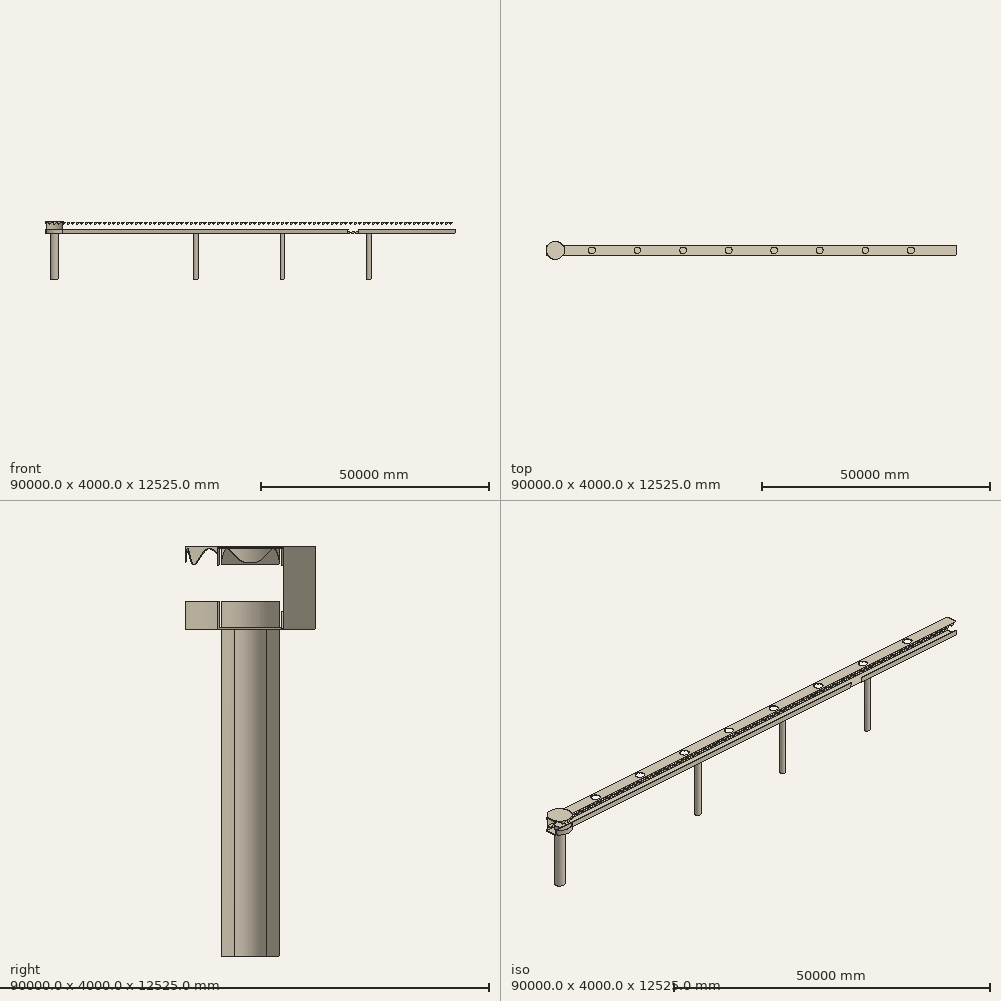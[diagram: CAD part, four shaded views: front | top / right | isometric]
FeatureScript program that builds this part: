
annotation { "Feature Type Name" : "Feature", "Feature Type Description" : "" }
export const myFeature = defineFeature(function(context is Context, id is Id, definition is map)
    precondition{}
    {
        {
            var Q0;
            Q0=qCreatedBy(makeId("Top.planeOp"),FACE);
            var sketch = newSketch(context, id + "F0", { "sketchPlane" : qUnion([Q0])});
            skLineSegment(sketch, "E0.bottom", {"start": v(-90023.74, 2042.27) * mm, "end": v(-23.74, 2042.27) * mm});
            skLineSegment(sketch, "E0.top", {"start": v(-90023.74, 42.27) * mm, "end": v(-23.74, 42.27) * mm});
            skLineSegment(sketch, "E0.left", {"start": v(-90023.74, 2042.27) * mm, "end": v(-90023.74, 42.27) * mm});
            skLineSegment(sketch, "E0.right", {"start": v(-23.74, 2042.27) * mm, "end": v(-23.74, 42.27) * mm});
            skSolve(sketch);
        }
        {
            var Q0;
            Q0=makeQuery(id+"F0.imprint","IMPRINT",FACE,{"disambiguationData":[TD([[makeQuery(id+"F0.imprint","IMPRINT",EDGE,{"derivedFrom":sQuery(id+"F0.wireOp",EDGE,"E0.bottom")}),-1.0]])]});
            extrude(context, id + "F1", {"entities" : qUnion([Q0]), "depth" : 2500 * mm});
        }
        {
            var Q0;
            Q0=makeQuery(id+"F1.opExtrude","SWEPT_FACE",FACE,{"disambiguationData":[OSD([sQuery(id+"F0.wireOp",EDGE,"E0.left")])]});
            var sketch = newSketch(context, id + "F2", { "sketchPlane" : qUnion([Q0])});
            skLineSegment(sketch, "E1", {"start": v(-92.27, 2356.2) * mm, "end": v(-92.27, 53.5) * mm});
            skLineSegment(sketch, "E2", {"start": v(-1649.58, 53.5) * mm, "end": v(-1992.27, 53.5) * mm});
            skLineSegment(sketch, "E3", {"start": v(-1992.27, 183.32) * mm, "end": v(-1992.27, 53.5) * mm});
            skLineSegment(sketch, "E4", {"start": v(-1649.58, 53.5) * mm, "end": v(-92.27, 53.5) * mm});
            skLineSegment(sketch, "E5", {"start": v(-92.27, 2356.2) * mm, "end": v(-92.27, 2450) * mm});
            skLineSegment(sketch, "E6", {"start": v(-1903.07, 2450) * mm, "end": v(-1992.27, 2450) * mm});
            skLineSegment(sketch, "E7", {"start": v(-1992.27, 183.32) * mm, "end": v(-1992.27, 2450) * mm});
            skLineSegment(sketch, "E8", {"start": v(-1903.07, 2450) * mm, "end": v(-92.27, 2450) * mm});
            skSolve(sketch);
        }
        {
            var Q0;
            Q0=makeQuery(id+"F2.imprint","IMPRINT",FACE,{"disambiguationData":[TD([[makeQuery(id+"F2.imprint","IMPRINT",EDGE,{"derivedFrom":sQuery(id+"F2.wireOp",EDGE,"E1")}),-1.0]])]});
            extrude(context, id + "F3", {"entities" : qUnion([Q0]), "operationType" : NewBodyOperationType.REMOVE, "oppositeDirection" : true, "depth" : 90000 * mm});
        }
        {
            var Q0;
            Q0=makeQuery(id+"F1.opExtrude","SWEPT_FACE",FACE,{"disambiguationData":[OSD([sQuery(id+"F0.wireOp",EDGE,"E0.bottom")])]});
            var sketch = newSketch(context, id + "F4", { "sketchPlane" : qUnion([Q0])});
            skPoint(sketch, "E9.1.internal.snap0", {"position": v(523.74, 312) * mm});
            skLineSegment(sketch, "E10", {"start": v(255.14, 833) * mm, "end": v(0, 833) * mm});
            skLineSegment(sketch, "E11", {"start": v(255.14, 833) * mm, "end": v(1023.74, 833) * mm});
            skLineSegment(sketch, "E12", {"start": v(198.44, 33) * mm, "end": v(1023.74, 33) * mm});
            skLineSegment(sketch, "E13", {"start": v(198.44, 33) * mm, "end": v(23.74, 33) * mm});
            skLineSegment(sketch, "E14", {"start": v(23.74, 533) * mm, "end": v(453.74, 533) * mm});
            skLineSegment(sketch, "E15", {"start": v(453.74, 33) * mm, "end": v(453.74, 533) * mm});
            skLineSegment(sketch, "E16", {"start": v(1023.74, 533) * mm, "end": v(1453.74, 533) * mm});
            skLineSegment(sketch, "E17", {"start": v(1453.74, 33) * mm, "end": v(1453.74, 533) * mm});
            skLineSegment(sketch, "E18", {"start": v(1023.74, 33) * mm, "end": v(2023.74, 33) * mm});
            skLineSegment(sketch, "E19", {"start": v(2023.74, 0) * mm, "end": v(2023.74, 833) * mm});
            skLineSegment(sketch, "E20", {"start": v(2023.74, 833) * mm, "end": v(1023.74, 833) * mm});
            skLineSegment(sketch, "E21", {"start": v(1023.74, 33) * mm, "end": v(1023.74, 833) * mm});
            skPoint(sketch, "E22.1.internal.snap0", {"position": v(2523.74, 312) * mm});
            skLineSegment(sketch, "E23", {"start": v(2255.14, 833) * mm, "end": v(2000, 833) * mm});
            skLineSegment(sketch, "E24", {"start": v(2255.14, 833) * mm, "end": v(3023.74, 833) * mm});
            skLineSegment(sketch, "E25", {"start": v(2198.44, 33) * mm, "end": v(3023.74, 33) * mm});
            skLineSegment(sketch, "E26", {"start": v(2198.44, 33) * mm, "end": v(2023.74, 33) * mm});
            skLineSegment(sketch, "E27", {"start": v(2023.74, 533) * mm, "end": v(2453.74, 533) * mm});
            skLineSegment(sketch, "E28", {"start": v(2453.74, 33) * mm, "end": v(2453.74, 533) * mm});
            skLineSegment(sketch, "E29", {"start": v(3023.74, 33) * mm, "end": v(3023.74, 833) * mm});
            skPoint(sketch, "E30.1.internal.snap0", {"position": v(3523.74, 312) * mm});
            skLineSegment(sketch, "E31", {"start": v(3255.14, 833) * mm, "end": v(3000, 833) * mm});
            skLineSegment(sketch, "E32", {"start": v(3255.14, 833) * mm, "end": v(4023.74, 833) * mm});
            skLineSegment(sketch, "E33", {"start": v(3198.44, 33) * mm, "end": v(4023.74, 33) * mm});
            skLineSegment(sketch, "E34", {"start": v(3198.44, 33) * mm, "end": v(3023.74, 33) * mm});
            skLineSegment(sketch, "E35", {"start": v(3023.74, 533) * mm, "end": v(3453.74, 533) * mm});
            skLineSegment(sketch, "E36", {"start": v(3453.74, 33) * mm, "end": v(3453.74, 533) * mm});
            skLineSegment(sketch, "E37", {"start": v(4023.74, 33) * mm, "end": v(4023.74, 833) * mm});
            skPoint(sketch, "E38.1.internal.snap0", {"position": v(4523.74, 312) * mm});
            skLineSegment(sketch, "E39", {"start": v(4255.14, 833) * mm, "end": v(4000, 833) * mm});
            skLineSegment(sketch, "E40", {"start": v(4255.14, 833) * mm, "end": v(5023.74, 833) * mm});
            skLineSegment(sketch, "E41", {"start": v(4198.44, 33) * mm, "end": v(5023.74, 33) * mm});
            skLineSegment(sketch, "E42", {"start": v(4198.44, 33) * mm, "end": v(4023.74, 33) * mm});
            skLineSegment(sketch, "E43", {"start": v(4023.74, 533) * mm, "end": v(4453.74, 533) * mm});
            skLineSegment(sketch, "E44", {"start": v(4453.74, 33) * mm, "end": v(4453.74, 533) * mm});
            skLineSegment(sketch, "E45", {"start": v(5023.74, 33) * mm, "end": v(5023.74, 833) * mm});
            skPoint(sketch, "E46.1.internal.snap0", {"position": v(5523.74, 312) * mm});
            skLineSegment(sketch, "E47", {"start": v(5255.14, 833) * mm, "end": v(5000, 833) * mm});
            skLineSegment(sketch, "E48", {"start": v(5255.14, 833) * mm, "end": v(6023.74, 833) * mm});
            skLineSegment(sketch, "E49", {"start": v(5198.44, 33) * mm, "end": v(6023.74, 33) * mm});
            skLineSegment(sketch, "E50", {"start": v(5198.44, 33) * mm, "end": v(5023.74, 33) * mm});
            skLineSegment(sketch, "E51", {"start": v(5023.74, 533) * mm, "end": v(5453.74, 533) * mm});
            skLineSegment(sketch, "E52", {"start": v(5453.74, 33) * mm, "end": v(5453.74, 533) * mm});
            skLineSegment(sketch, "E53", {"start": v(6023.74, 33) * mm, "end": v(6023.74, 833) * mm});
            skPoint(sketch, "E54.1.internal.snap0", {"position": v(6523.74, 312) * mm});
            skLineSegment(sketch, "E55", {"start": v(6255.14, 833) * mm, "end": v(6000, 833) * mm});
            skLineSegment(sketch, "E56", {"start": v(6255.14, 833) * mm, "end": v(7023.74, 833) * mm});
            skLineSegment(sketch, "E57", {"start": v(6198.44, 33) * mm, "end": v(7023.74, 33) * mm});
            skLineSegment(sketch, "E58", {"start": v(6198.44, 33) * mm, "end": v(6023.74, 33) * mm});
            skLineSegment(sketch, "E59", {"start": v(6023.74, 533) * mm, "end": v(6453.74, 533) * mm});
            skLineSegment(sketch, "E60", {"start": v(6453.74, 33) * mm, "end": v(6453.74, 533) * mm});
            skLineSegment(sketch, "E61", {"start": v(7023.74, 33) * mm, "end": v(7023.74, 833) * mm});
            skPoint(sketch, "E62.1.internal.snap0", {"position": v(7523.74, 312) * mm});
            skLineSegment(sketch, "E63", {"start": v(7255.14, 833) * mm, "end": v(7000, 833) * mm});
            skLineSegment(sketch, "E64", {"start": v(7255.14, 833) * mm, "end": v(8023.74, 833) * mm});
            skLineSegment(sketch, "E65", {"start": v(7198.44, 33) * mm, "end": v(8023.74, 33) * mm});
            skLineSegment(sketch, "E66", {"start": v(7198.44, 33) * mm, "end": v(7023.74, 33) * mm});
            skLineSegment(sketch, "E67", {"start": v(7023.74, 533) * mm, "end": v(7453.74, 533) * mm});
            skLineSegment(sketch, "E68", {"start": v(7453.74, 33) * mm, "end": v(7453.74, 533) * mm});
            skLineSegment(sketch, "E69", {"start": v(8023.74, 33) * mm, "end": v(8023.74, 833) * mm});
            skLineSegment(sketch, "E70", {"start": v(8023.74, 0) * mm, "end": v(8023.74, 833) * mm});
            skPoint(sketch, "E71.1.internal.snap0", {"position": v(8523.74, 312) * mm});
            skLineSegment(sketch, "E72", {"start": v(8255.14, 833) * mm, "end": v(8000, 833) * mm});
            skLineSegment(sketch, "E73", {"start": v(8255.14, 833) * mm, "end": v(9023.74, 833) * mm});
            skLineSegment(sketch, "E74", {"start": v(8198.44, 33) * mm, "end": v(9023.74, 33) * mm});
            skLineSegment(sketch, "E75", {"start": v(8198.44, 33) * mm, "end": v(8023.74, 33) * mm});
            skLineSegment(sketch, "E76", {"start": v(8023.74, 533) * mm, "end": v(8453.74, 533) * mm});
            skLineSegment(sketch, "E77", {"start": v(8453.74, 33) * mm, "end": v(8453.74, 533) * mm});
            skLineSegment(sketch, "E78", {"start": v(9023.74, 33) * mm, "end": v(9023.74, 833) * mm});
            skPoint(sketch, "E79.1.internal.snap0", {"position": v(9523.74, 312) * mm});
            skLineSegment(sketch, "E80", {"start": v(9255.14, 833) * mm, "end": v(9000, 833) * mm});
            skLineSegment(sketch, "E81", {"start": v(9255.14, 833) * mm, "end": v(10023.74, 833) * mm});
            skLineSegment(sketch, "E82", {"start": v(9198.44, 33) * mm, "end": v(10023.74, 33) * mm});
            skLineSegment(sketch, "E83", {"start": v(9198.44, 33) * mm, "end": v(9023.74, 33) * mm});
            skLineSegment(sketch, "E84", {"start": v(9023.74, 533) * mm, "end": v(9453.74, 533) * mm});
            skLineSegment(sketch, "E85", {"start": v(9453.74, 33) * mm, "end": v(9453.74, 533) * mm});
            skLineSegment(sketch, "E86", {"start": v(10023.74, 33) * mm, "end": v(10023.74, 833) * mm});
            skPoint(sketch, "E87.1.internal.snap0", {"position": v(10523.74, 312) * mm});
            skLineSegment(sketch, "E88", {"start": v(10255.14, 833) * mm, "end": v(10000, 833) * mm});
            skLineSegment(sketch, "E89", {"start": v(10255.14, 833) * mm, "end": v(11023.74, 833) * mm});
            skLineSegment(sketch, "E90", {"start": v(10198.44, 33) * mm, "end": v(11023.74, 33) * mm});
            skLineSegment(sketch, "E91", {"start": v(10198.44, 33) * mm, "end": v(10023.74, 33) * mm});
            skLineSegment(sketch, "E92", {"start": v(10023.74, 533) * mm, "end": v(10453.74, 533) * mm});
            skLineSegment(sketch, "E93", {"start": v(10453.74, 33) * mm, "end": v(10453.74, 533) * mm});
            skLineSegment(sketch, "E94", {"start": v(11023.74, 33) * mm, "end": v(11023.74, 833) * mm});
            skPoint(sketch, "E95.1.internal.snap0", {"position": v(11523.74, 312) * mm});
            skLineSegment(sketch, "E96", {"start": v(11255.14, 833) * mm, "end": v(11000, 833) * mm});
            skLineSegment(sketch, "E97", {"start": v(11255.14, 833) * mm, "end": v(12023.74, 833) * mm});
            skLineSegment(sketch, "E98", {"start": v(11198.44, 33) * mm, "end": v(12023.74, 33) * mm});
            skLineSegment(sketch, "E99", {"start": v(11198.44, 33) * mm, "end": v(11023.74, 33) * mm});
            skLineSegment(sketch, "E100", {"start": v(11023.74, 533) * mm, "end": v(11453.74, 533) * mm});
            skLineSegment(sketch, "E101", {"start": v(11453.74, 33) * mm, "end": v(11453.74, 533) * mm});
            skLineSegment(sketch, "E102", {"start": v(12023.74, 33) * mm, "end": v(12023.74, 833) * mm});
            skPoint(sketch, "E103.1.internal.snap0", {"position": v(12523.74, 312) * mm});
            skLineSegment(sketch, "E104", {"start": v(12255.14, 833) * mm, "end": v(12000, 833) * mm});
            skLineSegment(sketch, "E105", {"start": v(12255.14, 833) * mm, "end": v(13023.74, 833) * mm});
            skLineSegment(sketch, "E106", {"start": v(12198.44, 33) * mm, "end": v(13023.74, 33) * mm});
            skLineSegment(sketch, "E107", {"start": v(12198.44, 33) * mm, "end": v(12023.74, 33) * mm});
            skLineSegment(sketch, "E108", {"start": v(12023.74, 533) * mm, "end": v(12453.74, 533) * mm});
            skLineSegment(sketch, "E109", {"start": v(12453.74, 33) * mm, "end": v(12453.74, 533) * mm});
            skLineSegment(sketch, "E110", {"start": v(13023.74, 33) * mm, "end": v(13023.74, 833) * mm});
            skPoint(sketch, "E111.1.internal.snap0", {"position": v(13523.74, 312) * mm});
            skLineSegment(sketch, "E112", {"start": v(13255.14, 833) * mm, "end": v(13000, 833) * mm});
            skLineSegment(sketch, "E113", {"start": v(13255.14, 833) * mm, "end": v(14023.74, 833) * mm});
            skLineSegment(sketch, "E114", {"start": v(13198.44, 33) * mm, "end": v(14023.74, 33) * mm});
            skLineSegment(sketch, "E115", {"start": v(13198.44, 33) * mm, "end": v(13023.74, 33) * mm});
            skLineSegment(sketch, "E116", {"start": v(13023.74, 533) * mm, "end": v(13453.74, 533) * mm});
            skLineSegment(sketch, "E117", {"start": v(13453.74, 33) * mm, "end": v(13453.74, 533) * mm});
            skLineSegment(sketch, "E118", {"start": v(14023.74, 33) * mm, "end": v(14023.74, 833) * mm});
            skPoint(sketch, "E119.1.internal.snap0", {"position": v(14523.74, 312) * mm});
            skLineSegment(sketch, "E120", {"start": v(14255.14, 833) * mm, "end": v(14000, 833) * mm});
            skLineSegment(sketch, "E121", {"start": v(14255.14, 833) * mm, "end": v(15023.74, 833) * mm});
            skLineSegment(sketch, "E122", {"start": v(14198.44, 33) * mm, "end": v(15023.74, 33) * mm});
            skLineSegment(sketch, "E123", {"start": v(14198.44, 33) * mm, "end": v(14023.74, 33) * mm});
            skLineSegment(sketch, "E124", {"start": v(14023.74, 533) * mm, "end": v(14453.74, 533) * mm});
            skLineSegment(sketch, "E125", {"start": v(14453.74, 33) * mm, "end": v(14453.74, 533) * mm});
            skLineSegment(sketch, "E126", {"start": v(15023.74, 33) * mm, "end": v(15023.74, 833) * mm});
            skPoint(sketch, "E127.1.internal.snap0", {"position": v(15523.74, 312) * mm});
            skLineSegment(sketch, "E128", {"start": v(15255.14, 833) * mm, "end": v(15000, 833) * mm});
            skLineSegment(sketch, "E129", {"start": v(15255.14, 833) * mm, "end": v(16023.74, 833) * mm});
            skLineSegment(sketch, "E130", {"start": v(15198.44, 33) * mm, "end": v(16023.74, 33) * mm});
            skLineSegment(sketch, "E131", {"start": v(15198.44, 33) * mm, "end": v(15023.74, 33) * mm});
            skLineSegment(sketch, "E132", {"start": v(15023.74, 533) * mm, "end": v(15453.74, 533) * mm});
            skLineSegment(sketch, "E133", {"start": v(15453.74, 33) * mm, "end": v(15453.74, 533) * mm});
            skLineSegment(sketch, "E134", {"start": v(16023.74, 33) * mm, "end": v(16023.74, 833) * mm});
            skPoint(sketch, "E135.1.internal.snap0", {"position": v(16523.74, 312) * mm});
            skLineSegment(sketch, "E136", {"start": v(16255.14, 833) * mm, "end": v(16000, 833) * mm});
            skLineSegment(sketch, "E137", {"start": v(16255.14, 833) * mm, "end": v(17023.74, 833) * mm});
            skLineSegment(sketch, "E138", {"start": v(16198.44, 33) * mm, "end": v(17023.74, 33) * mm});
            skLineSegment(sketch, "E139", {"start": v(16198.44, 33) * mm, "end": v(16023.74, 33) * mm});
            skLineSegment(sketch, "E140", {"start": v(16023.74, 533) * mm, "end": v(16453.74, 533) * mm});
            skLineSegment(sketch, "E141", {"start": v(16453.74, 33) * mm, "end": v(16453.74, 533) * mm});
            skLineSegment(sketch, "E142", {"start": v(17023.74, 33) * mm, "end": v(17023.74, 833) * mm});
            skPoint(sketch, "E143.1.internal.snap0", {"position": v(17523.74, 312) * mm});
            skLineSegment(sketch, "E144", {"start": v(17255.14, 833) * mm, "end": v(17000, 833) * mm});
            skLineSegment(sketch, "E145", {"start": v(17255.14, 833) * mm, "end": v(18023.74, 833) * mm});
            skLineSegment(sketch, "E146", {"start": v(17198.44, 33) * mm, "end": v(18023.74, 33) * mm});
            skLineSegment(sketch, "E147", {"start": v(17198.44, 33) * mm, "end": v(17023.74, 33) * mm});
            skLineSegment(sketch, "E148", {"start": v(17023.74, 533) * mm, "end": v(17453.74, 533) * mm});
            skLineSegment(sketch, "E149", {"start": v(17453.74, 33) * mm, "end": v(17453.74, 533) * mm});
            skLineSegment(sketch, "E150", {"start": v(18023.74, 33) * mm, "end": v(18023.74, 833) * mm});
            skPoint(sketch, "E151.1.internal.snap0", {"position": v(18523.74, 312) * mm});
            skLineSegment(sketch, "E152", {"start": v(18255.14, 833) * mm, "end": v(18000, 833) * mm});
            skLineSegment(sketch, "E153", {"start": v(18255.14, 833) * mm, "end": v(19023.74, 833) * mm});
            skLineSegment(sketch, "E154", {"start": v(18198.44, 33) * mm, "end": v(19023.74, 33) * mm});
            skLineSegment(sketch, "E155", {"start": v(18198.44, 33) * mm, "end": v(18023.74, 33) * mm});
            skLineSegment(sketch, "E156", {"start": v(18023.74, 533) * mm, "end": v(18453.74, 533) * mm});
            skLineSegment(sketch, "E157", {"start": v(18453.74, 33) * mm, "end": v(18453.74, 533) * mm});
            skLineSegment(sketch, "E158", {"start": v(19023.74, 33) * mm, "end": v(19023.74, 833) * mm});
            skPoint(sketch, "E159.1.internal.snap0", {"position": v(19523.74, 312) * mm});
            skLineSegment(sketch, "E160", {"start": v(19255.14, 833) * mm, "end": v(19000, 833) * mm});
            skLineSegment(sketch, "E161", {"start": v(19255.14, 833) * mm, "end": v(20023.74, 833) * mm});
            skLineSegment(sketch, "E162", {"start": v(19198.44, 33) * mm, "end": v(20023.74, 33) * mm});
            skLineSegment(sketch, "E163", {"start": v(19198.44, 33) * mm, "end": v(19023.74, 33) * mm});
            skLineSegment(sketch, "E164", {"start": v(19023.74, 533) * mm, "end": v(19453.74, 533) * mm});
            skLineSegment(sketch, "E165", {"start": v(19453.74, 33) * mm, "end": v(19453.74, 533) * mm});
            skLineSegment(sketch, "E166", {"start": v(20023.74, 33) * mm, "end": v(20023.74, 833) * mm});
            skPoint(sketch, "E167.1.internal.snap0", {"position": v(20523.74, 312) * mm});
            skLineSegment(sketch, "E168", {"start": v(20255.14, 833) * mm, "end": v(20000, 833) * mm});
            skLineSegment(sketch, "E169", {"start": v(20255.14, 833) * mm, "end": v(21023.74, 833) * mm});
            skLineSegment(sketch, "E170", {"start": v(20198.44, 33) * mm, "end": v(21023.74, 33) * mm});
            skLineSegment(sketch, "E171", {"start": v(20198.44, 33) * mm, "end": v(20023.74, 33) * mm});
            skLineSegment(sketch, "E172", {"start": v(20023.74, 533) * mm, "end": v(20453.74, 533) * mm});
            skLineSegment(sketch, "E173", {"start": v(20453.74, 33) * mm, "end": v(20453.74, 533) * mm});
            skLineSegment(sketch, "E174", {"start": v(21023.74, 33) * mm, "end": v(21023.74, 833) * mm});
            skPoint(sketch, "E175.1.internal.snap0", {"position": v(21523.74, 312) * mm});
            skLineSegment(sketch, "E176", {"start": v(21255.14, 833) * mm, "end": v(21000, 833) * mm});
            skLineSegment(sketch, "E177", {"start": v(21255.14, 833) * mm, "end": v(22023.74, 833) * mm});
            skLineSegment(sketch, "E178", {"start": v(21198.44, 33) * mm, "end": v(22023.74, 33) * mm});
            skLineSegment(sketch, "E179", {"start": v(21198.44, 33) * mm, "end": v(21023.74, 33) * mm});
            skLineSegment(sketch, "E180", {"start": v(21023.74, 533) * mm, "end": v(21453.74, 533) * mm});
            skLineSegment(sketch, "E181", {"start": v(21453.74, 33) * mm, "end": v(21453.74, 533) * mm});
            skLineSegment(sketch, "E182", {"start": v(22023.74, 33) * mm, "end": v(22023.74, 833) * mm});
            skPoint(sketch, "E183.1.internal.snap0", {"position": v(22523.74, 312) * mm});
            skLineSegment(sketch, "E184", {"start": v(22255.14, 833) * mm, "end": v(22000, 833) * mm});
            skLineSegment(sketch, "E185", {"start": v(22255.14, 833) * mm, "end": v(23023.74, 833) * mm});
            skLineSegment(sketch, "E186", {"start": v(22198.44, 33) * mm, "end": v(23023.74, 33) * mm});
            skLineSegment(sketch, "E187", {"start": v(22198.44, 33) * mm, "end": v(22023.74, 33) * mm});
            skLineSegment(sketch, "E188", {"start": v(22023.74, 533) * mm, "end": v(22453.74, 533) * mm});
            skLineSegment(sketch, "E189", {"start": v(22453.74, 33) * mm, "end": v(22453.74, 533) * mm});
            skLineSegment(sketch, "E190", {"start": v(23023.74, 33) * mm, "end": v(23023.74, 833) * mm});
            skPoint(sketch, "E191.1.internal.snap0", {"position": v(23523.74, 312) * mm});
            skLineSegment(sketch, "E192", {"start": v(23255.14, 833) * mm, "end": v(23000, 833) * mm});
            skLineSegment(sketch, "E193", {"start": v(23255.14, 833) * mm, "end": v(24023.74, 833) * mm});
            skLineSegment(sketch, "E194", {"start": v(23198.44, 33) * mm, "end": v(24023.74, 33) * mm});
            skLineSegment(sketch, "E195", {"start": v(23198.44, 33) * mm, "end": v(23023.74, 33) * mm});
            skLineSegment(sketch, "E196", {"start": v(23023.74, 533) * mm, "end": v(23453.74, 533) * mm});
            skLineSegment(sketch, "E197", {"start": v(23453.74, 33) * mm, "end": v(23453.74, 533) * mm});
            skLineSegment(sketch, "E198", {"start": v(24023.74, 33) * mm, "end": v(24023.74, 833) * mm});
            skPoint(sketch, "E199.1.internal.snap0", {"position": v(24523.74, 312) * mm});
            skLineSegment(sketch, "E200", {"start": v(24255.14, 833) * mm, "end": v(24000, 833) * mm});
            skLineSegment(sketch, "E201", {"start": v(24255.14, 833) * mm, "end": v(25023.74, 833) * mm});
            skLineSegment(sketch, "E202", {"start": v(24198.44, 33) * mm, "end": v(25023.74, 33) * mm});
            skLineSegment(sketch, "E203", {"start": v(24198.44, 33) * mm, "end": v(24023.74, 33) * mm});
            skLineSegment(sketch, "E204", {"start": v(24023.74, 533) * mm, "end": v(24453.74, 533) * mm});
            skLineSegment(sketch, "E205", {"start": v(24453.74, 33) * mm, "end": v(24453.74, 533) * mm});
            skLineSegment(sketch, "E206", {"start": v(25023.74, 33) * mm, "end": v(25023.74, 833) * mm});
            skPoint(sketch, "E207.1.internal.snap0", {"position": v(25523.74, 312) * mm});
            skLineSegment(sketch, "E208", {"start": v(25255.14, 833) * mm, "end": v(25000, 833) * mm});
            skLineSegment(sketch, "E209", {"start": v(25255.14, 833) * mm, "end": v(26023.74, 833) * mm});
            skLineSegment(sketch, "E210", {"start": v(25198.44, 33) * mm, "end": v(26023.74, 33) * mm});
            skLineSegment(sketch, "E211", {"start": v(25198.44, 33) * mm, "end": v(25023.74, 33) * mm});
            skLineSegment(sketch, "E212", {"start": v(25023.74, 533) * mm, "end": v(25453.74, 533) * mm});
            skLineSegment(sketch, "E213", {"start": v(25453.74, 33) * mm, "end": v(25453.74, 533) * mm});
            skLineSegment(sketch, "E214", {"start": v(26023.74, 33) * mm, "end": v(26023.74, 833) * mm});
            skPoint(sketch, "E215.1.internal.snap0", {"position": v(26523.74, 312) * mm});
            skLineSegment(sketch, "E216", {"start": v(26255.14, 833) * mm, "end": v(26000, 833) * mm});
            skLineSegment(sketch, "E217", {"start": v(26255.14, 833) * mm, "end": v(27023.74, 833) * mm});
            skLineSegment(sketch, "E218", {"start": v(26198.44, 33) * mm, "end": v(27023.74, 33) * mm});
            skLineSegment(sketch, "E219", {"start": v(26198.44, 33) * mm, "end": v(26023.74, 33) * mm});
            skLineSegment(sketch, "E220", {"start": v(26023.74, 533) * mm, "end": v(26453.74, 533) * mm});
            skLineSegment(sketch, "E221", {"start": v(26453.74, 33) * mm, "end": v(26453.74, 533) * mm});
            skLineSegment(sketch, "E222", {"start": v(27023.74, 33) * mm, "end": v(27023.74, 833) * mm});
            skLineSegment(sketch, "E223", {"start": v(27023.74, 0) * mm, "end": v(27023.74, 833) * mm});
            skPoint(sketch, "E224.1.internal.snap0", {"position": v(27523.74, 312) * mm});
            skLineSegment(sketch, "E225", {"start": v(27255.14, 833) * mm, "end": v(27000, 833) * mm});
            skLineSegment(sketch, "E226", {"start": v(27255.14, 833) * mm, "end": v(28023.74, 833) * mm});
            skLineSegment(sketch, "E227", {"start": v(27198.44, 33) * mm, "end": v(28023.74, 33) * mm});
            skLineSegment(sketch, "E228", {"start": v(27198.44, 33) * mm, "end": v(27023.74, 33) * mm});
            skLineSegment(sketch, "E229", {"start": v(27023.74, 533) * mm, "end": v(27453.74, 533) * mm});
            skLineSegment(sketch, "E230", {"start": v(27453.74, 33) * mm, "end": v(27453.74, 533) * mm});
            skLineSegment(sketch, "E231", {"start": v(28023.74, 33) * mm, "end": v(28023.74, 833) * mm});
            skPoint(sketch, "E232.1.internal.snap0", {"position": v(28523.74, 312) * mm});
            skLineSegment(sketch, "E233", {"start": v(28255.14, 833) * mm, "end": v(28000, 833) * mm});
            skLineSegment(sketch, "E234", {"start": v(28255.14, 833) * mm, "end": v(29023.74, 833) * mm});
            skLineSegment(sketch, "E235", {"start": v(28198.44, 33) * mm, "end": v(29023.74, 33) * mm});
            skLineSegment(sketch, "E236", {"start": v(28198.44, 33) * mm, "end": v(28023.74, 33) * mm});
            skLineSegment(sketch, "E237", {"start": v(28023.74, 533) * mm, "end": v(28453.74, 533) * mm});
            skLineSegment(sketch, "E238", {"start": v(28453.74, 33) * mm, "end": v(28453.74, 533) * mm});
            skLineSegment(sketch, "E239", {"start": v(29023.74, 33) * mm, "end": v(29023.74, 833) * mm});
            skPoint(sketch, "E240.1.internal.snap0", {"position": v(29523.74, 312) * mm});
            skLineSegment(sketch, "E241", {"start": v(29255.14, 833) * mm, "end": v(29000, 833) * mm});
            skLineSegment(sketch, "E242", {"start": v(29255.14, 833) * mm, "end": v(30023.74, 833) * mm});
            skLineSegment(sketch, "E243", {"start": v(29198.44, 33) * mm, "end": v(30023.74, 33) * mm});
            skLineSegment(sketch, "E244", {"start": v(29198.44, 33) * mm, "end": v(29023.74, 33) * mm});
            skLineSegment(sketch, "E245", {"start": v(29023.74, 533) * mm, "end": v(29453.74, 533) * mm});
            skLineSegment(sketch, "E246", {"start": v(29453.74, 33) * mm, "end": v(29453.74, 533) * mm});
            skLineSegment(sketch, "E247", {"start": v(30023.74, 33) * mm, "end": v(30023.74, 833) * mm});
            skPoint(sketch, "E248.1.internal.snap0", {"position": v(30523.74, 312) * mm});
            skLineSegment(sketch, "E249", {"start": v(30255.14, 833) * mm, "end": v(30000, 833) * mm});
            skLineSegment(sketch, "E250", {"start": v(30255.14, 833) * mm, "end": v(31023.74, 833) * mm});
            skLineSegment(sketch, "E251", {"start": v(30198.44, 33) * mm, "end": v(31023.74, 33) * mm});
            skLineSegment(sketch, "E252", {"start": v(30198.44, 33) * mm, "end": v(30023.74, 33) * mm});
            skLineSegment(sketch, "E253", {"start": v(30023.74, 533) * mm, "end": v(30453.74, 533) * mm});
            skLineSegment(sketch, "E254", {"start": v(30453.74, 33) * mm, "end": v(30453.74, 533) * mm});
            skLineSegment(sketch, "E255", {"start": v(31023.74, 33) * mm, "end": v(31023.74, 833) * mm});
            skPoint(sketch, "E256.1.internal.snap0", {"position": v(31523.74, 312) * mm});
            skLineSegment(sketch, "E257", {"start": v(31255.14, 833) * mm, "end": v(31000, 833) * mm});
            skLineSegment(sketch, "E258", {"start": v(31255.14, 833) * mm, "end": v(32023.74, 833) * mm});
            skLineSegment(sketch, "E259", {"start": v(31198.44, 33) * mm, "end": v(32023.74, 33) * mm});
            skLineSegment(sketch, "E260", {"start": v(31198.44, 33) * mm, "end": v(31023.74, 33) * mm});
            skLineSegment(sketch, "E261", {"start": v(31023.74, 533) * mm, "end": v(31453.74, 533) * mm});
            skLineSegment(sketch, "E262", {"start": v(31453.74, 33) * mm, "end": v(31453.74, 533) * mm});
            skLineSegment(sketch, "E263", {"start": v(32023.74, 33) * mm, "end": v(32023.74, 833) * mm});
            skPoint(sketch, "E264.1.internal.snap0", {"position": v(32523.74, 312) * mm});
            skLineSegment(sketch, "E265", {"start": v(32255.14, 833) * mm, "end": v(32000, 833) * mm});
            skLineSegment(sketch, "E266", {"start": v(32255.14, 833) * mm, "end": v(33023.74, 833) * mm});
            skLineSegment(sketch, "E267", {"start": v(32198.44, 33) * mm, "end": v(33023.74, 33) * mm});
            skLineSegment(sketch, "E268", {"start": v(32198.44, 33) * mm, "end": v(32023.74, 33) * mm});
            skLineSegment(sketch, "E269", {"start": v(32023.74, 533) * mm, "end": v(32453.74, 533) * mm});
            skLineSegment(sketch, "E270", {"start": v(32453.74, 33) * mm, "end": v(32453.74, 533) * mm});
            skLineSegment(sketch, "E271", {"start": v(33023.74, 33) * mm, "end": v(33023.74, 833) * mm});
            skPoint(sketch, "E272.1.internal.snap0", {"position": v(33523.74, 312) * mm});
            skLineSegment(sketch, "E273", {"start": v(33255.14, 833) * mm, "end": v(33000, 833) * mm});
            skLineSegment(sketch, "E274", {"start": v(33255.14, 833) * mm, "end": v(34023.74, 833) * mm});
            skLineSegment(sketch, "E275", {"start": v(33198.44, 33) * mm, "end": v(34023.74, 33) * mm});
            skLineSegment(sketch, "E276", {"start": v(33198.44, 33) * mm, "end": v(33023.74, 33) * mm});
            skLineSegment(sketch, "E277", {"start": v(33023.74, 533) * mm, "end": v(33453.74, 533) * mm});
            skLineSegment(sketch, "E278", {"start": v(33453.74, 33) * mm, "end": v(33453.74, 533) * mm});
            skLineSegment(sketch, "E279", {"start": v(34023.74, 33) * mm, "end": v(34023.74, 833) * mm});
            skPoint(sketch, "E280.1.internal.snap0", {"position": v(34523.74, 312) * mm});
            skLineSegment(sketch, "E281", {"start": v(34255.14, 833) * mm, "end": v(34000, 833) * mm});
            skLineSegment(sketch, "E282", {"start": v(34255.14, 833) * mm, "end": v(35023.74, 833) * mm});
            skLineSegment(sketch, "E283", {"start": v(34198.44, 33) * mm, "end": v(35023.74, 33) * mm});
            skLineSegment(sketch, "E284", {"start": v(34198.44, 33) * mm, "end": v(34023.74, 33) * mm});
            skLineSegment(sketch, "E285", {"start": v(34023.74, 533) * mm, "end": v(34453.74, 533) * mm});
            skLineSegment(sketch, "E286", {"start": v(34453.74, 33) * mm, "end": v(34453.74, 533) * mm});
            skLineSegment(sketch, "E287", {"start": v(35023.74, 33) * mm, "end": v(35023.74, 833) * mm});
            skPoint(sketch, "E288.1.internal.snap0", {"position": v(35523.74, 312) * mm});
            skLineSegment(sketch, "E289", {"start": v(35255.14, 833) * mm, "end": v(35000, 833) * mm});
            skLineSegment(sketch, "E290", {"start": v(35255.14, 833) * mm, "end": v(36023.74, 833) * mm});
            skLineSegment(sketch, "E291", {"start": v(35198.44, 33) * mm, "end": v(36023.74, 33) * mm});
            skLineSegment(sketch, "E292", {"start": v(35198.44, 33) * mm, "end": v(35023.74, 33) * mm});
            skLineSegment(sketch, "E293", {"start": v(35023.74, 533) * mm, "end": v(35453.74, 533) * mm});
            skLineSegment(sketch, "E294", {"start": v(35453.74, 33) * mm, "end": v(35453.74, 533) * mm});
            skLineSegment(sketch, "E295", {"start": v(36023.74, 33) * mm, "end": v(36023.74, 833) * mm});
            skPoint(sketch, "E296.1.internal.snap0", {"position": v(36523.74, 312) * mm});
            skLineSegment(sketch, "E297", {"start": v(36255.14, 833) * mm, "end": v(36000, 833) * mm});
            skLineSegment(sketch, "E298", {"start": v(36255.14, 833) * mm, "end": v(37023.74, 833) * mm});
            skLineSegment(sketch, "E299", {"start": v(36198.44, 33) * mm, "end": v(37023.74, 33) * mm});
            skLineSegment(sketch, "E300", {"start": v(36198.44, 33) * mm, "end": v(36023.74, 33) * mm});
            skLineSegment(sketch, "E301", {"start": v(36023.74, 533) * mm, "end": v(36453.74, 533) * mm});
            skLineSegment(sketch, "E302", {"start": v(36453.74, 33) * mm, "end": v(36453.74, 533) * mm});
            skLineSegment(sketch, "E303", {"start": v(37023.74, 33) * mm, "end": v(37023.74, 833) * mm});
            skPoint(sketch, "E304.1.internal.snap0", {"position": v(37523.74, 312) * mm});
            skLineSegment(sketch, "E305", {"start": v(37255.14, 833) * mm, "end": v(37000, 833) * mm});
            skLineSegment(sketch, "E306", {"start": v(37255.14, 833) * mm, "end": v(38023.74, 833) * mm});
            skLineSegment(sketch, "E307", {"start": v(37198.44, 33) * mm, "end": v(38023.74, 33) * mm});
            skLineSegment(sketch, "E308", {"start": v(37198.44, 33) * mm, "end": v(37023.74, 33) * mm});
            skLineSegment(sketch, "E309", {"start": v(37023.74, 533) * mm, "end": v(37453.74, 533) * mm});
            skLineSegment(sketch, "E310", {"start": v(37453.74, 33) * mm, "end": v(37453.74, 533) * mm});
            skLineSegment(sketch, "E311", {"start": v(38023.74, 33) * mm, "end": v(38023.74, 833) * mm});
            skPoint(sketch, "E312.1.internal.snap0", {"position": v(38523.74, 312) * mm});
            skLineSegment(sketch, "E313", {"start": v(38255.14, 833) * mm, "end": v(38000, 833) * mm});
            skLineSegment(sketch, "E314", {"start": v(38255.14, 833) * mm, "end": v(39023.74, 833) * mm});
            skLineSegment(sketch, "E315", {"start": v(38198.44, 33) * mm, "end": v(39023.74, 33) * mm});
            skLineSegment(sketch, "E316", {"start": v(38198.44, 33) * mm, "end": v(38023.74, 33) * mm});
            skLineSegment(sketch, "E317", {"start": v(38023.74, 533) * mm, "end": v(38453.74, 533) * mm});
            skLineSegment(sketch, "E318", {"start": v(38453.74, 33) * mm, "end": v(38453.74, 533) * mm});
            skLineSegment(sketch, "E319", {"start": v(39023.74, 33) * mm, "end": v(39023.74, 833) * mm});
            skPoint(sketch, "E320.1.internal.snap0", {"position": v(39523.74, 312) * mm});
            skLineSegment(sketch, "E321", {"start": v(39255.14, 833) * mm, "end": v(39000, 833) * mm});
            skLineSegment(sketch, "E322", {"start": v(39255.14, 833) * mm, "end": v(40023.74, 833) * mm});
            skLineSegment(sketch, "E323", {"start": v(39198.44, 33) * mm, "end": v(40023.74, 33) * mm});
            skLineSegment(sketch, "E324", {"start": v(39198.44, 33) * mm, "end": v(39023.74, 33) * mm});
            skLineSegment(sketch, "E325", {"start": v(39023.74, 533) * mm, "end": v(39453.74, 533) * mm});
            skLineSegment(sketch, "E326", {"start": v(39453.74, 33) * mm, "end": v(39453.74, 533) * mm});
            skLineSegment(sketch, "E327", {"start": v(40023.74, 33) * mm, "end": v(40023.74, 833) * mm});
            skPoint(sketch, "E328.1.internal.snap0", {"position": v(40523.74, 312) * mm});
            skLineSegment(sketch, "E329", {"start": v(40255.14, 833) * mm, "end": v(40000, 833) * mm});
            skLineSegment(sketch, "E330", {"start": v(40255.14, 833) * mm, "end": v(41023.74, 833) * mm});
            skLineSegment(sketch, "E331", {"start": v(40198.44, 33) * mm, "end": v(41023.74, 33) * mm});
            skLineSegment(sketch, "E332", {"start": v(40198.44, 33) * mm, "end": v(40023.74, 33) * mm});
            skLineSegment(sketch, "E333", {"start": v(40023.74, 533) * mm, "end": v(40453.74, 533) * mm});
            skLineSegment(sketch, "E334", {"start": v(40453.74, 33) * mm, "end": v(40453.74, 533) * mm});
            skLineSegment(sketch, "E335", {"start": v(41023.74, 33) * mm, "end": v(41023.74, 833) * mm});
            skPoint(sketch, "E336.1.internal.snap0", {"position": v(41523.74, 312) * mm});
            skLineSegment(sketch, "E337", {"start": v(41255.14, 833) * mm, "end": v(41000, 833) * mm});
            skLineSegment(sketch, "E338", {"start": v(41255.14, 833) * mm, "end": v(42023.74, 833) * mm});
            skLineSegment(sketch, "E339", {"start": v(41198.44, 33) * mm, "end": v(42023.74, 33) * mm});
            skLineSegment(sketch, "E340", {"start": v(41198.44, 33) * mm, "end": v(41023.74, 33) * mm});
            skLineSegment(sketch, "E341", {"start": v(41023.74, 533) * mm, "end": v(41453.74, 533) * mm});
            skLineSegment(sketch, "E342", {"start": v(41453.74, 33) * mm, "end": v(41453.74, 533) * mm});
            skLineSegment(sketch, "E343", {"start": v(42023.74, 33) * mm, "end": v(42023.74, 833) * mm});
            skPoint(sketch, "E344.1.internal.snap0", {"position": v(42523.74, 312) * mm});
            skLineSegment(sketch, "E345", {"start": v(42255.14, 833) * mm, "end": v(42000, 833) * mm});
            skLineSegment(sketch, "E346", {"start": v(42255.14, 833) * mm, "end": v(43023.74, 833) * mm});
            skLineSegment(sketch, "E347", {"start": v(42198.44, 33) * mm, "end": v(43023.74, 33) * mm});
            skLineSegment(sketch, "E348", {"start": v(42198.44, 33) * mm, "end": v(42023.74, 33) * mm});
            skLineSegment(sketch, "E349", {"start": v(42023.74, 533) * mm, "end": v(42453.74, 533) * mm});
            skLineSegment(sketch, "E350", {"start": v(42453.74, 33) * mm, "end": v(42453.74, 533) * mm});
            skLineSegment(sketch, "E351", {"start": v(43023.74, 33) * mm, "end": v(43023.74, 833) * mm});
            skPoint(sketch, "E352.1.internal.snap0", {"position": v(43523.74, 312) * mm});
            skLineSegment(sketch, "E353", {"start": v(43255.14, 833) * mm, "end": v(43000, 833) * mm});
            skLineSegment(sketch, "E354", {"start": v(43255.14, 833) * mm, "end": v(44023.74, 833) * mm});
            skLineSegment(sketch, "E355", {"start": v(43198.44, 33) * mm, "end": v(44023.74, 33) * mm});
            skLineSegment(sketch, "E356", {"start": v(43198.44, 33) * mm, "end": v(43023.74, 33) * mm});
            skLineSegment(sketch, "E357", {"start": v(43023.74, 533) * mm, "end": v(43453.74, 533) * mm});
            skLineSegment(sketch, "E358", {"start": v(43453.74, 33) * mm, "end": v(43453.74, 533) * mm});
            skLineSegment(sketch, "E359", {"start": v(44023.74, 33) * mm, "end": v(44023.74, 833) * mm});
            skPoint(sketch, "E360.1.internal.snap0", {"position": v(44523.74, 312) * mm});
            skLineSegment(sketch, "E361", {"start": v(44255.14, 833) * mm, "end": v(44000, 833) * mm});
            skLineSegment(sketch, "E362", {"start": v(44255.14, 833) * mm, "end": v(45023.74, 833) * mm});
            skLineSegment(sketch, "E363", {"start": v(44198.44, 33) * mm, "end": v(45023.74, 33) * mm});
            skLineSegment(sketch, "E364", {"start": v(44198.44, 33) * mm, "end": v(44023.74, 33) * mm});
            skLineSegment(sketch, "E365", {"start": v(44023.74, 533) * mm, "end": v(44453.74, 533) * mm});
            skLineSegment(sketch, "E366", {"start": v(44453.74, 33) * mm, "end": v(44453.74, 533) * mm});
            skLineSegment(sketch, "E367", {"start": v(45023.74, 33) * mm, "end": v(45023.74, 833) * mm});
            skPoint(sketch, "E368.1.internal.snap0", {"position": v(45523.74, 312) * mm});
            skLineSegment(sketch, "E369", {"start": v(45255.14, 833) * mm, "end": v(45000, 833) * mm});
            skLineSegment(sketch, "E370", {"start": v(45255.14, 833) * mm, "end": v(46023.74, 833) * mm});
            skLineSegment(sketch, "E371", {"start": v(45198.44, 33) * mm, "end": v(46023.74, 33) * mm});
            skLineSegment(sketch, "E372", {"start": v(45198.44, 33) * mm, "end": v(45023.74, 33) * mm});
            skLineSegment(sketch, "E373", {"start": v(45023.74, 533) * mm, "end": v(45453.74, 533) * mm});
            skLineSegment(sketch, "E374", {"start": v(45453.74, 33) * mm, "end": v(45453.74, 533) * mm});
            skLineSegment(sketch, "E375", {"start": v(46023.74, 533) * mm, "end": v(46453.74, 533) * mm});
            skLineSegment(sketch, "E376", {"start": v(46453.74, 33) * mm, "end": v(46453.74, 533) * mm});
            skLineSegment(sketch, "E377", {"start": v(46023.74, 33) * mm, "end": v(47023.74, 33) * mm});
            skLineSegment(sketch, "E378", {"start": v(47023.74, 0) * mm, "end": v(47023.74, 833) * mm});
            skLineSegment(sketch, "E379", {"start": v(47023.74, 833) * mm, "end": v(46023.74, 833) * mm});
            skLineSegment(sketch, "E380", {"start": v(46023.74, 33) * mm, "end": v(46023.74, 833) * mm});
            skPoint(sketch, "E381.1.internal.snap0", {"position": v(47523.74, 312) * mm});
            skLineSegment(sketch, "E382", {"start": v(47255.14, 833) * mm, "end": v(47000, 833) * mm});
            skLineSegment(sketch, "E383", {"start": v(47255.14, 833) * mm, "end": v(48023.74, 833) * mm});
            skLineSegment(sketch, "E384", {"start": v(47198.44, 33) * mm, "end": v(48023.74, 33) * mm});
            skLineSegment(sketch, "E385", {"start": v(47198.44, 33) * mm, "end": v(47023.74, 33) * mm});
            skLineSegment(sketch, "E386", {"start": v(47023.74, 533) * mm, "end": v(47453.74, 533) * mm});
            skLineSegment(sketch, "E387", {"start": v(47453.74, 33) * mm, "end": v(47453.74, 533) * mm});
            skLineSegment(sketch, "E388", {"start": v(48023.74, 33) * mm, "end": v(48023.74, 833) * mm});
            skPoint(sketch, "E389.1.internal.snap0", {"position": v(48523.74, 312) * mm});
            skLineSegment(sketch, "E390", {"start": v(48255.14, 833) * mm, "end": v(48000, 833) * mm});
            skLineSegment(sketch, "E391", {"start": v(48255.14, 833) * mm, "end": v(49023.74, 833) * mm});
            skLineSegment(sketch, "E392", {"start": v(48198.44, 33) * mm, "end": v(49023.74, 33) * mm});
            skLineSegment(sketch, "E393", {"start": v(48198.44, 33) * mm, "end": v(48023.74, 33) * mm});
            skLineSegment(sketch, "E394", {"start": v(48023.74, 533) * mm, "end": v(48453.74, 533) * mm});
            skLineSegment(sketch, "E395", {"start": v(48453.74, 33) * mm, "end": v(48453.74, 533) * mm});
            skLineSegment(sketch, "E396", {"start": v(49023.74, 33) * mm, "end": v(49023.74, 833) * mm});
            skPoint(sketch, "E397.1.internal.snap0", {"position": v(49523.74, 312) * mm});
            skLineSegment(sketch, "E398", {"start": v(49255.14, 833) * mm, "end": v(49000, 833) * mm});
            skLineSegment(sketch, "E399", {"start": v(49255.14, 833) * mm, "end": v(50023.74, 833) * mm});
            skLineSegment(sketch, "E400", {"start": v(49198.44, 33) * mm, "end": v(50023.74, 33) * mm});
            skLineSegment(sketch, "E401", {"start": v(49198.44, 33) * mm, "end": v(49023.74, 33) * mm});
            skLineSegment(sketch, "E402", {"start": v(49023.74, 533) * mm, "end": v(49453.74, 533) * mm});
            skLineSegment(sketch, "E403", {"start": v(49453.74, 33) * mm, "end": v(49453.74, 533) * mm});
            skLineSegment(sketch, "E404", {"start": v(50023.74, 33) * mm, "end": v(50023.74, 833) * mm});
            skPoint(sketch, "E405.1.internal.snap0", {"position": v(50523.74, 312) * mm});
            skLineSegment(sketch, "E406", {"start": v(50255.14, 833) * mm, "end": v(50000, 833) * mm});
            skLineSegment(sketch, "E407", {"start": v(50255.14, 833) * mm, "end": v(51023.74, 833) * mm});
            skLineSegment(sketch, "E408", {"start": v(50198.44, 33) * mm, "end": v(51023.74, 33) * mm});
            skLineSegment(sketch, "E409", {"start": v(50198.44, 33) * mm, "end": v(50023.74, 33) * mm});
            skLineSegment(sketch, "E410", {"start": v(50023.74, 533) * mm, "end": v(50453.74, 533) * mm});
            skLineSegment(sketch, "E411", {"start": v(50453.74, 33) * mm, "end": v(50453.74, 533) * mm});
            skLineSegment(sketch, "E412", {"start": v(51023.74, 33) * mm, "end": v(51023.74, 833) * mm});
            skPoint(sketch, "E413.1.internal.snap0", {"position": v(51523.74, 312) * mm});
            skLineSegment(sketch, "E414", {"start": v(51255.14, 833) * mm, "end": v(51000, 833) * mm});
            skLineSegment(sketch, "E415", {"start": v(51255.14, 833) * mm, "end": v(52023.74, 833) * mm});
            skLineSegment(sketch, "E416", {"start": v(51198.44, 33) * mm, "end": v(52023.74, 33) * mm});
            skLineSegment(sketch, "E417", {"start": v(51198.44, 33) * mm, "end": v(51023.74, 33) * mm});
            skLineSegment(sketch, "E418", {"start": v(51023.74, 533) * mm, "end": v(51453.74, 533) * mm});
            skLineSegment(sketch, "E419", {"start": v(51453.74, 33) * mm, "end": v(51453.74, 533) * mm});
            skLineSegment(sketch, "E420", {"start": v(52023.74, 33) * mm, "end": v(52023.74, 833) * mm});
            skPoint(sketch, "E421.1.internal.snap0", {"position": v(52523.74, 312) * mm});
            skLineSegment(sketch, "E422", {"start": v(52255.14, 833) * mm, "end": v(52000, 833) * mm});
            skLineSegment(sketch, "E423", {"start": v(52255.14, 833) * mm, "end": v(53023.74, 833) * mm});
            skLineSegment(sketch, "E424", {"start": v(52198.44, 33) * mm, "end": v(53023.74, 33) * mm});
            skLineSegment(sketch, "E425", {"start": v(52198.44, 33) * mm, "end": v(52023.74, 33) * mm});
            skLineSegment(sketch, "E426", {"start": v(52023.74, 533) * mm, "end": v(52453.74, 533) * mm});
            skLineSegment(sketch, "E427", {"start": v(52453.74, 33) * mm, "end": v(52453.74, 533) * mm});
            skLineSegment(sketch, "E428", {"start": v(53023.74, 33) * mm, "end": v(53023.74, 833) * mm});
            skLineSegment(sketch, "E429", {"start": v(53023.74, 0) * mm, "end": v(53023.74, 833) * mm});
            skPoint(sketch, "E430.1.internal.snap0", {"position": v(53523.74, 312) * mm});
            skLineSegment(sketch, "E431", {"start": v(53255.14, 833) * mm, "end": v(53000, 833) * mm});
            skLineSegment(sketch, "E432", {"start": v(53255.14, 833) * mm, "end": v(54023.74, 833) * mm});
            skLineSegment(sketch, "E433", {"start": v(53198.44, 33) * mm, "end": v(54023.74, 33) * mm});
            skLineSegment(sketch, "E434", {"start": v(53198.44, 33) * mm, "end": v(53023.74, 33) * mm});
            skLineSegment(sketch, "E435", {"start": v(53023.74, 533) * mm, "end": v(53453.74, 533) * mm});
            skLineSegment(sketch, "E436", {"start": v(53453.74, 33) * mm, "end": v(53453.74, 533) * mm});
            skLineSegment(sketch, "E437", {"start": v(54023.74, 33) * mm, "end": v(54023.74, 833) * mm});
            skPoint(sketch, "E438.1.internal.snap0", {"position": v(54523.74, 312) * mm});
            skLineSegment(sketch, "E439", {"start": v(54255.14, 833) * mm, "end": v(54000, 833) * mm});
            skLineSegment(sketch, "E440", {"start": v(54255.14, 833) * mm, "end": v(55023.74, 833) * mm});
            skLineSegment(sketch, "E441", {"start": v(54198.44, 33) * mm, "end": v(55023.74, 33) * mm});
            skLineSegment(sketch, "E442", {"start": v(54198.44, 33) * mm, "end": v(54023.74, 33) * mm});
            skLineSegment(sketch, "E443", {"start": v(54023.74, 533) * mm, "end": v(54453.74, 533) * mm});
            skLineSegment(sketch, "E444", {"start": v(54453.74, 33) * mm, "end": v(54453.74, 533) * mm});
            skLineSegment(sketch, "E445", {"start": v(55023.74, 33) * mm, "end": v(55023.74, 833) * mm});
            skPoint(sketch, "E446.1.internal.snap0", {"position": v(55523.74, 312) * mm});
            skLineSegment(sketch, "E447", {"start": v(55255.14, 833) * mm, "end": v(55000, 833) * mm});
            skLineSegment(sketch, "E448", {"start": v(55255.14, 833) * mm, "end": v(56023.74, 833) * mm});
            skLineSegment(sketch, "E449", {"start": v(55198.44, 33) * mm, "end": v(56023.74, 33) * mm});
            skLineSegment(sketch, "E450", {"start": v(55198.44, 33) * mm, "end": v(55023.74, 33) * mm});
            skLineSegment(sketch, "E451", {"start": v(55023.74, 533) * mm, "end": v(55453.74, 533) * mm});
            skLineSegment(sketch, "E452", {"start": v(55453.74, 33) * mm, "end": v(55453.74, 533) * mm});
            skLineSegment(sketch, "E453", {"start": v(56023.74, 33) * mm, "end": v(56023.74, 833) * mm});
            skPoint(sketch, "E454.1.internal.snap0", {"position": v(56523.74, 312) * mm});
            skLineSegment(sketch, "E455", {"start": v(56255.14, 833) * mm, "end": v(56000, 833) * mm});
            skLineSegment(sketch, "E456", {"start": v(56255.14, 833) * mm, "end": v(57023.74, 833) * mm});
            skLineSegment(sketch, "E457", {"start": v(56198.44, 33) * mm, "end": v(57023.74, 33) * mm});
            skLineSegment(sketch, "E458", {"start": v(56198.44, 33) * mm, "end": v(56023.74, 33) * mm});
            skLineSegment(sketch, "E459", {"start": v(56023.74, 533) * mm, "end": v(56453.74, 533) * mm});
            skLineSegment(sketch, "E460", {"start": v(56453.74, 33) * mm, "end": v(56453.74, 533) * mm});
            skLineSegment(sketch, "E461", {"start": v(57023.74, 33) * mm, "end": v(57023.74, 833) * mm});
            skPoint(sketch, "E462.1.internal.snap0", {"position": v(57523.74, 312) * mm});
            skLineSegment(sketch, "E463", {"start": v(57255.14, 833) * mm, "end": v(57000, 833) * mm});
            skLineSegment(sketch, "E464", {"start": v(57255.14, 833) * mm, "end": v(58023.74, 833) * mm});
            skLineSegment(sketch, "E465", {"start": v(57198.44, 33) * mm, "end": v(58023.74, 33) * mm});
            skLineSegment(sketch, "E466", {"start": v(57198.44, 33) * mm, "end": v(57023.74, 33) * mm});
            skLineSegment(sketch, "E467", {"start": v(57023.74, 533) * mm, "end": v(57453.74, 533) * mm});
            skLineSegment(sketch, "E468", {"start": v(57453.74, 33) * mm, "end": v(57453.74, 533) * mm});
            skLineSegment(sketch, "E469", {"start": v(58023.74, 33) * mm, "end": v(58023.74, 833) * mm});
            skPoint(sketch, "E470.1.internal.snap0", {"position": v(58523.74, 312) * mm});
            skLineSegment(sketch, "E471", {"start": v(58255.14, 833) * mm, "end": v(58000, 833) * mm});
            skLineSegment(sketch, "E472", {"start": v(58255.14, 833) * mm, "end": v(59023.74, 833) * mm});
            skLineSegment(sketch, "E473", {"start": v(58198.44, 33) * mm, "end": v(59023.74, 33) * mm});
            skLineSegment(sketch, "E474", {"start": v(58198.44, 33) * mm, "end": v(58023.74, 33) * mm});
            skLineSegment(sketch, "E475", {"start": v(58023.74, 533) * mm, "end": v(58453.74, 533) * mm});
            skLineSegment(sketch, "E476", {"start": v(58453.74, 33) * mm, "end": v(58453.74, 533) * mm});
            skLineSegment(sketch, "E477", {"start": v(59023.74, 33) * mm, "end": v(59023.74, 833) * mm});
            skPoint(sketch, "E478.1.internal.snap0", {"position": v(59523.74, 312) * mm});
            skLineSegment(sketch, "E479", {"start": v(59255.14, 833) * mm, "end": v(59000, 833) * mm});
            skLineSegment(sketch, "E480", {"start": v(59255.14, 833) * mm, "end": v(60023.74, 833) * mm});
            skLineSegment(sketch, "E481", {"start": v(59198.44, 33) * mm, "end": v(60023.74, 33) * mm});
            skLineSegment(sketch, "E482", {"start": v(59198.44, 33) * mm, "end": v(59023.74, 33) * mm});
            skLineSegment(sketch, "E483", {"start": v(59023.74, 533) * mm, "end": v(59453.74, 533) * mm});
            skLineSegment(sketch, "E484", {"start": v(59453.74, 33) * mm, "end": v(59453.74, 533) * mm});
            skLineSegment(sketch, "E485", {"start": v(60023.74, 33) * mm, "end": v(60023.74, 833) * mm});
            skPoint(sketch, "E486.1.internal.snap0", {"position": v(60523.74, 312) * mm});
            skLineSegment(sketch, "E487", {"start": v(60255.14, 833) * mm, "end": v(60000, 833) * mm});
            skLineSegment(sketch, "E488", {"start": v(60255.14, 833) * mm, "end": v(61023.74, 833) * mm});
            skLineSegment(sketch, "E489", {"start": v(60198.44, 33) * mm, "end": v(61023.74, 33) * mm});
            skLineSegment(sketch, "E490", {"start": v(60198.44, 33) * mm, "end": v(60023.74, 33) * mm});
            skLineSegment(sketch, "E491", {"start": v(60023.74, 533) * mm, "end": v(60453.74, 533) * mm});
            skLineSegment(sketch, "E492", {"start": v(60453.74, 33) * mm, "end": v(60453.74, 533) * mm});
            skLineSegment(sketch, "E493", {"start": v(61023.74, 33) * mm, "end": v(61023.74, 833) * mm});
            skPoint(sketch, "E494.1.internal.snap0", {"position": v(61523.74, 312) * mm});
            skLineSegment(sketch, "E495", {"start": v(61255.14, 833) * mm, "end": v(61000, 833) * mm});
            skLineSegment(sketch, "E496", {"start": v(61255.14, 833) * mm, "end": v(62023.74, 833) * mm});
            skLineSegment(sketch, "E497", {"start": v(61198.44, 33) * mm, "end": v(62023.74, 33) * mm});
            skLineSegment(sketch, "E498", {"start": v(61198.44, 33) * mm, "end": v(61023.74, 33) * mm});
            skLineSegment(sketch, "E499", {"start": v(61023.74, 533) * mm, "end": v(61453.74, 533) * mm});
            skLineSegment(sketch, "E500", {"start": v(61453.74, 33) * mm, "end": v(61453.74, 533) * mm});
            skLineSegment(sketch, "E501", {"start": v(62023.74, 33) * mm, "end": v(62023.74, 833) * mm});
            skPoint(sketch, "E502.1.internal.snap0", {"position": v(62523.74, 312) * mm});
            skLineSegment(sketch, "E503", {"start": v(62255.14, 833) * mm, "end": v(62000, 833) * mm});
            skLineSegment(sketch, "E504", {"start": v(62255.14, 833) * mm, "end": v(63023.74, 833) * mm});
            skLineSegment(sketch, "E505", {"start": v(62198.44, 33) * mm, "end": v(63023.74, 33) * mm});
            skLineSegment(sketch, "E506", {"start": v(62198.44, 33) * mm, "end": v(62023.74, 33) * mm});
            skLineSegment(sketch, "E507", {"start": v(62023.74, 533) * mm, "end": v(62453.74, 533) * mm});
            skLineSegment(sketch, "E508", {"start": v(62453.74, 33) * mm, "end": v(62453.74, 533) * mm});
            skLineSegment(sketch, "E509", {"start": v(63023.74, 33) * mm, "end": v(63023.74, 833) * mm});
            skPoint(sketch, "E510.1.internal.snap0", {"position": v(63523.74, 312) * mm});
            skLineSegment(sketch, "E511", {"start": v(63255.14, 833) * mm, "end": v(63000, 833) * mm});
            skLineSegment(sketch, "E512", {"start": v(63255.14, 833) * mm, "end": v(64023.74, 833) * mm});
            skLineSegment(sketch, "E513", {"start": v(63198.44, 33) * mm, "end": v(64023.74, 33) * mm});
            skLineSegment(sketch, "E514", {"start": v(63198.44, 33) * mm, "end": v(63023.74, 33) * mm});
            skLineSegment(sketch, "E515", {"start": v(63023.74, 533) * mm, "end": v(63453.74, 533) * mm});
            skLineSegment(sketch, "E516", {"start": v(63453.74, 33) * mm, "end": v(63453.74, 533) * mm});
            skLineSegment(sketch, "E517", {"start": v(64023.74, 33) * mm, "end": v(64023.74, 833) * mm});
            skPoint(sketch, "E518.1.internal.snap0", {"position": v(64523.74, 312) * mm});
            skLineSegment(sketch, "E519", {"start": v(64255.14, 833) * mm, "end": v(64000, 833) * mm});
            skLineSegment(sketch, "E520", {"start": v(64255.14, 833) * mm, "end": v(65023.74, 833) * mm});
            skLineSegment(sketch, "E521", {"start": v(64198.44, 33) * mm, "end": v(65023.74, 33) * mm});
            skLineSegment(sketch, "E522", {"start": v(64198.44, 33) * mm, "end": v(64023.74, 33) * mm});
            skLineSegment(sketch, "E523", {"start": v(64023.74, 533) * mm, "end": v(64453.74, 533) * mm});
            skLineSegment(sketch, "E524", {"start": v(64453.74, 33) * mm, "end": v(64453.74, 533) * mm});
            skLineSegment(sketch, "E525", {"start": v(65023.74, 33) * mm, "end": v(65023.74, 833) * mm});
            skPoint(sketch, "E526.1.internal.snap0", {"position": v(65523.74, 312) * mm});
            skLineSegment(sketch, "E527", {"start": v(65255.14, 833) * mm, "end": v(65000, 833) * mm});
            skLineSegment(sketch, "E528", {"start": v(65255.14, 833) * mm, "end": v(66023.74, 833) * mm});
            skLineSegment(sketch, "E529", {"start": v(65198.44, 33) * mm, "end": v(66023.74, 33) * mm});
            skLineSegment(sketch, "E530", {"start": v(65198.44, 33) * mm, "end": v(65023.74, 33) * mm});
            skLineSegment(sketch, "E531", {"start": v(65023.74, 533) * mm, "end": v(65453.74, 533) * mm});
            skLineSegment(sketch, "E532", {"start": v(65453.74, 33) * mm, "end": v(65453.74, 533) * mm});
            skLineSegment(sketch, "E533", {"start": v(66023.74, 33) * mm, "end": v(66023.74, 833) * mm});
            skPoint(sketch, "E534.1.internal.snap0", {"position": v(66523.74, 312) * mm});
            skLineSegment(sketch, "E535", {"start": v(66255.14, 833) * mm, "end": v(66000, 833) * mm});
            skLineSegment(sketch, "E536", {"start": v(66255.14, 833) * mm, "end": v(67023.74, 833) * mm});
            skLineSegment(sketch, "E537", {"start": v(66198.44, 33) * mm, "end": v(67023.74, 33) * mm});
            skLineSegment(sketch, "E538", {"start": v(66198.44, 33) * mm, "end": v(66023.74, 33) * mm});
            skLineSegment(sketch, "E539", {"start": v(66023.74, 533) * mm, "end": v(66453.74, 533) * mm});
            skLineSegment(sketch, "E540", {"start": v(66453.74, 33) * mm, "end": v(66453.74, 533) * mm});
            skLineSegment(sketch, "E541", {"start": v(67023.74, 33) * mm, "end": v(67023.74, 833) * mm});
            skPoint(sketch, "E542.1.internal.snap0", {"position": v(67523.74, 312) * mm});
            skLineSegment(sketch, "E543", {"start": v(67255.14, 833) * mm, "end": v(67000, 833) * mm});
            skLineSegment(sketch, "E544", {"start": v(67255.14, 833) * mm, "end": v(68023.74, 833) * mm});
            skLineSegment(sketch, "E545", {"start": v(67198.44, 33) * mm, "end": v(68023.74, 33) * mm});
            skLineSegment(sketch, "E546", {"start": v(67198.44, 33) * mm, "end": v(67023.74, 33) * mm});
            skLineSegment(sketch, "E547", {"start": v(67023.74, 533) * mm, "end": v(67453.74, 533) * mm});
            skLineSegment(sketch, "E548", {"start": v(67453.74, 33) * mm, "end": v(67453.74, 533) * mm});
            skLineSegment(sketch, "E549", {"start": v(68023.74, 33) * mm, "end": v(68023.74, 833) * mm});
            skPoint(sketch, "E550.1.internal.snap0", {"position": v(68523.74, 312) * mm});
            skLineSegment(sketch, "E551", {"start": v(68255.14, 833) * mm, "end": v(68000, 833) * mm});
            skLineSegment(sketch, "E552", {"start": v(68255.14, 833) * mm, "end": v(69023.74, 833) * mm});
            skLineSegment(sketch, "E553", {"start": v(68198.44, 33) * mm, "end": v(69023.74, 33) * mm});
            skLineSegment(sketch, "E554", {"start": v(68198.44, 33) * mm, "end": v(68023.74, 33) * mm});
            skLineSegment(sketch, "E555", {"start": v(68023.74, 533) * mm, "end": v(68453.74, 533) * mm});
            skLineSegment(sketch, "E556", {"start": v(68453.74, 33) * mm, "end": v(68453.74, 533) * mm});
            skLineSegment(sketch, "E557", {"start": v(69023.74, 33) * mm, "end": v(69023.74, 833) * mm});
            skPoint(sketch, "E558.1.internal.snap0", {"position": v(69523.74, 312) * mm});
            skLineSegment(sketch, "E559", {"start": v(69255.14, 833) * mm, "end": v(69000, 833) * mm});
            skLineSegment(sketch, "E560", {"start": v(69255.14, 833) * mm, "end": v(70023.74, 833) * mm});
            skLineSegment(sketch, "E561", {"start": v(69198.44, 33) * mm, "end": v(70023.74, 33) * mm});
            skLineSegment(sketch, "E562", {"start": v(69198.44, 33) * mm, "end": v(69023.74, 33) * mm});
            skLineSegment(sketch, "E563", {"start": v(69023.74, 533) * mm, "end": v(69453.74, 533) * mm});
            skLineSegment(sketch, "E564", {"start": v(69453.74, 33) * mm, "end": v(69453.74, 533) * mm});
            skLineSegment(sketch, "E565", {"start": v(70023.74, 33) * mm, "end": v(70023.74, 833) * mm});
            skPoint(sketch, "E566.1.internal.snap0", {"position": v(70523.74, 312) * mm});
            skLineSegment(sketch, "E567", {"start": v(70255.14, 833) * mm, "end": v(70000, 833) * mm});
            skLineSegment(sketch, "E568", {"start": v(70255.14, 833) * mm, "end": v(71023.74, 833) * mm});
            skLineSegment(sketch, "E569", {"start": v(70198.44, 33) * mm, "end": v(71023.74, 33) * mm});
            skLineSegment(sketch, "E570", {"start": v(70198.44, 33) * mm, "end": v(70023.74, 33) * mm});
            skLineSegment(sketch, "E571", {"start": v(70023.74, 533) * mm, "end": v(70453.74, 533) * mm});
            skLineSegment(sketch, "E572", {"start": v(70453.74, 33) * mm, "end": v(70453.74, 533) * mm});
            skLineSegment(sketch, "E573", {"start": v(71023.74, 33) * mm, "end": v(71023.74, 833) * mm});
            skPoint(sketch, "E574.1.internal.snap0", {"position": v(71523.74, 312) * mm});
            skLineSegment(sketch, "E575", {"start": v(71255.14, 833) * mm, "end": v(71000, 833) * mm});
            skLineSegment(sketch, "E576", {"start": v(71255.14, 833) * mm, "end": v(72023.74, 833) * mm});
            skLineSegment(sketch, "E577", {"start": v(71198.44, 33) * mm, "end": v(72023.74, 33) * mm});
            skLineSegment(sketch, "E578", {"start": v(71198.44, 33) * mm, "end": v(71023.74, 33) * mm});
            skLineSegment(sketch, "E579", {"start": v(71023.74, 533) * mm, "end": v(71453.74, 533) * mm});
            skLineSegment(sketch, "E580", {"start": v(71453.74, 33) * mm, "end": v(71453.74, 533) * mm});
            skLineSegment(sketch, "E581", {"start": v(72023.74, 33) * mm, "end": v(72023.74, 833) * mm});
            skLineSegment(sketch, "E582", {"start": v(72023.74, 0) * mm, "end": v(72023.74, 833) * mm});
            skPoint(sketch, "E583.1.internal.snap0", {"position": v(72523.74, 312) * mm});
            skLineSegment(sketch, "E584", {"start": v(72255.14, 833) * mm, "end": v(72000, 833) * mm});
            skLineSegment(sketch, "E585", {"start": v(72255.14, 833) * mm, "end": v(73023.74, 833) * mm});
            skLineSegment(sketch, "E586", {"start": v(72198.44, 33) * mm, "end": v(73023.74, 33) * mm});
            skLineSegment(sketch, "E587", {"start": v(72198.44, 33) * mm, "end": v(72023.74, 33) * mm});
            skLineSegment(sketch, "E588", {"start": v(72023.74, 533) * mm, "end": v(72453.74, 533) * mm});
            skLineSegment(sketch, "E589", {"start": v(72453.74, 33) * mm, "end": v(72453.74, 533) * mm});
            skLineSegment(sketch, "E590", {"start": v(73023.74, 33) * mm, "end": v(73023.74, 833) * mm});
            skPoint(sketch, "E591.1.internal.snap0", {"position": v(73523.74, 312) * mm});
            skLineSegment(sketch, "E592", {"start": v(73255.14, 833) * mm, "end": v(73000, 833) * mm});
            skLineSegment(sketch, "E593", {"start": v(73255.14, 833) * mm, "end": v(74023.74, 833) * mm});
            skLineSegment(sketch, "E594", {"start": v(73198.44, 33) * mm, "end": v(74023.74, 33) * mm});
            skLineSegment(sketch, "E595", {"start": v(73198.44, 33) * mm, "end": v(73023.74, 33) * mm});
            skLineSegment(sketch, "E596", {"start": v(73023.74, 533) * mm, "end": v(73453.74, 533) * mm});
            skLineSegment(sketch, "E597", {"start": v(73453.74, 33) * mm, "end": v(73453.74, 533) * mm});
            skLineSegment(sketch, "E598", {"start": v(74023.74, 33) * mm, "end": v(74023.74, 833) * mm});
            skPoint(sketch, "E599.1.internal.snap0", {"position": v(74523.74, 312) * mm});
            skLineSegment(sketch, "E600", {"start": v(74255.14, 833) * mm, "end": v(74000, 833) * mm});
            skLineSegment(sketch, "E601", {"start": v(74255.14, 833) * mm, "end": v(75023.74, 833) * mm});
            skLineSegment(sketch, "E602", {"start": v(74198.44, 33) * mm, "end": v(75023.74, 33) * mm});
            skLineSegment(sketch, "E603", {"start": v(74198.44, 33) * mm, "end": v(74023.74, 33) * mm});
            skLineSegment(sketch, "E604", {"start": v(74023.74, 533) * mm, "end": v(74453.74, 533) * mm});
            skLineSegment(sketch, "E605", {"start": v(74453.74, 33) * mm, "end": v(74453.74, 533) * mm});
            skLineSegment(sketch, "E606", {"start": v(75023.74, 33) * mm, "end": v(75023.74, 833) * mm});
            skPoint(sketch, "E607.1.internal.snap0", {"position": v(75523.74, 312) * mm});
            skLineSegment(sketch, "E608", {"start": v(75255.14, 833) * mm, "end": v(75000, 833) * mm});
            skLineSegment(sketch, "E609", {"start": v(75255.14, 833) * mm, "end": v(76023.74, 833) * mm});
            skLineSegment(sketch, "E610", {"start": v(75198.44, 33) * mm, "end": v(76023.74, 33) * mm});
            skLineSegment(sketch, "E611", {"start": v(75198.44, 33) * mm, "end": v(75023.74, 33) * mm});
            skLineSegment(sketch, "E612", {"start": v(75023.74, 533) * mm, "end": v(75453.74, 533) * mm});
            skLineSegment(sketch, "E613", {"start": v(75453.74, 33) * mm, "end": v(75453.74, 533) * mm});
            skLineSegment(sketch, "E614", {"start": v(76023.74, 33) * mm, "end": v(76023.74, 833) * mm});
            skPoint(sketch, "E615.1.internal.snap0", {"position": v(76523.74, 312) * mm});
            skLineSegment(sketch, "E616", {"start": v(76255.14, 833) * mm, "end": v(76000, 833) * mm});
            skLineSegment(sketch, "E617", {"start": v(76255.14, 833) * mm, "end": v(77023.74, 833) * mm});
            skLineSegment(sketch, "E618", {"start": v(76198.44, 33) * mm, "end": v(77023.74, 33) * mm});
            skLineSegment(sketch, "E619", {"start": v(76198.44, 33) * mm, "end": v(76023.74, 33) * mm});
            skLineSegment(sketch, "E620", {"start": v(76023.74, 533) * mm, "end": v(76453.74, 533) * mm});
            skLineSegment(sketch, "E621", {"start": v(76453.74, 33) * mm, "end": v(76453.74, 533) * mm});
            skLineSegment(sketch, "E622", {"start": v(77023.74, 33) * mm, "end": v(77023.74, 833) * mm});
            skPoint(sketch, "E623.1.internal.snap0", {"position": v(77523.74, 312) * mm});
            skLineSegment(sketch, "E624", {"start": v(77255.14, 833) * mm, "end": v(77000, 833) * mm});
            skLineSegment(sketch, "E625", {"start": v(77255.14, 833) * mm, "end": v(78023.74, 833) * mm});
            skLineSegment(sketch, "E626", {"start": v(77198.44, 33) * mm, "end": v(78023.74, 33) * mm});
            skLineSegment(sketch, "E627", {"start": v(77198.44, 33) * mm, "end": v(77023.74, 33) * mm});
            skLineSegment(sketch, "E628", {"start": v(77023.74, 533) * mm, "end": v(77453.74, 533) * mm});
            skLineSegment(sketch, "E629", {"start": v(77453.74, 33) * mm, "end": v(77453.74, 533) * mm});
            skLineSegment(sketch, "E630", {"start": v(78023.74, 33) * mm, "end": v(78023.74, 833) * mm});
            skPoint(sketch, "E631.1.internal.snap0", {"position": v(78523.74, 312) * mm});
            skLineSegment(sketch, "E632", {"start": v(78255.14, 833) * mm, "end": v(78000, 833) * mm});
            skLineSegment(sketch, "E633", {"start": v(78255.14, 833) * mm, "end": v(79023.74, 833) * mm});
            skLineSegment(sketch, "E634", {"start": v(78198.44, 33) * mm, "end": v(79023.74, 33) * mm});
            skLineSegment(sketch, "E635", {"start": v(78198.44, 33) * mm, "end": v(78023.74, 33) * mm});
            skLineSegment(sketch, "E636", {"start": v(78023.74, 533) * mm, "end": v(78453.74, 533) * mm});
            skLineSegment(sketch, "E637", {"start": v(78453.74, 33) * mm, "end": v(78453.74, 533) * mm});
            skLineSegment(sketch, "E638", {"start": v(79023.74, 33) * mm, "end": v(79023.74, 833) * mm});
            skPoint(sketch, "E639.1.internal.snap0", {"position": v(79523.74, 312) * mm});
            skLineSegment(sketch, "E640", {"start": v(79255.14, 833) * mm, "end": v(79000, 833) * mm});
            skLineSegment(sketch, "E641", {"start": v(79255.14, 833) * mm, "end": v(80023.74, 833) * mm});
            skLineSegment(sketch, "E642", {"start": v(79198.44, 33) * mm, "end": v(80023.74, 33) * mm});
            skLineSegment(sketch, "E643", {"start": v(79198.44, 33) * mm, "end": v(79023.74, 33) * mm});
            skLineSegment(sketch, "E644", {"start": v(79023.74, 533) * mm, "end": v(79453.74, 533) * mm});
            skLineSegment(sketch, "E645", {"start": v(79453.74, 33) * mm, "end": v(79453.74, 533) * mm});
            skLineSegment(sketch, "E646", {"start": v(80023.74, 33) * mm, "end": v(80023.74, 833) * mm});
            skPoint(sketch, "E647.1.internal.snap0", {"position": v(80523.74, 312) * mm});
            skLineSegment(sketch, "E648", {"start": v(80255.14, 833) * mm, "end": v(80000, 833) * mm});
            skLineSegment(sketch, "E649", {"start": v(80255.14, 833) * mm, "end": v(81023.74, 833) * mm});
            skLineSegment(sketch, "E650", {"start": v(80198.44, 33) * mm, "end": v(81023.74, 33) * mm});
            skLineSegment(sketch, "E651", {"start": v(80198.44, 33) * mm, "end": v(80023.74, 33) * mm});
            skLineSegment(sketch, "E652", {"start": v(80023.74, 533) * mm, "end": v(80453.74, 533) * mm});
            skLineSegment(sketch, "E653", {"start": v(80453.74, 33) * mm, "end": v(80453.74, 533) * mm});
            skLineSegment(sketch, "E654", {"start": v(81023.74, 33) * mm, "end": v(81023.74, 833) * mm});
            skPoint(sketch, "E655.1.internal.snap0", {"position": v(81523.74, 312) * mm});
            skLineSegment(sketch, "E656", {"start": v(81255.14, 833) * mm, "end": v(81000, 833) * mm});
            skLineSegment(sketch, "E657", {"start": v(81255.14, 833) * mm, "end": v(82023.74, 833) * mm});
            skLineSegment(sketch, "E658", {"start": v(81198.44, 33) * mm, "end": v(82023.74, 33) * mm});
            skLineSegment(sketch, "E659", {"start": v(81198.44, 33) * mm, "end": v(81023.74, 33) * mm});
            skLineSegment(sketch, "E660", {"start": v(81023.74, 533) * mm, "end": v(81453.74, 533) * mm});
            skLineSegment(sketch, "E661", {"start": v(81453.74, 33) * mm, "end": v(81453.74, 533) * mm});
            skLineSegment(sketch, "E662", {"start": v(82023.74, 33) * mm, "end": v(82023.74, 833) * mm});
            skPoint(sketch, "E663.1.internal.snap0", {"position": v(82523.74, 312) * mm});
            skLineSegment(sketch, "E664", {"start": v(82255.14, 833) * mm, "end": v(82000, 833) * mm});
            skLineSegment(sketch, "E665", {"start": v(82255.14, 833) * mm, "end": v(83023.74, 833) * mm});
            skLineSegment(sketch, "E666", {"start": v(82198.44, 33) * mm, "end": v(83023.74, 33) * mm});
            skLineSegment(sketch, "E667", {"start": v(82198.44, 33) * mm, "end": v(82023.74, 33) * mm});
            skLineSegment(sketch, "E668", {"start": v(82023.74, 533) * mm, "end": v(82453.74, 533) * mm});
            skLineSegment(sketch, "E669", {"start": v(82453.74, 33) * mm, "end": v(82453.74, 533) * mm});
            skLineSegment(sketch, "E670", {"start": v(83023.74, 33) * mm, "end": v(83023.74, 833) * mm});
            skPoint(sketch, "E671.1.internal.snap0", {"position": v(83523.74, 312) * mm});
            skLineSegment(sketch, "E672", {"start": v(83255.14, 833) * mm, "end": v(83000, 833) * mm});
            skLineSegment(sketch, "E673", {"start": v(83255.14, 833) * mm, "end": v(84023.74, 833) * mm});
            skLineSegment(sketch, "E674", {"start": v(83198.44, 33) * mm, "end": v(84023.74, 33) * mm});
            skLineSegment(sketch, "E675", {"start": v(83198.44, 33) * mm, "end": v(83023.74, 33) * mm});
            skLineSegment(sketch, "E676", {"start": v(83023.74, 533) * mm, "end": v(83453.74, 533) * mm});
            skLineSegment(sketch, "E677", {"start": v(83453.74, 33) * mm, "end": v(83453.74, 533) * mm});
            skLineSegment(sketch, "E678", {"start": v(84023.74, 33) * mm, "end": v(84023.74, 833) * mm});
            skPoint(sketch, "E679.1.internal.snap0", {"position": v(84523.74, 312) * mm});
            skLineSegment(sketch, "E680", {"start": v(84255.14, 833) * mm, "end": v(84000, 833) * mm});
            skLineSegment(sketch, "E681", {"start": v(84255.14, 833) * mm, "end": v(85023.74, 833) * mm});
            skLineSegment(sketch, "E682", {"start": v(84198.44, 33) * mm, "end": v(85023.74, 33) * mm});
            skLineSegment(sketch, "E683", {"start": v(84198.44, 33) * mm, "end": v(84023.74, 33) * mm});
            skLineSegment(sketch, "E684", {"start": v(84023.74, 533) * mm, "end": v(84453.74, 533) * mm});
            skLineSegment(sketch, "E685", {"start": v(84453.74, 33) * mm, "end": v(84453.74, 533) * mm});
            skLineSegment(sketch, "E686", {"start": v(85023.74, 33) * mm, "end": v(85023.74, 833) * mm});
            skPoint(sketch, "E687.1.internal.snap0", {"position": v(85523.74, 312) * mm});
            skLineSegment(sketch, "E688", {"start": v(85255.14, 833) * mm, "end": v(85000, 833) * mm});
            skLineSegment(sketch, "E689", {"start": v(85255.14, 833) * mm, "end": v(86023.74, 833) * mm});
            skLineSegment(sketch, "E690", {"start": v(85198.44, 33) * mm, "end": v(86023.74, 33) * mm});
            skLineSegment(sketch, "E691", {"start": v(85198.44, 33) * mm, "end": v(85023.74, 33) * mm});
            skLineSegment(sketch, "E692", {"start": v(85023.74, 533) * mm, "end": v(85453.74, 533) * mm});
            skLineSegment(sketch, "E693", {"start": v(85453.74, 33) * mm, "end": v(85453.74, 533) * mm});
            skLineSegment(sketch, "E694", {"start": v(86023.74, 33) * mm, "end": v(86023.74, 833) * mm});
            skPoint(sketch, "E695.1.internal.snap0", {"position": v(86523.74, 312) * mm});
            skLineSegment(sketch, "E696", {"start": v(86255.14, 833) * mm, "end": v(86000, 833) * mm});
            skLineSegment(sketch, "E697", {"start": v(86255.14, 833) * mm, "end": v(87023.74, 833) * mm});
            skLineSegment(sketch, "E698", {"start": v(86198.44, 33) * mm, "end": v(87023.74, 33) * mm});
            skLineSegment(sketch, "E699", {"start": v(86198.44, 33) * mm, "end": v(86023.74, 33) * mm});
            skLineSegment(sketch, "E700", {"start": v(86023.74, 533) * mm, "end": v(86453.74, 533) * mm});
            skLineSegment(sketch, "E701", {"start": v(86453.74, 33) * mm, "end": v(86453.74, 533) * mm});
            skLineSegment(sketch, "E702", {"start": v(87023.74, 33) * mm, "end": v(87023.74, 833) * mm});
            skPoint(sketch, "E703.1.internal.snap0", {"position": v(87523.74, 312) * mm});
            skLineSegment(sketch, "E704", {"start": v(87255.14, 833) * mm, "end": v(87000, 833) * mm});
            skLineSegment(sketch, "E705", {"start": v(87255.14, 833) * mm, "end": v(88023.74, 833) * mm});
            skLineSegment(sketch, "E706", {"start": v(87198.44, 33) * mm, "end": v(88023.74, 33) * mm});
            skLineSegment(sketch, "E707", {"start": v(87198.44, 33) * mm, "end": v(87023.74, 33) * mm});
            skLineSegment(sketch, "E708", {"start": v(87023.74, 533) * mm, "end": v(87453.74, 533) * mm});
            skLineSegment(sketch, "E709", {"start": v(87453.74, 33) * mm, "end": v(87453.74, 533) * mm});
            skLineSegment(sketch, "E710", {"start": v(88023.74, 33) * mm, "end": v(88023.74, 833) * mm});
            skPoint(sketch, "E711.1.internal.snap0", {"position": v(88523.74, 312) * mm});
            skLineSegment(sketch, "E712", {"start": v(88255.14, 833) * mm, "end": v(88000, 833) * mm});
            skLineSegment(sketch, "E713", {"start": v(88255.14, 833) * mm, "end": v(89023.74, 833) * mm});
            skLineSegment(sketch, "E714", {"start": v(88198.44, 33) * mm, "end": v(89023.74, 33) * mm});
            skLineSegment(sketch, "E715", {"start": v(88198.44, 33) * mm, "end": v(88023.74, 33) * mm});
            skLineSegment(sketch, "E716", {"start": v(88023.74, 533) * mm, "end": v(88453.74, 533) * mm});
            skLineSegment(sketch, "E717", {"start": v(88453.74, 33) * mm, "end": v(88453.74, 533) * mm});
            skLineSegment(sketch, "E718", {"start": v(89023.74, 33) * mm, "end": v(89023.74, 833) * mm});
            skPoint(sketch, "E719.1.internal.snap0", {"position": v(89523.74, 312) * mm});
            skLineSegment(sketch, "E720", {"start": v(89255.14, 833) * mm, "end": v(89000, 833) * mm});
            skLineSegment(sketch, "E721", {"start": v(89255.14, 833) * mm, "end": v(90023.74, 833) * mm});
            skLineSegment(sketch, "E722", {"start": v(89198.44, 33) * mm, "end": v(90023.74, 33) * mm});
            skLineSegment(sketch, "E723", {"start": v(89198.44, 33) * mm, "end": v(89023.74, 33) * mm});
            skLineSegment(sketch, "E724", {"start": v(89023.74, 533) * mm, "end": v(89453.74, 533) * mm});
            skLineSegment(sketch, "E725", {"start": v(89453.74, 33) * mm, "end": v(89453.74, 533) * mm});
            skLineSegment(sketch, "E726", {"start": v(90023.74, 33) * mm, "end": v(90023.74, 833) * mm});
            skFitSpline(sketch, "E727", {"points": [v(23.74, 33) * mm, v(453.74, 533) * mm, v(1023.74, 33) * mm, v(1453.74, 533) * mm, v(2023.74, 33) * mm, v(2453.74, 533) * mm, v(3023.74, 33) * mm, v(3453.74, 533) * mm, v(4023.74, 33) * mm, v(4453.74, 533) * mm, v(5023.74, 33) * mm, v(5453.74, 533) * mm, v(6023.74, 33) * mm, v(6453.74, 533) * mm, v(7023.74, 33) * mm, v(7453.74, 533) * mm, v(8023.74, 33) * mm, v(8453.74, 533) * mm, v(9023.74, 33) * mm, v(9453.74, 533) * mm, v(10023.74, 33) * mm, v(10453.74, 533) * mm, v(11023.74, 33) * mm, v(11453.74, 533) * mm, v(12023.74, 33) * mm, v(12453.74, 533) * mm, v(13023.74, 33) * mm, v(13453.74, 533) * mm, v(14023.74, 33) * mm, v(14453.74, 533) * mm, v(15023.74, 33) * mm, v(15453.74, 533) * mm, v(16023.74, 33) * mm, v(16453.74, 533) * mm, v(17023.74, 33) * mm, v(17453.74, 533) * mm, v(18023.74, 33) * mm, v(18453.74, 533) * mm, v(19023.74, 33) * mm, v(19453.74, 533) * mm, v(20023.74, 33) * mm, v(20453.74, 533) * mm, v(21023.74, 33) * mm, v(21453.74, 533) * mm, v(22023.74, 33) * mm, v(22453.74, 533) * mm, v(23023.74, 33) * mm, v(23453.74, 533) * mm, v(24023.74, 33) * mm, v(24453.74, 533) * mm, v(25023.74, 33) * mm, v(25453.74, 533) * mm, v(26023.74, 33) * mm, v(26453.74, 533) * mm, v(27023.74, 33) * mm, v(27453.74, 533) * mm, v(28023.74, 33) * mm, v(28453.74, 533) * mm, v(29023.74, 33) * mm, v(29453.74, 533) * mm, v(30023.74, 33) * mm, v(30453.74, 533) * mm, v(31023.74, 33) * mm, v(31453.74, 533) * mm, v(32023.74, 33) * mm, v(32453.74, 533) * mm, v(33023.74, 33) * mm, v(33453.74, 533) * mm, v(34023.74, 33) * mm, v(34453.74, 533) * mm, v(35023.74, 33) * mm, v(35453.74, 533) * mm, v(36023.74, 33) * mm, v(36453.74, 533) * mm, v(37023.74, 33) * mm, v(37453.74, 533) * mm, v(38023.74, 33) * mm, v(38453.74, 533) * mm, v(39023.74, 33) * mm, v(39453.74, 533) * mm, v(40023.74, 33) * mm, v(40453.74, 533) * mm, v(41023.74, 33) * mm, v(41453.74, 533) * mm, v(42023.74, 33) * mm, v(42453.74, 533) * mm, v(43023.74, 33) * mm, v(43453.74, 533) * mm, v(44023.74, 33) * mm, v(44453.74, 533) * mm, v(45023.74, 33) * mm, v(45453.74, 533) * mm, v(46023.74, 33) * mm, v(46453.74, 533) * mm, v(47023.74, 33) * mm, v(47453.74, 533) * mm, v(48023.74, 33) * mm, v(48453.74, 533) * mm, v(49023.74, 33) * mm, v(49453.74, 533) * mm, v(50023.74, 33) * mm, v(50453.74, 533) * mm, v(51023.74, 33) * mm, v(51453.74, 533) * mm, v(52023.74, 33) * mm, v(52453.74, 533) * mm, v(53023.74, 33) * mm, v(53453.74, 533) * mm, v(54023.74, 33) * mm, v(54453.74, 533) * mm, v(55023.74, 33) * mm, v(55453.74, 533) * mm, v(56023.74, 33) * mm, v(56453.74, 533) * mm, v(57023.74, 33) * mm, v(57453.74, 533) * mm, v(58023.74, 33) * mm, v(58453.74, 533) * mm, v(59023.74, 33) * mm, v(59453.74, 533) * mm, v(60023.74, 33) * mm, v(60453.74, 533) * mm, v(61023.74, 33) * mm, v(61453.74, 533) * mm, v(62023.74, 33) * mm, v(62453.74, 533) * mm, v(63023.74, 33) * mm, v(63453.74, 533) * mm, v(64023.74, 33) * mm, v(64453.74, 533) * mm, v(65023.74, 33) * mm, v(65453.74, 533) * mm, v(66023.74, 33) * mm, v(66453.74, 533) * mm, v(67023.74, 33) * mm, v(67453.74, 533) * mm, v(68023.74, 33) * mm, v(68453.74, 533) * mm, v(69023.74, 33) * mm, v(69453.74, 533) * mm, v(70023.74, 33) * mm, v(70453.74, 533) * mm, v(71023.74, 33) * mm, v(71453.74, 533) * mm, v(72023.74, 33) * mm, v(72453.74, 533) * mm, v(73023.74, 33) * mm, v(73453.74, 533) * mm, v(74023.74, 33) * mm, v(74453.74, 533) * mm, v(75023.74, 33) * mm, v(75453.74, 533) * mm, v(76023.74, 33) * mm, v(76453.74, 533) * mm, v(77023.74, 33) * mm, v(77453.74, 533) * mm, v(78023.74, 33) * mm, v(78453.74, 533) * mm, v(79023.74, 33) * mm, v(79453.74, 533) * mm, v(80023.74, 33) * mm, v(80453.74, 533) * mm, v(81023.74, 33) * mm, v(81453.74, 533) * mm, v(82023.74, 33) * mm, v(82453.74, 533) * mm, v(83023.74, 33) * mm, v(83453.74, 533) * mm, v(84023.74, 33) * mm, v(84453.74, 533) * mm, v(85023.74, 33) * mm, v(85453.74, 533) * mm, v(86023.74, 33) * mm, v(86453.74, 533) * mm, v(87023.74, 33) * mm, v(87453.74, 533) * mm, v(88023.74, 33) * mm, v(88453.74, 533) * mm, v(89023.74, 33) * mm, v(89453.74, 533) * mm, v(90023.74, 33) * mm], "startDerivative": vector(73429.36, 157621.73) * mm, "endDerivative": vector(106240.3, -154479.53) * mm});
            skLineSegment(sketch, "E728", {"start": v(147.4, 2500) * mm, "end": v(147.4, 2467) * mm});
            skLineSegment(sketch, "E729", {"start": v(147.4, 2467) * mm, "end": v(23.74, 2467) * mm});
            skLineSegment(sketch, "E730", {"start": v(147.4, 2467) * mm, "end": v(1042.87, 2467) * mm});
            skFitSpline(sketch, "E731", {"points": [v(27.9, 1960) * mm, v(457.9, 2460) * mm, v(1027.9, 1960) * mm, v(1457.9, 2460) * mm, v(2027.9, 1960) * mm, v(2457.9, 2460) * mm, v(3027.9, 1960) * mm, v(3457.9, 2460) * mm, v(4027.9, 1960) * mm, v(4457.9, 2460) * mm, v(5027.9, 1960) * mm, v(5457.9, 2460) * mm, v(6027.9, 1960) * mm, v(6457.9, 2460) * mm, v(7027.9, 1960) * mm, v(7457.9, 2460) * mm, v(8027.9, 1960) * mm, v(8457.9, 2460) * mm, v(9027.9, 1960) * mm, v(9457.9, 2460) * mm, v(10027.9, 1960) * mm, v(10457.9, 2460) * mm, v(11027.9, 1960) * mm, v(11457.9, 2460) * mm, v(12027.9, 1960) * mm, v(12457.9, 2460) * mm, v(13027.9, 1960) * mm, v(13457.9, 2460) * mm, v(14027.9, 1960) * mm, v(14457.9, 2460) * mm, v(15027.9, 1960) * mm, v(15457.9, 2460) * mm, v(16027.9, 1960) * mm, v(16457.9, 2460) * mm, v(17027.9, 1960) * mm, v(17457.9, 2460) * mm, v(18027.9, 1960) * mm, v(18457.9, 2460) * mm, v(19027.9, 1960) * mm, v(19457.9, 2460) * mm, v(20027.9, 1960) * mm, v(20457.9, 2460) * mm, v(21027.9, 1960) * mm, v(21457.9, 2460) * mm, v(22027.9, 1960) * mm, v(22457.9, 2460) * mm, v(23027.9, 1960) * mm, v(23457.9, 2460) * mm, v(24027.9, 1960) * mm, v(24457.9, 2460) * mm, v(25027.9, 1960) * mm, v(25457.9, 2460) * mm, v(26027.9, 1960) * mm, v(26457.9, 2460) * mm, v(27027.9, 1960) * mm, v(27457.9, 2460) * mm, v(28027.9, 1960) * mm, v(28457.9, 2460) * mm, v(29027.9, 1960) * mm, v(29457.9, 2460) * mm, v(30027.9, 1960) * mm, v(30457.9, 2460) * mm, v(31027.9, 1960) * mm, v(31457.9, 2460) * mm, v(32027.9, 1960) * mm, v(32457.9, 2460) * mm, v(33027.9, 1960) * mm, v(33457.9, 2460) * mm, v(34027.9, 1960) * mm, v(34457.9, 2460) * mm, v(35027.9, 1960) * mm, v(35457.9, 2460) * mm, v(36027.9, 1960) * mm, v(36457.9, 2460) * mm, v(37027.9, 1960) * mm, v(37457.9, 2460) * mm, v(38027.9, 1960) * mm, v(38457.9, 2460) * mm, v(39027.9, 1960) * mm, v(39457.9, 2460) * mm, v(40027.9, 1960) * mm, v(40457.9, 2460) * mm, v(41027.9, 1960) * mm, v(41457.9, 2460) * mm, v(42027.9, 1960) * mm, v(42457.9, 2460) * mm, v(43027.9, 1960) * mm, v(43457.9, 2460) * mm, v(44027.9, 1960) * mm, v(44457.9, 2460) * mm, v(45027.9, 1960) * mm, v(45457.9, 2460) * mm, v(46027.9, 1960) * mm, v(46457.9, 2460) * mm, v(47027.9, 1960) * mm, v(47457.9, 2460) * mm, v(48027.9, 1960) * mm, v(48457.9, 2460) * mm, v(49027.9, 1960) * mm, v(49457.9, 2460) * mm, v(50027.9, 1960) * mm, v(50457.9, 2460) * mm, v(51027.9, 1960) * mm, v(51457.9, 2460) * mm, v(52027.9, 1960) * mm, v(52457.9, 2460) * mm, v(53027.9, 1960) * mm, v(53457.9, 2460) * mm, v(54027.9, 1960) * mm, v(54457.9, 2460) * mm, v(55027.9, 1960) * mm, v(55457.9, 2460) * mm, v(56027.9, 1960) * mm, v(56457.9, 2460) * mm, v(57027.9, 1960) * mm, v(57457.9, 2460) * mm, v(58027.9, 1960) * mm, v(58457.9, 2460) * mm, v(59027.9, 1960) * mm, v(59457.9, 2460) * mm, v(60027.9, 1960) * mm, v(60457.9, 2460) * mm, v(61027.9, 1960) * mm, v(61457.9, 2460) * mm, v(62027.9, 1960) * mm, v(62457.9, 2460) * mm, v(63027.9, 1960) * mm, v(63457.9, 2460) * mm, v(64027.9, 1960) * mm, v(64457.9, 2460) * mm, v(65027.9, 1960) * mm, v(65457.9, 2460) * mm, v(66027.9, 1960) * mm, v(66457.9, 2460) * mm, v(67027.9, 1960) * mm, v(67457.9, 2460) * mm, v(68027.9, 1960) * mm, v(68457.9, 2460) * mm, v(69027.9, 1960) * mm, v(69457.9, 2460) * mm, v(70027.9, 1960) * mm, v(70457.9, 2460) * mm, v(71027.9, 1960) * mm, v(71457.9, 2460) * mm, v(72027.9, 1960) * mm, v(72457.9, 2460) * mm, v(73027.9, 1960) * mm, v(73457.9, 2460) * mm, v(74027.9, 1960) * mm, v(74457.9, 2460) * mm, v(75027.9, 1960) * mm, v(75457.9, 2460) * mm, v(76027.9, 1960) * mm, v(76457.9, 2460) * mm, v(77027.9, 1960) * mm, v(77457.9, 2460) * mm, v(78027.9, 1960) * mm, v(78457.9, 2460) * mm, v(79027.9, 1960) * mm, v(79457.9, 2460) * mm, v(80027.9, 1960) * mm, v(80457.9, 2460) * mm, v(81027.9, 1960) * mm, v(81457.9, 2460) * mm, v(82027.9, 1960) * mm, v(82457.9, 2460) * mm, v(83027.9, 1960) * mm, v(83457.9, 2460) * mm, v(84027.9, 1960) * mm, v(84457.9, 2460) * mm, v(85027.9, 1960) * mm, v(85457.9, 2460) * mm, v(86027.9, 1960) * mm, v(86457.9, 2460) * mm, v(87027.9, 1960) * mm, v(87457.9, 2460) * mm, v(88027.9, 1960) * mm, v(88457.9, 2460) * mm, v(89027.9, 1960) * mm, v(89457.9, 2460) * mm, v(90027.9, 1960) * mm], "startDerivative": vector(73429.36, 157621.73) * mm, "endDerivative": vector(106240.3, -154479.53) * mm});
            skSolve(sketch);
        }
        {
            var Q0;
            {var subQ104=sQuery(id+"F4.wireOp",EDGE,"E11");Q0=makeQuery(id+"F4.imprint","IMPRINT",FACE,{"disambiguationData":[TD([[makeQuery(id+"F4.imprint","IMPRINT",EDGE,{"derivedFrom":subQ104}),1.0]])]});}
            extrude(context, id + "F5", {"entities" : qUnion([Q0]), "operationType" : NewBodyOperationType.REMOVE, "oppositeDirection" : true, "depth" : 50 * mm});
        }
        {
            var Q0;
            Q0=makeQuery(id+"F1.opExtrude","CAP_FACE",FACE,{"disambiguationData":[OSD([sQuery(id+"F0.wireOp",EDGE,"E0.bottom"),sQuery(id+"F0.wireOp",EDGE,"E0.top"),sQuery(id+"F0.wireOp",EDGE,"E0.left"),sQuery(id+"F0.wireOp",EDGE,"E0.right")])],"isStart":false});
            var sketch = newSketch(context, id + "F6", { "sketchPlane" : qUnion([Q0])});
            skPoint(sketch, "E732.endSnap0", {"position": v(-23.74, 1042.27) * mm});
            skCircle(sketch, "E733", {"center": v(-10023.74, 1042.27) * mm, "radius": 750 * mm});
            skCircle(sketch, "E734", {"center": v(-20023.74, 1042.27) * mm, "radius": 750 * mm});
            skCircle(sketch, "E735", {"center": v(-30023.74, 1042.27) * mm, "radius": 750 * mm});
            skCircle(sketch, "E736", {"center": v(-40023.74, 1042.27) * mm, "radius": 750 * mm});
            skCircle(sketch, "E737", {"center": v(-50023.74, 1042.27) * mm, "radius": 750 * mm});
            skCircle(sketch, "E738", {"center": v(-60023.74, 1042.27) * mm, "radius": 750 * mm});
            skCircle(sketch, "E739", {"center": v(-70023.74, 1042.27) * mm, "radius": 750 * mm});
            skCircle(sketch, "E740", {"center": v(-80023.74, 1042.27) * mm, "radius": 750 * mm});
            skLineSegment(sketch, "E741", {"start": v(-90023.74, 1042.27) * mm, "end": v(-88023.74, 1042.27) * mm});
            skCircle(sketch, "E742", {"center": v(-88023.74, 1042.27) * mm, "radius": 2000 * mm});
            skSolve(sketch);
        }
        {
            var Q0;
            Q0=makeQuery(id+"F6.imprint","IMPRINT",FACE,{"disambiguationData":[TD([[makeQuery(id+"F6.imprint","IMPRINT",EDGE,{"derivedFrom":sQuery(id+"F6.wireOp",EDGE,"E733")}),1.0]])]});
            extrude(context, id + "F7", {"entities" : qUnion([Q0]), "operationType" : NewBodyOperationType.REMOVE, "oppositeDirection" : true, "depth" : 50 * mm});
        }
        {
            var Q0;
            Q0=makeQuery(id+"F6.imprint","IMPRINT",FACE,{"disambiguationData":[TD([[makeQuery(id+"F6.imprint","IMPRINT",EDGE,{"derivedFrom":sQuery(id+"F6.wireOp",EDGE,"E734")}),1.0]])]});
            extrude(context, id + "F8", {"entities" : qUnion([Q0]), "operationType" : NewBodyOperationType.REMOVE, "oppositeDirection" : true, "depth" : 50 * mm});
        }
        {
            var Q0;
            Q0=makeQuery(id+"F6.imprint","IMPRINT",FACE,{"disambiguationData":[TD([[makeQuery(id+"F6.imprint","IMPRINT",EDGE,{"derivedFrom":sQuery(id+"F6.wireOp",EDGE,"E735")}),1.0]])]});
            extrude(context, id + "F9", {"entities" : qUnion([Q0]), "operationType" : NewBodyOperationType.REMOVE, "oppositeDirection" : true, "depth" : 50 * mm});
        }
        {
            var Q0;
            Q0=makeQuery(id+"F6.imprint","IMPRINT",FACE,{"disambiguationData":[TD([[makeQuery(id+"F6.imprint","IMPRINT",EDGE,{"derivedFrom":sQuery(id+"F6.wireOp",EDGE,"E736")}),1.0]])]});
            extrude(context, id + "F10", {"entities" : qUnion([Q0]), "operationType" : NewBodyOperationType.REMOVE, "oppositeDirection" : true, "depth" : 50 * mm});
        }
        {
            var Q0;
            Q0=makeQuery(id+"F6.imprint","IMPRINT",FACE,{"disambiguationData":[TD([[makeQuery(id+"F6.imprint","IMPRINT",EDGE,{"derivedFrom":sQuery(id+"F6.wireOp",EDGE,"E737")}),1.0]])]});
            extrude(context, id + "F11", {"entities" : qUnion([Q0]), "operationType" : NewBodyOperationType.REMOVE, "oppositeDirection" : true, "depth" : 50 * mm});
        }
        {
            var Q0;
            Q0=makeQuery(id+"F6.imprint","IMPRINT",FACE,{"disambiguationData":[TD([[makeQuery(id+"F6.imprint","IMPRINT",EDGE,{"derivedFrom":sQuery(id+"F6.wireOp",EDGE,"E738")}),1.0]])]});
            extrude(context, id + "F12", {"entities" : qUnion([Q0]), "operationType" : NewBodyOperationType.REMOVE, "oppositeDirection" : true, "depth" : 50 * mm});
        }
        {
            var Q0;
            Q0=makeQuery(id+"F6.imprint","IMPRINT",FACE,{"disambiguationData":[TD([[makeQuery(id+"F6.imprint","IMPRINT",EDGE,{"derivedFrom":sQuery(id+"F6.wireOp",EDGE,"E739")}),1.0]])]});
            extrude(context, id + "F13", {"entities" : qUnion([Q0]), "operationType" : NewBodyOperationType.REMOVE, "oppositeDirection" : true, "depth" : 50 * mm});
        }
        {
            var Q0;
            Q0=makeQuery(id+"F6.imprint","IMPRINT",FACE,{"disambiguationData":[TD([[makeQuery(id+"F6.imprint","IMPRINT",EDGE,{"derivedFrom":sQuery(id+"F6.wireOp",EDGE,"E740")}),1.0]])]});
            extrude(context, id + "F14", {"entities" : qUnion([Q0]), "operationType" : NewBodyOperationType.REMOVE, "oppositeDirection" : true, "depth" : 50 * mm});
        }
        {
            var Q0;
            Q0=makeQuery(id+"F1.opExtrude","CAP_FACE",FACE,{"disambiguationData":[OSD([sQuery(id+"F0.wireOp",EDGE,"E0.bottom"),sQuery(id+"F0.wireOp",EDGE,"E0.top"),sQuery(id+"F0.wireOp",EDGE,"E0.left"),sQuery(id+"F0.wireOp",EDGE,"E0.right")])],"isStart":true});
            var sketch = newSketch(context, id + "F15", { "sketchPlane" : qUnion([Q0])});
            skPoint(sketch, "E743.endSnap0", {"position": v(-90023.74, -1042.27) * mm});
            skPoint(sketch, "E744.startSnap0", {"position": v(-23.74, -1042.27) * mm});
            skLineSegment(sketch, "E745", {"start": v(-88023.74, -1470.5) * mm, "end": v(-88023.74, -566.35) * mm});
            skCircle(sketch, "E746", {"center": v(-88023.74, -1042.27) * mm, "radius": 2000 * mm});
            skLineSegment(sketch, "E747", {"start": v(-76023.74, -1042.27) * mm, "end": v(-76023.74, -2042.27) * mm});
            skLineSegment(sketch, "E748", {"start": v(-76023.74, -1042.27) * mm, "end": v(-76023.74, -42.27) * mm});
            skLineSegment(sketch, "E749", {"start": v(-90023.74, -1042.27) * mm, "end": v(-76023.74, -1042.27) * mm});
            skCircle(sketch, "E750", {"center": v(-38023.74, -1042.27) * mm, "radius": 500 * mm});
            skCircle(sketch, "E751", {"center": v(-57023.74, -1042.27) * mm, "radius": 500 * mm});
            skCircle(sketch, "E752", {"center": v(-19023.74, -1042.27) * mm, "radius": 500 * mm});
            skCircle(sketch, "E753", {"center": v(-88023.74, -1042.27) * mm, "radius": 900 * mm});
            skSolve(sketch);
        }
        {
            var Q0;
            Q0=makeQuery(id+"F15.imprint","IMPRINT",FACE,{"disambiguationData":[TD([[makeQuery(id+"F15.imprint","IMPRINT",EDGE,{"derivedFrom":sQuery(id+"F15.wireOp",EDGE,"E751")}),1.0]])]});
            extrude(context, id + "F16", {"entities" : qUnion([Q0]), "operationType" : NewBodyOperationType.ADD, "depth" : 10000 * mm});
        }
        {
            var Q0;
            Q0=makeQuery(id+"F15.imprint","IMPRINT",FACE,{"disambiguationData":[TD([[makeQuery(id+"F15.imprint","IMPRINT",EDGE,{"derivedFrom":sQuery(id+"F15.wireOp",EDGE,"E750")}),1.0]])]});
            extrude(context, id + "F17", {"entities" : qUnion([Q0]), "operationType" : NewBodyOperationType.ADD, "depth" : 10000 * mm});
        }
        {
            var Q0;
            Q0=makeQuery(id+"F15.imprint","IMPRINT",FACE,{"disambiguationData":[TD([[makeQuery(id+"F15.imprint","IMPRINT",EDGE,{"derivedFrom":sQuery(id+"F15.wireOp",EDGE,"E752")}),1.0]])]});
            extrude(context, id + "F18", {"entities" : qUnion([Q0]), "operationType" : NewBodyOperationType.ADD, "depth" : 10000 * mm});
        }
        {
            var Q0;
            {var subQ0=sQuery(id+"F15.wireOp",EDGE,"E746");var subQ1=makeQuery(id+"F1.opExtrude","CAP_EDGE",EDGE,{"disambiguationData":[OSD([sQuery(id+"F0.wireOp",EDGE,"E0.bottom")])],"isStart":true});var subQ2=makeQuery(id+"F15.imprint","INTERSECT",VERTEX,{"disambiguationData":[OD(0.0)],"derivedFrom":[subQ1,subQ0]});Q0=makeQuery(id+"F15.imprint","IMPRINT",FACE,{"disambiguationData":[TD([[makeQuery(id+"F15.imprint","IMPRINT",EDGE,{"disambiguationData":[TD([[subQ2,-1.0]])],"derivedFrom":subQ0}),1.0]])]});}
            var Q1;
            {var subQ0=sQuery(id+"F15.wireOp",EDGE,"E746");var subQ1=makeQuery(id+"F1.opExtrude","CAP_EDGE",EDGE,{"disambiguationData":[OSD([sQuery(id+"F0.wireOp",EDGE,"E0.top")])],"isStart":true});var subQ2=makeQuery(id+"F15.imprint","INTERSECT",VERTEX,{"disambiguationData":[OD(0.0)],"derivedFrom":[subQ1,subQ0]});Q1=makeQuery(id+"F15.imprint","IMPRINT",FACE,{"disambiguationData":[TD([[makeQuery(id+"F15.imprint","IMPRINT",EDGE,{"disambiguationData":[TD([[subQ2,-1.0]])],"derivedFrom":subQ0}),1.0]])]});}
            var Q2;
            {var subQ0=sQuery(id+"F15.wireOp",EDGE,"E749");var subQ1=makeQuery(id+"F15.imprint","IMPRINT",VERTEX,{"derivedFrom":subQ0});Q2=makeQuery(id+"F15.imprint","IMPRINT",FACE,{"disambiguationData":[TD([[makeQuery(id+"F15.imprint","IMPRINT",EDGE,{"disambiguationData":[TD([[subQ1,-1.0]])],"derivedFrom":subQ0}),1.0]])]});}
            var Q3;
            {var subQ0=sQuery(id+"F15.wireOp",EDGE,"E749");var subQ1=makeQuery(id+"F15.imprint","IMPRINT",VERTEX,{"derivedFrom":subQ0});Q3=makeQuery(id+"F15.imprint","IMPRINT",FACE,{"disambiguationData":[TD([[makeQuery(id+"F15.imprint","IMPRINT",EDGE,{"disambiguationData":[TD([[subQ1,-1.0]])],"derivedFrom":subQ0}),-1.0]])]});}
            extrude(context, id + "F19", {"entities" : qUnion([Q0, Q1, Q2, Q3]), "operationType" : NewBodyOperationType.ADD, "oppositeDirection" : true, "depth" : 2500 * mm});
        }
        {
            var Q0;
            {var subQ0=sQuery(id+"F15.wireOp",EDGE,"E749");var subQ1=makeQuery(id+"F15.imprint","IMPRINT",VERTEX,{"derivedFrom":subQ0});Q0=makeQuery(id+"F15.imprint","IMPRINT",FACE,{"disambiguationData":[TD([[makeQuery(id+"F15.imprint","IMPRINT",EDGE,{"disambiguationData":[TD([[subQ1,1.0]])],"derivedFrom":subQ0}),1.0]])]});}
            var Q1;
            {var subQ0=sQuery(id+"F15.wireOp",EDGE,"E749");var subQ1=makeQuery(id+"F15.imprint","IMPRINT",VERTEX,{"derivedFrom":subQ0});Q1=makeQuery(id+"F15.imprint","IMPRINT",FACE,{"disambiguationData":[TD([[makeQuery(id+"F15.imprint","IMPRINT",EDGE,{"disambiguationData":[TD([[subQ1,1.0]])],"derivedFrom":subQ0}),-1.0]])]});}
            extrude(context, id + "F20", {"entities" : qUnion([Q0, Q1]), "operationType" : NewBodyOperationType.ADD, "depth" : 10000 * mm});
        }
        {
            var Q0;
            {var subQ9=sQuery(id+"F4.wireOp",EDGE,"E11");Q0=makeQuery(id+"F4.imprint","IMPRINT",FACE,{"disambiguationData":[TD([[makeQuery(id+"F4.imprint","IMPRINT",EDGE,{"derivedFrom":subQ9}),-1.0]])]});}
            var Q1;
            {var subQ0=sQuery(id+"F4.wireOp",EDGE,"E14");var subQ3=sQuery(id+"F4.wireOp",EDGE,"E727");var subQ4=makeQuery(id+"F4.imprint","INTERSECT",VERTEX,{"derivedFrom":[subQ0,subQ3]});Q1=makeQuery(id+"F4.imprint","IMPRINT",FACE,{"disambiguationData":[TD([[makeQuery(id+"F4.imprint","IMPRINT",EDGE,{"disambiguationData":[TD([[subQ4,1.0]])],"derivedFrom":subQ0}),-1.0]])]});}
            var Q2;
            {var subQ0=sQuery(id+"F4.wireOp",EDGE,"E16");Q2=makeQuery(id+"F4.imprint","IMPRINT",FACE,{"disambiguationData":[TD([[makeQuery(id+"F4.imprint","IMPRINT",EDGE,{"derivedFrom":subQ0}),-1.0]])]});}
            var Q3;
            {var subQ8=sQuery(id+"F4.wireOp",EDGE,"E16");Q3=makeQuery(id+"F4.imprint","IMPRINT",FACE,{"disambiguationData":[TD([[makeQuery(id+"F4.imprint","IMPRINT",EDGE,{"derivedFrom":subQ8}),1.0]])]});}
            var Q4;
            {var subQ0=sQuery(id+"F4.wireOp",EDGE,"E24");Q4=makeQuery(id+"F4.imprint","IMPRINT",FACE,{"disambiguationData":[TD([[makeQuery(id+"F4.imprint","IMPRINT",EDGE,{"derivedFrom":subQ0}),-1.0]])]});}
            var Q5;
            {var subQ0=sQuery(id+"F4.wireOp",EDGE,"E32");Q5=makeQuery(id+"F4.imprint","IMPRINT",FACE,{"disambiguationData":[TD([[makeQuery(id+"F4.imprint","IMPRINT",EDGE,{"derivedFrom":subQ0}),-1.0]])]});}
            var Q6;
            {var subQ3=sQuery(id+"F4.wireOp",EDGE,"E35");Q6=makeQuery(id+"F4.imprint","IMPRINT",FACE,{"disambiguationData":[TD([[makeQuery(id+"F4.imprint","IMPRINT",EDGE,{"derivedFrom":subQ3}),-1.0]])]});}
            var Q7;
            {var subQ3=sQuery(id+"F4.wireOp",EDGE,"E43");Q7=makeQuery(id+"F4.imprint","IMPRINT",FACE,{"disambiguationData":[TD([[makeQuery(id+"F4.imprint","IMPRINT",EDGE,{"derivedFrom":subQ3}),-1.0]])]});}
            var Q8;
            {var subQ0=sQuery(id+"F4.wireOp",EDGE,"E40");Q8=makeQuery(id+"F4.imprint","IMPRINT",FACE,{"disambiguationData":[TD([[makeQuery(id+"F4.imprint","IMPRINT",EDGE,{"derivedFrom":subQ0}),-1.0]])]});}
            var Q9;
            {var subQ3=sQuery(id+"F4.wireOp",EDGE,"E51");Q9=makeQuery(id+"F4.imprint","IMPRINT",FACE,{"disambiguationData":[TD([[makeQuery(id+"F4.imprint","IMPRINT",EDGE,{"derivedFrom":subQ3}),-1.0]])]});}
            var Q10;
            {var subQ0=sQuery(id+"F4.wireOp",EDGE,"E48");Q10=makeQuery(id+"F4.imprint","IMPRINT",FACE,{"disambiguationData":[TD([[makeQuery(id+"F4.imprint","IMPRINT",EDGE,{"derivedFrom":subQ0}),-1.0]])]});}
            var Q11;
            {var subQ3=sQuery(id+"F4.wireOp",EDGE,"E59");Q11=makeQuery(id+"F4.imprint","IMPRINT",FACE,{"disambiguationData":[TD([[makeQuery(id+"F4.imprint","IMPRINT",EDGE,{"derivedFrom":subQ3}),-1.0]])]});}
            var Q12;
            {var subQ0=sQuery(id+"F4.wireOp",EDGE,"E56");Q12=makeQuery(id+"F4.imprint","IMPRINT",FACE,{"disambiguationData":[TD([[makeQuery(id+"F4.imprint","IMPRINT",EDGE,{"derivedFrom":subQ0}),-1.0]])]});}
            var Q13;
            {var subQ3=sQuery(id+"F4.wireOp",EDGE,"E67");Q13=makeQuery(id+"F4.imprint","IMPRINT",FACE,{"disambiguationData":[TD([[makeQuery(id+"F4.imprint","IMPRINT",EDGE,{"derivedFrom":subQ3}),-1.0]])]});}
            var Q14;
            {var subQ0=sQuery(id+"F4.wireOp",EDGE,"E64");Q14=makeQuery(id+"F4.imprint","IMPRINT",FACE,{"disambiguationData":[TD([[makeQuery(id+"F4.imprint","IMPRINT",EDGE,{"derivedFrom":subQ0}),-1.0]])]});}
            var Q15;
            {var subQ3=sQuery(id+"F4.wireOp",EDGE,"E76");Q15=makeQuery(id+"F4.imprint","IMPRINT",FACE,{"disambiguationData":[TD([[makeQuery(id+"F4.imprint","IMPRINT",EDGE,{"derivedFrom":subQ3}),-1.0]])]});}
            var Q16;
            {var subQ0=sQuery(id+"F4.wireOp",EDGE,"E73");Q16=makeQuery(id+"F4.imprint","IMPRINT",FACE,{"disambiguationData":[TD([[makeQuery(id+"F4.imprint","IMPRINT",EDGE,{"derivedFrom":subQ0}),-1.0]])]});}
            var Q17;
            {var subQ3=sQuery(id+"F4.wireOp",EDGE,"E84");Q17=makeQuery(id+"F4.imprint","IMPRINT",FACE,{"disambiguationData":[TD([[makeQuery(id+"F4.imprint","IMPRINT",EDGE,{"derivedFrom":subQ3}),-1.0]])]});}
            var Q18;
            {var subQ0=sQuery(id+"F4.wireOp",EDGE,"E81");Q18=makeQuery(id+"F4.imprint","IMPRINT",FACE,{"disambiguationData":[TD([[makeQuery(id+"F4.imprint","IMPRINT",EDGE,{"derivedFrom":subQ0}),-1.0]])]});}
            var Q19;
            {var subQ3=sQuery(id+"F4.wireOp",EDGE,"E92");Q19=makeQuery(id+"F4.imprint","IMPRINT",FACE,{"disambiguationData":[TD([[makeQuery(id+"F4.imprint","IMPRINT",EDGE,{"derivedFrom":subQ3}),-1.0]])]});}
            var Q20;
            {var subQ0=sQuery(id+"F4.wireOp",EDGE,"E89");Q20=makeQuery(id+"F4.imprint","IMPRINT",FACE,{"disambiguationData":[TD([[makeQuery(id+"F4.imprint","IMPRINT",EDGE,{"derivedFrom":subQ0}),-1.0]])]});}
            var Q21;
            {var subQ3=sQuery(id+"F4.wireOp",EDGE,"E100");Q21=makeQuery(id+"F4.imprint","IMPRINT",FACE,{"disambiguationData":[TD([[makeQuery(id+"F4.imprint","IMPRINT",EDGE,{"derivedFrom":subQ3}),-1.0]])]});}
            var Q22;
            {var subQ0=sQuery(id+"F4.wireOp",EDGE,"E97");Q22=makeQuery(id+"F4.imprint","IMPRINT",FACE,{"disambiguationData":[TD([[makeQuery(id+"F4.imprint","IMPRINT",EDGE,{"derivedFrom":subQ0}),-1.0]])]});}
            var Q23;
            {var subQ3=sQuery(id+"F4.wireOp",EDGE,"E108");Q23=makeQuery(id+"F4.imprint","IMPRINT",FACE,{"disambiguationData":[TD([[makeQuery(id+"F4.imprint","IMPRINT",EDGE,{"derivedFrom":subQ3}),-1.0]])]});}
            var Q24;
            {var subQ0=sQuery(id+"F4.wireOp",EDGE,"E105");Q24=makeQuery(id+"F4.imprint","IMPRINT",FACE,{"disambiguationData":[TD([[makeQuery(id+"F4.imprint","IMPRINT",EDGE,{"derivedFrom":subQ0}),-1.0]])]});}
            var Q25;
            {var subQ3=sQuery(id+"F4.wireOp",EDGE,"E116");Q25=makeQuery(id+"F4.imprint","IMPRINT",FACE,{"disambiguationData":[TD([[makeQuery(id+"F4.imprint","IMPRINT",EDGE,{"derivedFrom":subQ3}),-1.0]])]});}
            var Q26;
            {var subQ0=sQuery(id+"F4.wireOp",EDGE,"E113");Q26=makeQuery(id+"F4.imprint","IMPRINT",FACE,{"disambiguationData":[TD([[makeQuery(id+"F4.imprint","IMPRINT",EDGE,{"derivedFrom":subQ0}),-1.0]])]});}
            var Q27;
            {var subQ3=sQuery(id+"F4.wireOp",EDGE,"E124");Q27=makeQuery(id+"F4.imprint","IMPRINT",FACE,{"disambiguationData":[TD([[makeQuery(id+"F4.imprint","IMPRINT",EDGE,{"derivedFrom":subQ3}),-1.0]])]});}
            var Q28;
            {var subQ0=sQuery(id+"F4.wireOp",EDGE,"E121");Q28=makeQuery(id+"F4.imprint","IMPRINT",FACE,{"disambiguationData":[TD([[makeQuery(id+"F4.imprint","IMPRINT",EDGE,{"derivedFrom":subQ0}),-1.0]])]});}
            var Q29;
            {var subQ3=sQuery(id+"F4.wireOp",EDGE,"E132");Q29=makeQuery(id+"F4.imprint","IMPRINT",FACE,{"disambiguationData":[TD([[makeQuery(id+"F4.imprint","IMPRINT",EDGE,{"derivedFrom":subQ3}),-1.0]])]});}
            var Q30;
            {var subQ0=sQuery(id+"F4.wireOp",EDGE,"E129");Q30=makeQuery(id+"F4.imprint","IMPRINT",FACE,{"disambiguationData":[TD([[makeQuery(id+"F4.imprint","IMPRINT",EDGE,{"derivedFrom":subQ0}),-1.0]])]});}
            var Q31;
            {var subQ3=sQuery(id+"F4.wireOp",EDGE,"E140");Q31=makeQuery(id+"F4.imprint","IMPRINT",FACE,{"disambiguationData":[TD([[makeQuery(id+"F4.imprint","IMPRINT",EDGE,{"derivedFrom":subQ3}),-1.0]])]});}
            var Q32;
            {var subQ0=sQuery(id+"F4.wireOp",EDGE,"E137");Q32=makeQuery(id+"F4.imprint","IMPRINT",FACE,{"disambiguationData":[TD([[makeQuery(id+"F4.imprint","IMPRINT",EDGE,{"derivedFrom":subQ0}),-1.0]])]});}
            var Q33;
            {var subQ3=sQuery(id+"F4.wireOp",EDGE,"E148");Q33=makeQuery(id+"F4.imprint","IMPRINT",FACE,{"disambiguationData":[TD([[makeQuery(id+"F4.imprint","IMPRINT",EDGE,{"derivedFrom":subQ3}),-1.0]])]});}
            var Q34;
            {var subQ0=sQuery(id+"F4.wireOp",EDGE,"E145");Q34=makeQuery(id+"F4.imprint","IMPRINT",FACE,{"disambiguationData":[TD([[makeQuery(id+"F4.imprint","IMPRINT",EDGE,{"derivedFrom":subQ0}),-1.0]])]});}
            var Q35;
            {var subQ3=sQuery(id+"F4.wireOp",EDGE,"E156");Q35=makeQuery(id+"F4.imprint","IMPRINT",FACE,{"disambiguationData":[TD([[makeQuery(id+"F4.imprint","IMPRINT",EDGE,{"derivedFrom":subQ3}),-1.0]])]});}
            var Q36;
            {var subQ0=sQuery(id+"F4.wireOp",EDGE,"E153");Q36=makeQuery(id+"F4.imprint","IMPRINT",FACE,{"disambiguationData":[TD([[makeQuery(id+"F4.imprint","IMPRINT",EDGE,{"derivedFrom":subQ0}),-1.0]])]});}
            var Q37;
            {var subQ3=sQuery(id+"F4.wireOp",EDGE,"E164");Q37=makeQuery(id+"F4.imprint","IMPRINT",FACE,{"disambiguationData":[TD([[makeQuery(id+"F4.imprint","IMPRINT",EDGE,{"derivedFrom":subQ3}),-1.0]])]});}
            var Q38;
            {var subQ0=sQuery(id+"F4.wireOp",EDGE,"E161");Q38=makeQuery(id+"F4.imprint","IMPRINT",FACE,{"disambiguationData":[TD([[makeQuery(id+"F4.imprint","IMPRINT",EDGE,{"derivedFrom":subQ0}),-1.0]])]});}
            var Q39;
            {var subQ3=sQuery(id+"F4.wireOp",EDGE,"E172");Q39=makeQuery(id+"F4.imprint","IMPRINT",FACE,{"disambiguationData":[TD([[makeQuery(id+"F4.imprint","IMPRINT",EDGE,{"derivedFrom":subQ3}),-1.0]])]});}
            var Q40;
            {var subQ0=sQuery(id+"F4.wireOp",EDGE,"E169");Q40=makeQuery(id+"F4.imprint","IMPRINT",FACE,{"disambiguationData":[TD([[makeQuery(id+"F4.imprint","IMPRINT",EDGE,{"derivedFrom":subQ0}),-1.0]])]});}
            var Q41;
            {var subQ3=sQuery(id+"F4.wireOp",EDGE,"E180");Q41=makeQuery(id+"F4.imprint","IMPRINT",FACE,{"disambiguationData":[TD([[makeQuery(id+"F4.imprint","IMPRINT",EDGE,{"derivedFrom":subQ3}),-1.0]])]});}
            var Q42;
            {var subQ0=sQuery(id+"F4.wireOp",EDGE,"E177");Q42=makeQuery(id+"F4.imprint","IMPRINT",FACE,{"disambiguationData":[TD([[makeQuery(id+"F4.imprint","IMPRINT",EDGE,{"derivedFrom":subQ0}),-1.0]])]});}
            var Q43;
            {var subQ3=sQuery(id+"F4.wireOp",EDGE,"E188");Q43=makeQuery(id+"F4.imprint","IMPRINT",FACE,{"disambiguationData":[TD([[makeQuery(id+"F4.imprint","IMPRINT",EDGE,{"derivedFrom":subQ3}),-1.0]])]});}
            var Q44;
            {var subQ0=sQuery(id+"F4.wireOp",EDGE,"E185");Q44=makeQuery(id+"F4.imprint","IMPRINT",FACE,{"disambiguationData":[TD([[makeQuery(id+"F4.imprint","IMPRINT",EDGE,{"derivedFrom":subQ0}),-1.0]])]});}
            var Q45;
            {var subQ3=sQuery(id+"F4.wireOp",EDGE,"E196");Q45=makeQuery(id+"F4.imprint","IMPRINT",FACE,{"disambiguationData":[TD([[makeQuery(id+"F4.imprint","IMPRINT",EDGE,{"derivedFrom":subQ3}),-1.0]])]});}
            var Q46;
            {var subQ0=sQuery(id+"F4.wireOp",EDGE,"E193");Q46=makeQuery(id+"F4.imprint","IMPRINT",FACE,{"disambiguationData":[TD([[makeQuery(id+"F4.imprint","IMPRINT",EDGE,{"derivedFrom":subQ0}),-1.0]])]});}
            var Q47;
            {var subQ3=sQuery(id+"F4.wireOp",EDGE,"E204");Q47=makeQuery(id+"F4.imprint","IMPRINT",FACE,{"disambiguationData":[TD([[makeQuery(id+"F4.imprint","IMPRINT",EDGE,{"derivedFrom":subQ3}),-1.0]])]});}
            var Q48;
            {var subQ0=sQuery(id+"F4.wireOp",EDGE,"E201");Q48=makeQuery(id+"F4.imprint","IMPRINT",FACE,{"disambiguationData":[TD([[makeQuery(id+"F4.imprint","IMPRINT",EDGE,{"derivedFrom":subQ0}),-1.0]])]});}
            var Q49;
            {var subQ3=sQuery(id+"F4.wireOp",EDGE,"E212");Q49=makeQuery(id+"F4.imprint","IMPRINT",FACE,{"disambiguationData":[TD([[makeQuery(id+"F4.imprint","IMPRINT",EDGE,{"derivedFrom":subQ3}),-1.0]])]});}
            var Q50;
            {var subQ0=sQuery(id+"F4.wireOp",EDGE,"E209");Q50=makeQuery(id+"F4.imprint","IMPRINT",FACE,{"disambiguationData":[TD([[makeQuery(id+"F4.imprint","IMPRINT",EDGE,{"derivedFrom":subQ0}),-1.0]])]});}
            var Q51;
            {var subQ3=sQuery(id+"F4.wireOp",EDGE,"E220");Q51=makeQuery(id+"F4.imprint","IMPRINT",FACE,{"disambiguationData":[TD([[makeQuery(id+"F4.imprint","IMPRINT",EDGE,{"derivedFrom":subQ3}),-1.0]])]});}
            var Q52;
            {var subQ0=sQuery(id+"F4.wireOp",EDGE,"E217");Q52=makeQuery(id+"F4.imprint","IMPRINT",FACE,{"disambiguationData":[TD([[makeQuery(id+"F4.imprint","IMPRINT",EDGE,{"derivedFrom":subQ0}),-1.0]])]});}
            var Q53;
            {var subQ3=sQuery(id+"F4.wireOp",EDGE,"E229");Q53=makeQuery(id+"F4.imprint","IMPRINT",FACE,{"disambiguationData":[TD([[makeQuery(id+"F4.imprint","IMPRINT",EDGE,{"derivedFrom":subQ3}),-1.0]])]});}
            var Q54;
            {var subQ0=sQuery(id+"F4.wireOp",EDGE,"E226");Q54=makeQuery(id+"F4.imprint","IMPRINT",FACE,{"disambiguationData":[TD([[makeQuery(id+"F4.imprint","IMPRINT",EDGE,{"derivedFrom":subQ0}),-1.0]])]});}
            var Q55;
            {var subQ3=sQuery(id+"F4.wireOp",EDGE,"E237");Q55=makeQuery(id+"F4.imprint","IMPRINT",FACE,{"disambiguationData":[TD([[makeQuery(id+"F4.imprint","IMPRINT",EDGE,{"derivedFrom":subQ3}),-1.0]])]});}
            var Q56;
            {var subQ0=sQuery(id+"F4.wireOp",EDGE,"E234");Q56=makeQuery(id+"F4.imprint","IMPRINT",FACE,{"disambiguationData":[TD([[makeQuery(id+"F4.imprint","IMPRINT",EDGE,{"derivedFrom":subQ0}),-1.0]])]});}
            var Q57;
            {var subQ3=sQuery(id+"F4.wireOp",EDGE,"E245");Q57=makeQuery(id+"F4.imprint","IMPRINT",FACE,{"disambiguationData":[TD([[makeQuery(id+"F4.imprint","IMPRINT",EDGE,{"derivedFrom":subQ3}),-1.0]])]});}
            var Q58;
            {var subQ0=sQuery(id+"F4.wireOp",EDGE,"E242");Q58=makeQuery(id+"F4.imprint","IMPRINT",FACE,{"disambiguationData":[TD([[makeQuery(id+"F4.imprint","IMPRINT",EDGE,{"derivedFrom":subQ0}),-1.0]])]});}
            var Q59;
            {var subQ3=sQuery(id+"F4.wireOp",EDGE,"E253");Q59=makeQuery(id+"F4.imprint","IMPRINT",FACE,{"disambiguationData":[TD([[makeQuery(id+"F4.imprint","IMPRINT",EDGE,{"derivedFrom":subQ3}),-1.0]])]});}
            var Q60;
            {var subQ0=sQuery(id+"F4.wireOp",EDGE,"E250");Q60=makeQuery(id+"F4.imprint","IMPRINT",FACE,{"disambiguationData":[TD([[makeQuery(id+"F4.imprint","IMPRINT",EDGE,{"derivedFrom":subQ0}),-1.0]])]});}
            var Q61;
            {var subQ3=sQuery(id+"F4.wireOp",EDGE,"E261");Q61=makeQuery(id+"F4.imprint","IMPRINT",FACE,{"disambiguationData":[TD([[makeQuery(id+"F4.imprint","IMPRINT",EDGE,{"derivedFrom":subQ3}),-1.0]])]});}
            var Q62;
            {var subQ0=sQuery(id+"F4.wireOp",EDGE,"E258");Q62=makeQuery(id+"F4.imprint","IMPRINT",FACE,{"disambiguationData":[TD([[makeQuery(id+"F4.imprint","IMPRINT",EDGE,{"derivedFrom":subQ0}),-1.0]])]});}
            var Q63;
            {var subQ3=sQuery(id+"F4.wireOp",EDGE,"E269");Q63=makeQuery(id+"F4.imprint","IMPRINT",FACE,{"disambiguationData":[TD([[makeQuery(id+"F4.imprint","IMPRINT",EDGE,{"derivedFrom":subQ3}),-1.0]])]});}
            var Q64;
            {var subQ0=sQuery(id+"F4.wireOp",EDGE,"E266");Q64=makeQuery(id+"F4.imprint","IMPRINT",FACE,{"disambiguationData":[TD([[makeQuery(id+"F4.imprint","IMPRINT",EDGE,{"derivedFrom":subQ0}),-1.0]])]});}
            var Q65;
            {var subQ3=sQuery(id+"F4.wireOp",EDGE,"E277");Q65=makeQuery(id+"F4.imprint","IMPRINT",FACE,{"disambiguationData":[TD([[makeQuery(id+"F4.imprint","IMPRINT",EDGE,{"derivedFrom":subQ3}),-1.0]])]});}
            var Q66;
            {var subQ0=sQuery(id+"F4.wireOp",EDGE,"E274");Q66=makeQuery(id+"F4.imprint","IMPRINT",FACE,{"disambiguationData":[TD([[makeQuery(id+"F4.imprint","IMPRINT",EDGE,{"derivedFrom":subQ0}),-1.0]])]});}
            var Q67;
            {var subQ3=sQuery(id+"F4.wireOp",EDGE,"E285");Q67=makeQuery(id+"F4.imprint","IMPRINT",FACE,{"disambiguationData":[TD([[makeQuery(id+"F4.imprint","IMPRINT",EDGE,{"derivedFrom":subQ3}),-1.0]])]});}
            var Q68;
            {var subQ0=sQuery(id+"F4.wireOp",EDGE,"E282");Q68=makeQuery(id+"F4.imprint","IMPRINT",FACE,{"disambiguationData":[TD([[makeQuery(id+"F4.imprint","IMPRINT",EDGE,{"derivedFrom":subQ0}),-1.0]])]});}
            var Q69;
            {var subQ3=sQuery(id+"F4.wireOp",EDGE,"E293");Q69=makeQuery(id+"F4.imprint","IMPRINT",FACE,{"disambiguationData":[TD([[makeQuery(id+"F4.imprint","IMPRINT",EDGE,{"derivedFrom":subQ3}),-1.0]])]});}
            var Q70;
            {var subQ0=sQuery(id+"F4.wireOp",EDGE,"E290");Q70=makeQuery(id+"F4.imprint","IMPRINT",FACE,{"disambiguationData":[TD([[makeQuery(id+"F4.imprint","IMPRINT",EDGE,{"derivedFrom":subQ0}),-1.0]])]});}
            var Q71;
            {var subQ3=sQuery(id+"F4.wireOp",EDGE,"E301");Q71=makeQuery(id+"F4.imprint","IMPRINT",FACE,{"disambiguationData":[TD([[makeQuery(id+"F4.imprint","IMPRINT",EDGE,{"derivedFrom":subQ3}),-1.0]])]});}
            var Q72;
            {var subQ0=sQuery(id+"F4.wireOp",EDGE,"E298");Q72=makeQuery(id+"F4.imprint","IMPRINT",FACE,{"disambiguationData":[TD([[makeQuery(id+"F4.imprint","IMPRINT",EDGE,{"derivedFrom":subQ0}),-1.0]])]});}
            var Q73;
            {var subQ3=sQuery(id+"F4.wireOp",EDGE,"E309");Q73=makeQuery(id+"F4.imprint","IMPRINT",FACE,{"disambiguationData":[TD([[makeQuery(id+"F4.imprint","IMPRINT",EDGE,{"derivedFrom":subQ3}),-1.0]])]});}
            var Q74;
            {var subQ0=sQuery(id+"F4.wireOp",EDGE,"E306");Q74=makeQuery(id+"F4.imprint","IMPRINT",FACE,{"disambiguationData":[TD([[makeQuery(id+"F4.imprint","IMPRINT",EDGE,{"derivedFrom":subQ0}),-1.0]])]});}
            var Q75;
            {var subQ3=sQuery(id+"F4.wireOp",EDGE,"E317");Q75=makeQuery(id+"F4.imprint","IMPRINT",FACE,{"disambiguationData":[TD([[makeQuery(id+"F4.imprint","IMPRINT",EDGE,{"derivedFrom":subQ3}),-1.0]])]});}
            var Q76;
            {var subQ0=sQuery(id+"F4.wireOp",EDGE,"E314");Q76=makeQuery(id+"F4.imprint","IMPRINT",FACE,{"disambiguationData":[TD([[makeQuery(id+"F4.imprint","IMPRINT",EDGE,{"derivedFrom":subQ0}),-1.0]])]});}
            var Q77;
            {var subQ3=sQuery(id+"F4.wireOp",EDGE,"E325");Q77=makeQuery(id+"F4.imprint","IMPRINT",FACE,{"disambiguationData":[TD([[makeQuery(id+"F4.imprint","IMPRINT",EDGE,{"derivedFrom":subQ3}),-1.0]])]});}
            var Q78;
            {var subQ0=sQuery(id+"F4.wireOp",EDGE,"E322");Q78=makeQuery(id+"F4.imprint","IMPRINT",FACE,{"disambiguationData":[TD([[makeQuery(id+"F4.imprint","IMPRINT",EDGE,{"derivedFrom":subQ0}),-1.0]])]});}
            var Q79;
            {var subQ3=sQuery(id+"F4.wireOp",EDGE,"E333");Q79=makeQuery(id+"F4.imprint","IMPRINT",FACE,{"disambiguationData":[TD([[makeQuery(id+"F4.imprint","IMPRINT",EDGE,{"derivedFrom":subQ3}),-1.0]])]});}
            var Q80;
            {var subQ0=sQuery(id+"F4.wireOp",EDGE,"E330");Q80=makeQuery(id+"F4.imprint","IMPRINT",FACE,{"disambiguationData":[TD([[makeQuery(id+"F4.imprint","IMPRINT",EDGE,{"derivedFrom":subQ0}),-1.0]])]});}
            var Q81;
            {var subQ3=sQuery(id+"F4.wireOp",EDGE,"E341");Q81=makeQuery(id+"F4.imprint","IMPRINT",FACE,{"disambiguationData":[TD([[makeQuery(id+"F4.imprint","IMPRINT",EDGE,{"derivedFrom":subQ3}),-1.0]])]});}
            var Q82;
            {var subQ0=sQuery(id+"F4.wireOp",EDGE,"E338");Q82=makeQuery(id+"F4.imprint","IMPRINT",FACE,{"disambiguationData":[TD([[makeQuery(id+"F4.imprint","IMPRINT",EDGE,{"derivedFrom":subQ0}),-1.0]])]});}
            var Q83;
            {var subQ3=sQuery(id+"F4.wireOp",EDGE,"E349");Q83=makeQuery(id+"F4.imprint","IMPRINT",FACE,{"disambiguationData":[TD([[makeQuery(id+"F4.imprint","IMPRINT",EDGE,{"derivedFrom":subQ3}),-1.0]])]});}
            var Q84;
            {var subQ0=sQuery(id+"F4.wireOp",EDGE,"E346");Q84=makeQuery(id+"F4.imprint","IMPRINT",FACE,{"disambiguationData":[TD([[makeQuery(id+"F4.imprint","IMPRINT",EDGE,{"derivedFrom":subQ0}),-1.0]])]});}
            var Q85;
            {var subQ3=sQuery(id+"F4.wireOp",EDGE,"E357");Q85=makeQuery(id+"F4.imprint","IMPRINT",FACE,{"disambiguationData":[TD([[makeQuery(id+"F4.imprint","IMPRINT",EDGE,{"derivedFrom":subQ3}),-1.0]])]});}
            var Q86;
            {var subQ0=sQuery(id+"F4.wireOp",EDGE,"E354");Q86=makeQuery(id+"F4.imprint","IMPRINT",FACE,{"disambiguationData":[TD([[makeQuery(id+"F4.imprint","IMPRINT",EDGE,{"derivedFrom":subQ0}),-1.0]])]});}
            var Q87;
            {var subQ3=sQuery(id+"F4.wireOp",EDGE,"E365");Q87=makeQuery(id+"F4.imprint","IMPRINT",FACE,{"disambiguationData":[TD([[makeQuery(id+"F4.imprint","IMPRINT",EDGE,{"derivedFrom":subQ3}),-1.0]])]});}
            var Q88;
            {var subQ0=sQuery(id+"F4.wireOp",EDGE,"E362");Q88=makeQuery(id+"F4.imprint","IMPRINT",FACE,{"disambiguationData":[TD([[makeQuery(id+"F4.imprint","IMPRINT",EDGE,{"derivedFrom":subQ0}),-1.0]])]});}
            var Q89;
            {var subQ3=sQuery(id+"F4.wireOp",EDGE,"E373");Q89=makeQuery(id+"F4.imprint","IMPRINT",FACE,{"disambiguationData":[TD([[makeQuery(id+"F4.imprint","IMPRINT",EDGE,{"derivedFrom":subQ3}),-1.0]])]});}
            var Q90;
            {var subQ0=sQuery(id+"F4.wireOp",EDGE,"E370");Q90=makeQuery(id+"F4.imprint","IMPRINT",FACE,{"disambiguationData":[TD([[makeQuery(id+"F4.imprint","IMPRINT",EDGE,{"derivedFrom":subQ0}),-1.0]])]});}
            var Q91;
            {var subQ0=sQuery(id+"F4.wireOp",EDGE,"E375");Q91=makeQuery(id+"F4.imprint","IMPRINT",FACE,{"disambiguationData":[TD([[makeQuery(id+"F4.imprint","IMPRINT",EDGE,{"derivedFrom":subQ0}),-1.0]])]});}
            var Q92;
            {var subQ8=sQuery(id+"F4.wireOp",EDGE,"E375");Q92=makeQuery(id+"F4.imprint","IMPRINT",FACE,{"disambiguationData":[TD([[makeQuery(id+"F4.imprint","IMPRINT",EDGE,{"derivedFrom":subQ8}),1.0]])]});}
            var Q93;
            {var subQ3=sQuery(id+"F4.wireOp",EDGE,"E386");Q93=makeQuery(id+"F4.imprint","IMPRINT",FACE,{"disambiguationData":[TD([[makeQuery(id+"F4.imprint","IMPRINT",EDGE,{"derivedFrom":subQ3}),-1.0]])]});}
            var Q94;
            {var subQ0=sQuery(id+"F4.wireOp",EDGE,"E383");Q94=makeQuery(id+"F4.imprint","IMPRINT",FACE,{"disambiguationData":[TD([[makeQuery(id+"F4.imprint","IMPRINT",EDGE,{"derivedFrom":subQ0}),-1.0]])]});}
            var Q95;
            {var subQ3=sQuery(id+"F4.wireOp",EDGE,"E394");Q95=makeQuery(id+"F4.imprint","IMPRINT",FACE,{"disambiguationData":[TD([[makeQuery(id+"F4.imprint","IMPRINT",EDGE,{"derivedFrom":subQ3}),-1.0]])]});}
            var Q96;
            {var subQ0=sQuery(id+"F4.wireOp",EDGE,"E391");Q96=makeQuery(id+"F4.imprint","IMPRINT",FACE,{"disambiguationData":[TD([[makeQuery(id+"F4.imprint","IMPRINT",EDGE,{"derivedFrom":subQ0}),-1.0]])]});}
            var Q97;
            {var subQ3=sQuery(id+"F4.wireOp",EDGE,"E402");Q97=makeQuery(id+"F4.imprint","IMPRINT",FACE,{"disambiguationData":[TD([[makeQuery(id+"F4.imprint","IMPRINT",EDGE,{"derivedFrom":subQ3}),-1.0]])]});}
            var Q98;
            {var subQ0=sQuery(id+"F4.wireOp",EDGE,"E399");Q98=makeQuery(id+"F4.imprint","IMPRINT",FACE,{"disambiguationData":[TD([[makeQuery(id+"F4.imprint","IMPRINT",EDGE,{"derivedFrom":subQ0}),-1.0]])]});}
            var Q99;
            {var subQ3=sQuery(id+"F4.wireOp",EDGE,"E410");Q99=makeQuery(id+"F4.imprint","IMPRINT",FACE,{"disambiguationData":[TD([[makeQuery(id+"F4.imprint","IMPRINT",EDGE,{"derivedFrom":subQ3}),-1.0]])]});}
            var Q100;
            {var subQ0=sQuery(id+"F4.wireOp",EDGE,"E407");Q100=makeQuery(id+"F4.imprint","IMPRINT",FACE,{"disambiguationData":[TD([[makeQuery(id+"F4.imprint","IMPRINT",EDGE,{"derivedFrom":subQ0}),-1.0]])]});}
            var Q101;
            {var subQ3=sQuery(id+"F4.wireOp",EDGE,"E418");Q101=makeQuery(id+"F4.imprint","IMPRINT",FACE,{"disambiguationData":[TD([[makeQuery(id+"F4.imprint","IMPRINT",EDGE,{"derivedFrom":subQ3}),-1.0]])]});}
            var Q102;
            {var subQ0=sQuery(id+"F4.wireOp",EDGE,"E415");Q102=makeQuery(id+"F4.imprint","IMPRINT",FACE,{"disambiguationData":[TD([[makeQuery(id+"F4.imprint","IMPRINT",EDGE,{"derivedFrom":subQ0}),-1.0]])]});}
            var Q103;
            {var subQ3=sQuery(id+"F4.wireOp",EDGE,"E426");Q103=makeQuery(id+"F4.imprint","IMPRINT",FACE,{"disambiguationData":[TD([[makeQuery(id+"F4.imprint","IMPRINT",EDGE,{"derivedFrom":subQ3}),-1.0]])]});}
            var Q104;
            {var subQ0=sQuery(id+"F4.wireOp",EDGE,"E423");Q104=makeQuery(id+"F4.imprint","IMPRINT",FACE,{"disambiguationData":[TD([[makeQuery(id+"F4.imprint","IMPRINT",EDGE,{"derivedFrom":subQ0}),-1.0]])]});}
            var Q105;
            {var subQ3=sQuery(id+"F4.wireOp",EDGE,"E435");Q105=makeQuery(id+"F4.imprint","IMPRINT",FACE,{"disambiguationData":[TD([[makeQuery(id+"F4.imprint","IMPRINT",EDGE,{"derivedFrom":subQ3}),-1.0]])]});}
            var Q106;
            {var subQ0=sQuery(id+"F4.wireOp",EDGE,"E432");Q106=makeQuery(id+"F4.imprint","IMPRINT",FACE,{"disambiguationData":[TD([[makeQuery(id+"F4.imprint","IMPRINT",EDGE,{"derivedFrom":subQ0}),-1.0]])]});}
            var Q107;
            {var subQ3=sQuery(id+"F4.wireOp",EDGE,"E443");Q107=makeQuery(id+"F4.imprint","IMPRINT",FACE,{"disambiguationData":[TD([[makeQuery(id+"F4.imprint","IMPRINT",EDGE,{"derivedFrom":subQ3}),-1.0]])]});}
            var Q108;
            {var subQ0=sQuery(id+"F4.wireOp",EDGE,"E440");Q108=makeQuery(id+"F4.imprint","IMPRINT",FACE,{"disambiguationData":[TD([[makeQuery(id+"F4.imprint","IMPRINT",EDGE,{"derivedFrom":subQ0}),-1.0]])]});}
            var Q109;
            {var subQ3=sQuery(id+"F4.wireOp",EDGE,"E451");Q109=makeQuery(id+"F4.imprint","IMPRINT",FACE,{"disambiguationData":[TD([[makeQuery(id+"F4.imprint","IMPRINT",EDGE,{"derivedFrom":subQ3}),-1.0]])]});}
            var Q110;
            {var subQ0=sQuery(id+"F4.wireOp",EDGE,"E448");Q110=makeQuery(id+"F4.imprint","IMPRINT",FACE,{"disambiguationData":[TD([[makeQuery(id+"F4.imprint","IMPRINT",EDGE,{"derivedFrom":subQ0}),-1.0]])]});}
            var Q111;
            {var subQ3=sQuery(id+"F4.wireOp",EDGE,"E459");Q111=makeQuery(id+"F4.imprint","IMPRINT",FACE,{"disambiguationData":[TD([[makeQuery(id+"F4.imprint","IMPRINT",EDGE,{"derivedFrom":subQ3}),-1.0]])]});}
            var Q112;
            {var subQ0=sQuery(id+"F4.wireOp",EDGE,"E456");Q112=makeQuery(id+"F4.imprint","IMPRINT",FACE,{"disambiguationData":[TD([[makeQuery(id+"F4.imprint","IMPRINT",EDGE,{"derivedFrom":subQ0}),-1.0]])]});}
            var Q113;
            {var subQ3=sQuery(id+"F4.wireOp",EDGE,"E467");Q113=makeQuery(id+"F4.imprint","IMPRINT",FACE,{"disambiguationData":[TD([[makeQuery(id+"F4.imprint","IMPRINT",EDGE,{"derivedFrom":subQ3}),-1.0]])]});}
            var Q114;
            {var subQ0=sQuery(id+"F4.wireOp",EDGE,"E464");Q114=makeQuery(id+"F4.imprint","IMPRINT",FACE,{"disambiguationData":[TD([[makeQuery(id+"F4.imprint","IMPRINT",EDGE,{"derivedFrom":subQ0}),-1.0]])]});}
            var Q115;
            {var subQ3=sQuery(id+"F4.wireOp",EDGE,"E475");Q115=makeQuery(id+"F4.imprint","IMPRINT",FACE,{"disambiguationData":[TD([[makeQuery(id+"F4.imprint","IMPRINT",EDGE,{"derivedFrom":subQ3}),-1.0]])]});}
            var Q116;
            {var subQ0=sQuery(id+"F4.wireOp",EDGE,"E472");Q116=makeQuery(id+"F4.imprint","IMPRINT",FACE,{"disambiguationData":[TD([[makeQuery(id+"F4.imprint","IMPRINT",EDGE,{"derivedFrom":subQ0}),-1.0]])]});}
            var Q117;
            {var subQ3=sQuery(id+"F4.wireOp",EDGE,"E483");Q117=makeQuery(id+"F4.imprint","IMPRINT",FACE,{"disambiguationData":[TD([[makeQuery(id+"F4.imprint","IMPRINT",EDGE,{"derivedFrom":subQ3}),-1.0]])]});}
            var Q118;
            {var subQ0=sQuery(id+"F4.wireOp",EDGE,"E480");Q118=makeQuery(id+"F4.imprint","IMPRINT",FACE,{"disambiguationData":[TD([[makeQuery(id+"F4.imprint","IMPRINT",EDGE,{"derivedFrom":subQ0}),-1.0]])]});}
            var Q119;
            {var subQ3=sQuery(id+"F4.wireOp",EDGE,"E491");Q119=makeQuery(id+"F4.imprint","IMPRINT",FACE,{"disambiguationData":[TD([[makeQuery(id+"F4.imprint","IMPRINT",EDGE,{"derivedFrom":subQ3}),-1.0]])]});}
            var Q120;
            {var subQ0=sQuery(id+"F4.wireOp",EDGE,"E488");Q120=makeQuery(id+"F4.imprint","IMPRINT",FACE,{"disambiguationData":[TD([[makeQuery(id+"F4.imprint","IMPRINT",EDGE,{"derivedFrom":subQ0}),-1.0]])]});}
            var Q121;
            {var subQ3=sQuery(id+"F4.wireOp",EDGE,"E499");Q121=makeQuery(id+"F4.imprint","IMPRINT",FACE,{"disambiguationData":[TD([[makeQuery(id+"F4.imprint","IMPRINT",EDGE,{"derivedFrom":subQ3}),-1.0]])]});}
            var Q122;
            {var subQ0=sQuery(id+"F4.wireOp",EDGE,"E496");Q122=makeQuery(id+"F4.imprint","IMPRINT",FACE,{"disambiguationData":[TD([[makeQuery(id+"F4.imprint","IMPRINT",EDGE,{"derivedFrom":subQ0}),-1.0]])]});}
            var Q123;
            {var subQ3=sQuery(id+"F4.wireOp",EDGE,"E507");Q123=makeQuery(id+"F4.imprint","IMPRINT",FACE,{"disambiguationData":[TD([[makeQuery(id+"F4.imprint","IMPRINT",EDGE,{"derivedFrom":subQ3}),-1.0]])]});}
            var Q124;
            {var subQ0=sQuery(id+"F4.wireOp",EDGE,"E504");Q124=makeQuery(id+"F4.imprint","IMPRINT",FACE,{"disambiguationData":[TD([[makeQuery(id+"F4.imprint","IMPRINT",EDGE,{"derivedFrom":subQ0}),-1.0]])]});}
            var Q125;
            {var subQ3=sQuery(id+"F4.wireOp",EDGE,"E515");Q125=makeQuery(id+"F4.imprint","IMPRINT",FACE,{"disambiguationData":[TD([[makeQuery(id+"F4.imprint","IMPRINT",EDGE,{"derivedFrom":subQ3}),-1.0]])]});}
            var Q126;
            {var subQ0=sQuery(id+"F4.wireOp",EDGE,"E512");Q126=makeQuery(id+"F4.imprint","IMPRINT",FACE,{"disambiguationData":[TD([[makeQuery(id+"F4.imprint","IMPRINT",EDGE,{"derivedFrom":subQ0}),-1.0]])]});}
            var Q127;
            {var subQ3=sQuery(id+"F4.wireOp",EDGE,"E523");Q127=makeQuery(id+"F4.imprint","IMPRINT",FACE,{"disambiguationData":[TD([[makeQuery(id+"F4.imprint","IMPRINT",EDGE,{"derivedFrom":subQ3}),-1.0]])]});}
            var Q128;
            {var subQ0=sQuery(id+"F4.wireOp",EDGE,"E520");Q128=makeQuery(id+"F4.imprint","IMPRINT",FACE,{"disambiguationData":[TD([[makeQuery(id+"F4.imprint","IMPRINT",EDGE,{"derivedFrom":subQ0}),-1.0]])]});}
            var Q129;
            {var subQ3=sQuery(id+"F4.wireOp",EDGE,"E531");Q129=makeQuery(id+"F4.imprint","IMPRINT",FACE,{"disambiguationData":[TD([[makeQuery(id+"F4.imprint","IMPRINT",EDGE,{"derivedFrom":subQ3}),-1.0]])]});}
            var Q130;
            {var subQ0=sQuery(id+"F4.wireOp",EDGE,"E528");Q130=makeQuery(id+"F4.imprint","IMPRINT",FACE,{"disambiguationData":[TD([[makeQuery(id+"F4.imprint","IMPRINT",EDGE,{"derivedFrom":subQ0}),-1.0]])]});}
            var Q131;
            {var subQ3=sQuery(id+"F4.wireOp",EDGE,"E539");Q131=makeQuery(id+"F4.imprint","IMPRINT",FACE,{"disambiguationData":[TD([[makeQuery(id+"F4.imprint","IMPRINT",EDGE,{"derivedFrom":subQ3}),-1.0]])]});}
            var Q132;
            {var subQ0=sQuery(id+"F4.wireOp",EDGE,"E536");Q132=makeQuery(id+"F4.imprint","IMPRINT",FACE,{"disambiguationData":[TD([[makeQuery(id+"F4.imprint","IMPRINT",EDGE,{"derivedFrom":subQ0}),-1.0]])]});}
            var Q133;
            {var subQ3=sQuery(id+"F4.wireOp",EDGE,"E547");Q133=makeQuery(id+"F4.imprint","IMPRINT",FACE,{"disambiguationData":[TD([[makeQuery(id+"F4.imprint","IMPRINT",EDGE,{"derivedFrom":subQ3}),-1.0]])]});}
            var Q134;
            {var subQ0=sQuery(id+"F4.wireOp",EDGE,"E544");Q134=makeQuery(id+"F4.imprint","IMPRINT",FACE,{"disambiguationData":[TD([[makeQuery(id+"F4.imprint","IMPRINT",EDGE,{"derivedFrom":subQ0}),-1.0]])]});}
            var Q135;
            {var subQ3=sQuery(id+"F4.wireOp",EDGE,"E555");Q135=makeQuery(id+"F4.imprint","IMPRINT",FACE,{"disambiguationData":[TD([[makeQuery(id+"F4.imprint","IMPRINT",EDGE,{"derivedFrom":subQ3}),-1.0]])]});}
            var Q136;
            {var subQ0=sQuery(id+"F4.wireOp",EDGE,"E552");Q136=makeQuery(id+"F4.imprint","IMPRINT",FACE,{"disambiguationData":[TD([[makeQuery(id+"F4.imprint","IMPRINT",EDGE,{"derivedFrom":subQ0}),-1.0]])]});}
            var Q137;
            {var subQ3=sQuery(id+"F4.wireOp",EDGE,"E563");Q137=makeQuery(id+"F4.imprint","IMPRINT",FACE,{"disambiguationData":[TD([[makeQuery(id+"F4.imprint","IMPRINT",EDGE,{"derivedFrom":subQ3}),-1.0]])]});}
            var Q138;
            {var subQ0=sQuery(id+"F4.wireOp",EDGE,"E560");Q138=makeQuery(id+"F4.imprint","IMPRINT",FACE,{"disambiguationData":[TD([[makeQuery(id+"F4.imprint","IMPRINT",EDGE,{"derivedFrom":subQ0}),-1.0]])]});}
            var Q139;
            {var subQ3=sQuery(id+"F4.wireOp",EDGE,"E571");Q139=makeQuery(id+"F4.imprint","IMPRINT",FACE,{"disambiguationData":[TD([[makeQuery(id+"F4.imprint","IMPRINT",EDGE,{"derivedFrom":subQ3}),-1.0]])]});}
            var Q140;
            {var subQ0=sQuery(id+"F4.wireOp",EDGE,"E568");Q140=makeQuery(id+"F4.imprint","IMPRINT",FACE,{"disambiguationData":[TD([[makeQuery(id+"F4.imprint","IMPRINT",EDGE,{"derivedFrom":subQ0}),-1.0]])]});}
            var Q141;
            {var subQ3=sQuery(id+"F4.wireOp",EDGE,"E579");Q141=makeQuery(id+"F4.imprint","IMPRINT",FACE,{"disambiguationData":[TD([[makeQuery(id+"F4.imprint","IMPRINT",EDGE,{"derivedFrom":subQ3}),-1.0]])]});}
            var Q142;
            {var subQ0=sQuery(id+"F4.wireOp",EDGE,"E576");Q142=makeQuery(id+"F4.imprint","IMPRINT",FACE,{"disambiguationData":[TD([[makeQuery(id+"F4.imprint","IMPRINT",EDGE,{"derivedFrom":subQ0}),-1.0]])]});}
            var Q143;
            {var subQ3=sQuery(id+"F4.wireOp",EDGE,"E588");Q143=makeQuery(id+"F4.imprint","IMPRINT",FACE,{"disambiguationData":[TD([[makeQuery(id+"F4.imprint","IMPRINT",EDGE,{"derivedFrom":subQ3}),-1.0]])]});}
            var Q144;
            {var subQ0=sQuery(id+"F4.wireOp",EDGE,"E585");Q144=makeQuery(id+"F4.imprint","IMPRINT",FACE,{"disambiguationData":[TD([[makeQuery(id+"F4.imprint","IMPRINT",EDGE,{"derivedFrom":subQ0}),-1.0]])]});}
            var Q145;
            {var subQ3=sQuery(id+"F4.wireOp",EDGE,"E596");Q145=makeQuery(id+"F4.imprint","IMPRINT",FACE,{"disambiguationData":[TD([[makeQuery(id+"F4.imprint","IMPRINT",EDGE,{"derivedFrom":subQ3}),-1.0]])]});}
            var Q146;
            {var subQ0=sQuery(id+"F4.wireOp",EDGE,"E593");Q146=makeQuery(id+"F4.imprint","IMPRINT",FACE,{"disambiguationData":[TD([[makeQuery(id+"F4.imprint","IMPRINT",EDGE,{"derivedFrom":subQ0}),-1.0]])]});}
            var Q147;
            {var subQ3=sQuery(id+"F4.wireOp",EDGE,"E604");Q147=makeQuery(id+"F4.imprint","IMPRINT",FACE,{"disambiguationData":[TD([[makeQuery(id+"F4.imprint","IMPRINT",EDGE,{"derivedFrom":subQ3}),-1.0]])]});}
            var Q148;
            {var subQ0=sQuery(id+"F4.wireOp",EDGE,"E601");Q148=makeQuery(id+"F4.imprint","IMPRINT",FACE,{"disambiguationData":[TD([[makeQuery(id+"F4.imprint","IMPRINT",EDGE,{"derivedFrom":subQ0}),-1.0]])]});}
            var Q149;
            {var subQ3=sQuery(id+"F4.wireOp",EDGE,"E612");Q149=makeQuery(id+"F4.imprint","IMPRINT",FACE,{"disambiguationData":[TD([[makeQuery(id+"F4.imprint","IMPRINT",EDGE,{"derivedFrom":subQ3}),-1.0]])]});}
            var Q150;
            {var subQ0=sQuery(id+"F4.wireOp",EDGE,"E609");Q150=makeQuery(id+"F4.imprint","IMPRINT",FACE,{"disambiguationData":[TD([[makeQuery(id+"F4.imprint","IMPRINT",EDGE,{"derivedFrom":subQ0}),-1.0]])]});}
            var Q151;
            {var subQ3=sQuery(id+"F4.wireOp",EDGE,"E620");Q151=makeQuery(id+"F4.imprint","IMPRINT",FACE,{"disambiguationData":[TD([[makeQuery(id+"F4.imprint","IMPRINT",EDGE,{"derivedFrom":subQ3}),-1.0]])]});}
            var Q152;
            {var subQ0=sQuery(id+"F4.wireOp",EDGE,"E617");Q152=makeQuery(id+"F4.imprint","IMPRINT",FACE,{"disambiguationData":[TD([[makeQuery(id+"F4.imprint","IMPRINT",EDGE,{"derivedFrom":subQ0}),-1.0]])]});}
            var Q153;
            {var subQ3=sQuery(id+"F4.wireOp",EDGE,"E628");Q153=makeQuery(id+"F4.imprint","IMPRINT",FACE,{"disambiguationData":[TD([[makeQuery(id+"F4.imprint","IMPRINT",EDGE,{"derivedFrom":subQ3}),-1.0]])]});}
            var Q154;
            {var subQ0=sQuery(id+"F4.wireOp",EDGE,"E625");Q154=makeQuery(id+"F4.imprint","IMPRINT",FACE,{"disambiguationData":[TD([[makeQuery(id+"F4.imprint","IMPRINT",EDGE,{"derivedFrom":subQ0}),-1.0]])]});}
            var Q155;
            {var subQ3=sQuery(id+"F4.wireOp",EDGE,"E636");Q155=makeQuery(id+"F4.imprint","IMPRINT",FACE,{"disambiguationData":[TD([[makeQuery(id+"F4.imprint","IMPRINT",EDGE,{"derivedFrom":subQ3}),-1.0]])]});}
            var Q156;
            {var subQ0=sQuery(id+"F4.wireOp",EDGE,"E633");Q156=makeQuery(id+"F4.imprint","IMPRINT",FACE,{"disambiguationData":[TD([[makeQuery(id+"F4.imprint","IMPRINT",EDGE,{"derivedFrom":subQ0}),-1.0]])]});}
            var Q157;
            {var subQ3=sQuery(id+"F4.wireOp",EDGE,"E644");Q157=makeQuery(id+"F4.imprint","IMPRINT",FACE,{"disambiguationData":[TD([[makeQuery(id+"F4.imprint","IMPRINT",EDGE,{"derivedFrom":subQ3}),-1.0]])]});}
            var Q158;
            {var subQ0=sQuery(id+"F4.wireOp",EDGE,"E641");Q158=makeQuery(id+"F4.imprint","IMPRINT",FACE,{"disambiguationData":[TD([[makeQuery(id+"F4.imprint","IMPRINT",EDGE,{"derivedFrom":subQ0}),-1.0]])]});}
            var Q159;
            {var subQ3=sQuery(id+"F4.wireOp",EDGE,"E652");Q159=makeQuery(id+"F4.imprint","IMPRINT",FACE,{"disambiguationData":[TD([[makeQuery(id+"F4.imprint","IMPRINT",EDGE,{"derivedFrom":subQ3}),-1.0]])]});}
            var Q160;
            {var subQ0=sQuery(id+"F4.wireOp",EDGE,"E649");Q160=makeQuery(id+"F4.imprint","IMPRINT",FACE,{"disambiguationData":[TD([[makeQuery(id+"F4.imprint","IMPRINT",EDGE,{"derivedFrom":subQ0}),-1.0]])]});}
            var Q161;
            {var subQ3=sQuery(id+"F4.wireOp",EDGE,"E660");Q161=makeQuery(id+"F4.imprint","IMPRINT",FACE,{"disambiguationData":[TD([[makeQuery(id+"F4.imprint","IMPRINT",EDGE,{"derivedFrom":subQ3}),-1.0]])]});}
            var Q162;
            {var subQ0=sQuery(id+"F4.wireOp",EDGE,"E657");Q162=makeQuery(id+"F4.imprint","IMPRINT",FACE,{"disambiguationData":[TD([[makeQuery(id+"F4.imprint","IMPRINT",EDGE,{"derivedFrom":subQ0}),-1.0]])]});}
            var Q163;
            {var subQ3=sQuery(id+"F4.wireOp",EDGE,"E668");Q163=makeQuery(id+"F4.imprint","IMPRINT",FACE,{"disambiguationData":[TD([[makeQuery(id+"F4.imprint","IMPRINT",EDGE,{"derivedFrom":subQ3}),-1.0]])]});}
            var Q164;
            {var subQ0=sQuery(id+"F4.wireOp",EDGE,"E665");Q164=makeQuery(id+"F4.imprint","IMPRINT",FACE,{"disambiguationData":[TD([[makeQuery(id+"F4.imprint","IMPRINT",EDGE,{"derivedFrom":subQ0}),-1.0]])]});}
            var Q165;
            {var subQ3=sQuery(id+"F4.wireOp",EDGE,"E676");Q165=makeQuery(id+"F4.imprint","IMPRINT",FACE,{"disambiguationData":[TD([[makeQuery(id+"F4.imprint","IMPRINT",EDGE,{"derivedFrom":subQ3}),-1.0]])]});}
            var Q166;
            {var subQ0=sQuery(id+"F4.wireOp",EDGE,"E673");Q166=makeQuery(id+"F4.imprint","IMPRINT",FACE,{"disambiguationData":[TD([[makeQuery(id+"F4.imprint","IMPRINT",EDGE,{"derivedFrom":subQ0}),-1.0]])]});}
            var Q167;
            {var subQ3=sQuery(id+"F4.wireOp",EDGE,"E684");Q167=makeQuery(id+"F4.imprint","IMPRINT",FACE,{"disambiguationData":[TD([[makeQuery(id+"F4.imprint","IMPRINT",EDGE,{"derivedFrom":subQ3}),-1.0]])]});}
            var Q168;
            {var subQ0=sQuery(id+"F4.wireOp",EDGE,"E681");Q168=makeQuery(id+"F4.imprint","IMPRINT",FACE,{"disambiguationData":[TD([[makeQuery(id+"F4.imprint","IMPRINT",EDGE,{"derivedFrom":subQ0}),-1.0]])]});}
            var Q169;
            {var subQ3=sQuery(id+"F4.wireOp",EDGE,"E692");Q169=makeQuery(id+"F4.imprint","IMPRINT",FACE,{"disambiguationData":[TD([[makeQuery(id+"F4.imprint","IMPRINT",EDGE,{"derivedFrom":subQ3}),-1.0]])]});}
            var Q170;
            {var subQ0=sQuery(id+"F4.wireOp",EDGE,"E689");Q170=makeQuery(id+"F4.imprint","IMPRINT",FACE,{"disambiguationData":[TD([[makeQuery(id+"F4.imprint","IMPRINT",EDGE,{"derivedFrom":subQ0}),-1.0]])]});}
            var Q171;
            {var subQ3=sQuery(id+"F4.wireOp",EDGE,"E700");Q171=makeQuery(id+"F4.imprint","IMPRINT",FACE,{"disambiguationData":[TD([[makeQuery(id+"F4.imprint","IMPRINT",EDGE,{"derivedFrom":subQ3}),-1.0]])]});}
            var Q172;
            {var subQ0=sQuery(id+"F4.wireOp",EDGE,"E697");Q172=makeQuery(id+"F4.imprint","IMPRINT",FACE,{"disambiguationData":[TD([[makeQuery(id+"F4.imprint","IMPRINT",EDGE,{"derivedFrom":subQ0}),-1.0]])]});}
            var Q173;
            {var subQ3=sQuery(id+"F4.wireOp",EDGE,"E708");Q173=makeQuery(id+"F4.imprint","IMPRINT",FACE,{"disambiguationData":[TD([[makeQuery(id+"F4.imprint","IMPRINT",EDGE,{"derivedFrom":subQ3}),-1.0]])]});}
            var Q174;
            {var subQ0=sQuery(id+"F4.wireOp",EDGE,"E705");Q174=makeQuery(id+"F4.imprint","IMPRINT",FACE,{"disambiguationData":[TD([[makeQuery(id+"F4.imprint","IMPRINT",EDGE,{"derivedFrom":subQ0}),-1.0]])]});}
            var Q175;
            {var subQ3=sQuery(id+"F4.wireOp",EDGE,"E716");Q175=makeQuery(id+"F4.imprint","IMPRINT",FACE,{"disambiguationData":[TD([[makeQuery(id+"F4.imprint","IMPRINT",EDGE,{"derivedFrom":subQ3}),-1.0]])]});}
            var Q176;
            {var subQ1=sQuery(id+"F4.wireOp",EDGE,"E713");Q176=makeQuery(id+"F4.imprint","IMPRINT",FACE,{"disambiguationData":[TD([[makeQuery(id+"F4.imprint","IMPRINT",EDGE,{"derivedFrom":subQ1}),-1.0]])]});}
            var Q177;
            {var subQ4=sQuery(id+"F4.wireOp",EDGE,"E724");Q177=makeQuery(id+"F4.imprint","IMPRINT",FACE,{"disambiguationData":[TD([[makeQuery(id+"F4.imprint","IMPRINT",EDGE,{"derivedFrom":subQ4}),-1.0]])]});}
            var Q178;
            {var subQ1=sQuery(id+"F4.wireOp",EDGE,"E721");Q178=makeQuery(id+"F4.imprint","IMPRINT",FACE,{"disambiguationData":[TD([[makeQuery(id+"F4.imprint","IMPRINT",EDGE,{"derivedFrom":subQ1}),-1.0]])]});}
            extrude(context, id + "F21", {"entities" : qUnion([Q0, Q1, Q2, Q3, Q4, Q5, Q6, Q7, Q8, Q9, Q10, Q11, Q12, Q13, Q14, Q15, Q16, Q17, Q18, Q19, Q20, Q21, Q22, Q23, Q24, Q25, Q26, Q27, Q28, Q29, Q30, Q31, Q32, Q33, Q34, Q35, Q36, Q37, Q38, Q39, Q40, Q41, Q42, Q43, Q44, Q45, Q46, Q47, Q48, Q49, Q50, Q51, Q52, Q53, Q54, Q55, Q56, Q57, Q58, Q59, Q60, Q61, Q62, Q63, Q64, Q65, Q66, Q67, Q68, Q69, Q70, Q71, Q72, Q73, Q74, Q75, Q76, Q77, Q78, Q79, Q80, Q81, Q82, Q83, Q84, Q85, Q86, Q87, Q88, Q89, Q90, Q91, Q92, Q93, Q94, Q95, Q96, Q97, Q98, Q99, Q100, Q101, Q102, Q103, Q104, Q105, Q106, Q107, Q108, Q109, Q110, Q111, Q112, Q113, Q114, Q115, Q116, Q117, Q118, Q119, Q120, Q121, Q122, Q123, Q124, Q125, Q126, Q127, Q128, Q129, Q130, Q131, Q132, Q133, Q134, Q135, Q136, Q137, Q138, Q139, Q140, Q141, Q142, Q143, Q144, Q145, Q146, Q147, Q148, Q149, Q150, Q151, Q152, Q153, Q154, Q155, Q156, Q157, Q158, Q159, Q160, Q161, Q162, Q163, Q164, Q165, Q166, Q167, Q168, Q169, Q170, Q171, Q172, Q173, Q174, Q175, Q176, Q177, Q178]), "operationType" : NewBodyOperationType.REMOVE, "oppositeDirection" : true, "depth" : 50 * mm});
        }
        {
            var Q0;
            {var subQ3=sQuery(id+"F4.wireOp",EDGE,"E27");Q0=makeQuery(id+"F4.imprint","IMPRINT",FACE,{"disambiguationData":[TD([[makeQuery(id+"F4.imprint","IMPRINT",EDGE,{"derivedFrom":subQ3}),-1.0]])]});}
            extrude(context, id + "F22", {"entities" : qUnion([Q0]), "operationType" : NewBodyOperationType.REMOVE, "oppositeDirection" : true, "depth" : 50 * mm});
        }
        {
            var Q0;
            {var subQ0=sQuery(id+"F15.wireOp",EDGE,"E746");var subQ1=sQuery(id+"F0.wireOp",EDGE,"E0.bottom");var subQ2=sQuery(id+"F0.wireOp",EDGE,"E0.top");Q0=makeQuery(id+"F19.boolean.opBoolean","MERGE",FACE,{"derivedFrom":[makeQuery(id+"F1.opExtrude","CAP_FACE",FACE,{"disambiguationData":[OSD([subQ1,subQ2,sQuery(id+"F0.wireOp",EDGE,"E0.left"),sQuery(id+"F0.wireOp",EDGE,"E0.right")])],"isStart":false}),makeQuery(id+"F19.opExtrude","CAP_FACE",FACE,{"disambiguationData":[OSD([subQ2,subQ0])],"isStart":false}),makeQuery(id+"F19.opExtrude","CAP_FACE",FACE,{"disambiguationData":[OSD([subQ1,subQ0])],"isStart":false})]});}
            var sketch = newSketch(context, id + "F23", { "sketchPlane" : qUnion([Q0])});
            skLineSegment(sketch, "E754", {"start": v(-86291.7, 42.27) * mm, "end": v(-89755.8, 42.27) * mm});
            skLineSegment(sketch, "E755", {"start": v(-86291.7, 2042.27) * mm, "end": v(-89755.8, 2042.27) * mm});
            skLineSegment(sketch, "E756", {"start": v(-90023.74, 1042.27) * mm, "end": v(-88023.74, 1042.27) * mm});
            skCircle(sketch, "E757", {"center": v(-88023.74, 1042.27) * mm, "radius": 1975 * mm});
            skSolve(sketch);
        }
        {
            var Q0;
            {var subQ0=sQuery(id+"F23.wireOp",EDGE,"E757");var subQ1=sQuery(id+"F23.wireOp",EDGE,"E754");var subQ2=makeQuery(id+"F23.imprint","INTERSECT",VERTEX,{"disambiguationData":[OD(0.0)],"derivedFrom":[subQ1,subQ0]});Q0=makeQuery(id+"F23.imprint","IMPRINT",FACE,{"disambiguationData":[TD([[makeQuery(id+"F23.imprint","IMPRINT",EDGE,{"disambiguationData":[TD([[subQ2,-1.0]])],"derivedFrom":subQ1}),1.0]])]});}
            var Q1;
            {var subQ0=sQuery(id+"F23.wireOp",EDGE,"E757");var subQ1=sQuery(id+"F23.wireOp",EDGE,"E755");var subQ2=makeQuery(id+"F23.imprint","INTERSECT",VERTEX,{"disambiguationData":[OD(0.0)],"derivedFrom":[subQ1,subQ0]});Q1=makeQuery(id+"F23.imprint","IMPRINT",FACE,{"disambiguationData":[TD([[makeQuery(id+"F23.imprint","IMPRINT",EDGE,{"disambiguationData":[TD([[subQ2,-1.0]])],"derivedFrom":subQ1}),-1.0]])]});}
            extrude(context, id + "F24", {"entities" : qUnion([Q0, Q1]), "operationType" : NewBodyOperationType.REMOVE, "oppositeDirection" : true, "depth" : 2450 * mm});
        }
        {
            var Q0;
            {var subQ104=sQuery(id+"F4.wireOp",EDGE,"E11");Q0=makeQuery(id+"F4.imprint","IMPRINT",FACE,{"disambiguationData":[TD([[makeQuery(id+"F4.imprint","IMPRINT",EDGE,{"derivedFrom":subQ104}),1.0]])]});}
            extrude(context, id + "F25", {"entities" : qUnion([Q0]), "operationType" : NewBodyOperationType.REMOVE, "oppositeDirection" : true, "depth" : 5000 * mm});
        }
        {
            var Q0;
            {var subQ0=sQuery(id+"F15.wireOp",EDGE,"E746");var subQ1=sQuery(id+"F0.wireOp",EDGE,"E0.top");var subQ4=sQuery(id+"F0.wireOp",EDGE,"E0.right");var subQ5=makeQuery(id+"F1.opExtrude","SWEPT_FACE",FACE,{"disambiguationData":[OSD([subQ4])]});var subQ6=makeQuery(id+"F19.opExtrude","CAP_FACE",FACE,{"disambiguationData":[OSD([subQ1,subQ0])],"isStart":true});Q0=makeQuery(id+"F25.boolean.opBoolean","SPLIT",FACE,{"disambiguationData":[TD([subQ6])],"derivedFrom":makeQuery(id+"F19.boolean.opBoolean","SPLIT",FACE,{"disambiguationData":[TD([subQ5])],"derivedFrom":makeQuery(id+"F1.opExtrude","SWEPT_FACE",FACE,{"disambiguationData":[OSD([subQ1])]})})});}
            var sketch = newSketch(context, id + "F26", { "sketchPlane" : qUnion([Q0])});
            skFitSpline(sketch, "E758.0", {"points": [v(-23.74, 33) * mm, v(-154.98, 314.71) * mm, v(-426.94, 898.5) * mm, v(-1061.15, -433.35) * mm, v(-1413.74, 1024.1) * mm, v(-2064.5, -465.34) * mm, v(-2412.79, 1033.12) * mm, v(-3064.75, -467.63) * mm, v(-3412.72, 1033.76) * mm, v(-4064.77, -467.8) * mm, v(-4412.72, 1033.8) * mm, v(-5064.77, -467.81) * mm, v(-5412.72, 1033.81) * mm, v(-6064.77, -467.81) * mm, v(-6412.72, 1033.81) * mm, v(-7064.77, -467.81) * mm, v(-7412.72, 1033.81) * mm, v(-8064.77, -467.81) * mm, v(-8412.72, 1033.81) * mm, v(-9064.77, -467.81) * mm, v(-9412.72, 1033.81) * mm, v(-10064.77, -467.81) * mm, v(-10412.72, 1033.81) * mm, v(-11064.77, -467.81) * mm, v(-11412.72, 1033.81) * mm, v(-12064.77, -467.81) * mm, v(-12412.72, 1033.81) * mm, v(-13064.77, -467.81) * mm, v(-13412.72, 1033.81) * mm, v(-14064.77, -467.81) * mm, v(-14412.72, 1033.81) * mm, v(-15064.77, -467.81) * mm, v(-15412.72, 1033.81) * mm, v(-16064.77, -467.81) * mm, v(-16412.72, 1033.81) * mm, v(-17064.77, -467.81) * mm, v(-17412.72, 1033.81) * mm, v(-18064.77, -467.81) * mm, v(-18412.72, 1033.81) * mm, v(-19064.77, -467.81) * mm, v(-19412.72, 1033.81) * mm, v(-20064.77, -467.81) * mm, v(-20412.72, 1033.81) * mm, v(-21064.77, -467.81) * mm, v(-21412.72, 1033.81) * mm, v(-22064.77, -467.81) * mm, v(-22412.72, 1033.81) * mm, v(-23064.77, -467.81) * mm, v(-23412.72, 1033.81) * mm, v(-24064.77, -467.81) * mm, v(-24412.72, 1033.81) * mm, v(-25064.77, -467.81) * mm, v(-25412.72, 1033.81) * mm, v(-26064.77, -467.81) * mm, v(-26412.72, 1033.81) * mm, v(-27064.77, -467.81) * mm, v(-27412.72, 1033.81) * mm, v(-28064.77, -467.81) * mm, v(-28412.72, 1033.81) * mm, v(-29064.77, -467.81) * mm, v(-29412.72, 1033.81) * mm, v(-30064.77, -467.81) * mm, v(-30412.72, 1033.81) * mm, v(-31064.77, -467.81) * mm, v(-31412.72, 1033.81) * mm, v(-32064.77, -467.81) * mm, v(-32412.72, 1033.81) * mm, v(-33064.77, -467.81) * mm, v(-33412.72, 1033.81) * mm, v(-34064.77, -467.81) * mm, v(-34412.72, 1033.81) * mm, v(-35064.77, -467.81) * mm, v(-35412.72, 1033.81) * mm, v(-36064.77, -467.81) * mm, v(-36412.72, 1033.81) * mm, v(-37064.77, -467.81) * mm, v(-37412.72, 1033.81) * mm, v(-38064.77, -467.81) * mm, v(-38412.72, 1033.81) * mm, v(-39064.77, -467.81) * mm, v(-39412.72, 1033.81) * mm, v(-40064.77, -467.81) * mm, v(-40412.72, 1033.81) * mm, v(-41064.77, -467.81) * mm, v(-41412.72, 1033.81) * mm, v(-42064.77, -467.81) * mm, v(-42412.72, 1033.81) * mm, v(-43064.77, -467.81) * mm, v(-43412.72, 1033.81) * mm, v(-44064.77, -467.81) * mm, v(-44412.72, 1033.81) * mm, v(-45064.77, -467.81) * mm, v(-45412.72, 1033.81) * mm, v(-46064.77, -467.81) * mm, v(-46412.72, 1033.81) * mm, v(-47064.77, -467.81) * mm, v(-47412.72, 1033.81) * mm, v(-48064.77, -467.81) * mm, v(-48412.72, 1033.81) * mm, v(-49064.77, -467.81) * mm, v(-49412.72, 1033.81) * mm, v(-50064.77, -467.81) * mm, v(-50412.72, 1033.81) * mm, v(-51064.77, -467.81) * mm, v(-51412.72, 1033.81) * mm, v(-52064.77, -467.81) * mm, v(-52412.72, 1033.81) * mm, v(-53064.77, -467.81) * mm, v(-53412.72, 1033.81) * mm, v(-54064.77, -467.81) * mm, v(-54412.72, 1033.81) * mm, v(-55064.77, -467.81) * mm, v(-55412.72, 1033.81) * mm, v(-56064.77, -467.81) * mm, v(-56412.72, 1033.81) * mm, v(-57064.77, -467.81) * mm, v(-57412.72, 1033.81) * mm, v(-58064.77, -467.81) * mm, v(-58412.72, 1033.81) * mm, v(-59064.77, -467.81) * mm, v(-59412.72, 1033.81) * mm, v(-60064.77, -467.81) * mm, v(-60412.72, 1033.81) * mm, v(-61064.77, -467.81) * mm, v(-61412.72, 1033.81) * mm, v(-62064.77, -467.81) * mm, v(-62412.72, 1033.81) * mm, v(-63064.77, -467.81) * mm, v(-63412.72, 1033.81) * mm, v(-64064.77, -467.81) * mm, v(-64412.72, 1033.81) * mm, v(-65064.77, -467.81) * mm, v(-65412.72, 1033.81) * mm, v(-66064.77, -467.81) * mm, v(-66412.72, 1033.81) * mm, v(-67064.77, -467.81) * mm, v(-67412.72, 1033.81) * mm, v(-68064.77, -467.81) * mm, v(-68412.72, 1033.81) * mm, v(-69064.77, -467.81) * mm, v(-69412.72, 1033.81) * mm, v(-70064.77, -467.81) * mm, v(-70412.72, 1033.81) * mm, v(-71064.77, -467.81) * mm, v(-71412.72, 1033.81) * mm, v(-72064.77, -467.81) * mm, v(-72412.72, 1033.81) * mm, v(-73064.77, -467.81) * mm, v(-73412.72, 1033.81) * mm, v(-74064.77, -467.81) * mm, v(-74412.72, 1033.81) * mm, v(-75064.77, -467.81) * mm, v(-75412.72, 1033.81) * mm, v(-76064.77, -467.81) * mm, v(-76412.72, 1033.81) * mm, v(-77064.77, -467.81) * mm, v(-77412.72, 1033.81) * mm, v(-78064.77, -467.81) * mm, v(-78412.72, 1033.81) * mm, v(-79064.77, -467.81) * mm, v(-79412.72, 1033.81) * mm, v(-80064.77, -467.81) * mm, v(-80412.72, 1033.81) * mm, v(-81064.77, -467.81) * mm, v(-81412.72, 1033.81) * mm, v(-82064.77, -467.81) * mm, v(-82412.72, 1033.81) * mm, v(-83064.77, -467.81) * mm, v(-83412.72, 1033.81) * mm, v(-84064.77, -467.81) * mm, v(-84412.72, 1033.81) * mm, v(-85064.77, -467.81) * mm, v(-85412.72, 1033.8) * mm, v(-86064.77, -467.8) * mm, v(-86412.72, 1033.76) * mm, v(-87064.75, -467.62) * mm, v(-87412.79, 1033.13) * mm, v(-88064.49, -465.13) * mm, v(-88413.72, 1024.3) * mm, v(-89060.84, -430.46) * mm, v(-89426.66, 901.2) * mm, v(-89820.14, 329.05) * mm, v(-90023.74, 33) * mm]});
            skSolve(sketch);
        }
        {
            var Q0;
            {var subQ1=sQuery(id+"F0.wireOp",EDGE,"E0.right");var subQ2=makeQuery(id+"F1.opExtrude","SWEPT_FACE",FACE,{"disambiguationData":[OSD([subQ1])]});var subQ3=sQuery(id+"F0.wireOp",EDGE,"E0.top");var subQ4=makeQuery(id+"F1.opExtrude","SWEPT_FACE",FACE,{"disambiguationData":[OSD([subQ3])]});var subQ11=makeQuery(id+"F25.opExtrude","SWEPT_FACE",FACE,{"disambiguationData":[OSD([sQuery(id+"F4.wireOp",EDGE,"E10"),sQuery(id+"F4.wireOp",EDGE,"E11"),sQuery(id+"F4.wireOp",EDGE,"E20"),sQuery(id+"F4.wireOp",EDGE,"E23"),sQuery(id+"F4.wireOp",EDGE,"E24"),sQuery(id+"F4.wireOp",EDGE,"E31"),sQuery(id+"F4.wireOp",EDGE,"E32"),sQuery(id+"F4.wireOp",EDGE,"E39"),sQuery(id+"F4.wireOp",EDGE,"E40"),sQuery(id+"F4.wireOp",EDGE,"E47"),sQuery(id+"F4.wireOp",EDGE,"E48"),sQuery(id+"F4.wireOp",EDGE,"E55"),sQuery(id+"F4.wireOp",EDGE,"E56"),sQuery(id+"F4.wireOp",EDGE,"E63"),sQuery(id+"F4.wireOp",EDGE,"E64"),sQuery(id+"F4.wireOp",EDGE,"E72"),sQuery(id+"F4.wireOp",EDGE,"E73"),sQuery(id+"F4.wireOp",EDGE,"E80"),sQuery(id+"F4.wireOp",EDGE,"E81"),sQuery(id+"F4.wireOp",EDGE,"E88"),sQuery(id+"F4.wireOp",EDGE,"E89"),sQuery(id+"F4.wireOp",EDGE,"E96"),sQuery(id+"F4.wireOp",EDGE,"E97"),sQuery(id+"F4.wireOp",EDGE,"E104"),sQuery(id+"F4.wireOp",EDGE,"E105"),sQuery(id+"F4.wireOp",EDGE,"E112"),sQuery(id+"F4.wireOp",EDGE,"E113"),sQuery(id+"F4.wireOp",EDGE,"E120"),sQuery(id+"F4.wireOp",EDGE,"E121"),sQuery(id+"F4.wireOp",EDGE,"E128"),sQuery(id+"F4.wireOp",EDGE,"E129"),sQuery(id+"F4.wireOp",EDGE,"E136"),sQuery(id+"F4.wireOp",EDGE,"E137"),sQuery(id+"F4.wireOp",EDGE,"E144"),sQuery(id+"F4.wireOp",EDGE,"E145"),sQuery(id+"F4.wireOp",EDGE,"E152"),sQuery(id+"F4.wireOp",EDGE,"E153"),sQuery(id+"F4.wireOp",EDGE,"E160"),sQuery(id+"F4.wireOp",EDGE,"E161"),sQuery(id+"F4.wireOp",EDGE,"E168"),sQuery(id+"F4.wireOp",EDGE,"E169"),sQuery(id+"F4.wireOp",EDGE,"E176"),sQuery(id+"F4.wireOp",EDGE,"E177"),sQuery(id+"F4.wireOp",EDGE,"E184"),sQuery(id+"F4.wireOp",EDGE,"E185"),sQuery(id+"F4.wireOp",EDGE,"E192"),sQuery(id+"F4.wireOp",EDGE,"E193"),sQuery(id+"F4.wireOp",EDGE,"E200"),sQuery(id+"F4.wireOp",EDGE,"E201"),sQuery(id+"F4.wireOp",EDGE,"E208"),sQuery(id+"F4.wireOp",EDGE,"E209"),sQuery(id+"F4.wireOp",EDGE,"E216"),sQuery(id+"F4.wireOp",EDGE,"E217"),sQuery(id+"F4.wireOp",EDGE,"E225"),sQuery(id+"F4.wireOp",EDGE,"E226"),sQuery(id+"F4.wireOp",EDGE,"E233"),sQuery(id+"F4.wireOp",EDGE,"E234"),sQuery(id+"F4.wireOp",EDGE,"E241"),sQuery(id+"F4.wireOp",EDGE,"E242"),sQuery(id+"F4.wireOp",EDGE,"E249"),sQuery(id+"F4.wireOp",EDGE,"E250"),sQuery(id+"F4.wireOp",EDGE,"E257"),sQuery(id+"F4.wireOp",EDGE,"E258"),sQuery(id+"F4.wireOp",EDGE,"E265"),sQuery(id+"F4.wireOp",EDGE,"E266"),sQuery(id+"F4.wireOp",EDGE,"E273"),sQuery(id+"F4.wireOp",EDGE,"E274"),sQuery(id+"F4.wireOp",EDGE,"E281"),sQuery(id+"F4.wireOp",EDGE,"E282"),sQuery(id+"F4.wireOp",EDGE,"E289"),sQuery(id+"F4.wireOp",EDGE,"E290"),sQuery(id+"F4.wireOp",EDGE,"E297"),sQuery(id+"F4.wireOp",EDGE,"E298"),sQuery(id+"F4.wireOp",EDGE,"E305"),sQuery(id+"F4.wireOp",EDGE,"E306"),sQuery(id+"F4.wireOp",EDGE,"E313"),sQuery(id+"F4.wireOp",EDGE,"E314"),sQuery(id+"F4.wireOp",EDGE,"E321"),sQuery(id+"F4.wireOp",EDGE,"E322"),sQuery(id+"F4.wireOp",EDGE,"E329"),sQuery(id+"F4.wireOp",EDGE,"E330"),sQuery(id+"F4.wireOp",EDGE,"E337"),sQuery(id+"F4.wireOp",EDGE,"E338"),sQuery(id+"F4.wireOp",EDGE,"E345"),sQuery(id+"F4.wireOp",EDGE,"E346"),sQuery(id+"F4.wireOp",EDGE,"E353"),sQuery(id+"F4.wireOp",EDGE,"E354"),sQuery(id+"F4.wireOp",EDGE,"E361"),sQuery(id+"F4.wireOp",EDGE,"E362"),sQuery(id+"F4.wireOp",EDGE,"E369"),sQuery(id+"F4.wireOp",EDGE,"E370"),sQuery(id+"F4.wireOp",EDGE,"E379"),sQuery(id+"F4.wireOp",EDGE,"E382"),sQuery(id+"F4.wireOp",EDGE,"E383"),sQuery(id+"F4.wireOp",EDGE,"E390"),sQuery(id+"F4.wireOp",EDGE,"E391"),sQuery(id+"F4.wireOp",EDGE,"E398"),sQuery(id+"F4.wireOp",EDGE,"E399"),sQuery(id+"F4.wireOp",EDGE,"E406"),sQuery(id+"F4.wireOp",EDGE,"E407"),sQuery(id+"F4.wireOp",EDGE,"E414"),sQuery(id+"F4.wireOp",EDGE,"E415"),sQuery(id+"F4.wireOp",EDGE,"E422"),sQuery(id+"F4.wireOp",EDGE,"E423"),sQuery(id+"F4.wireOp",EDGE,"E431"),sQuery(id+"F4.wireOp",EDGE,"E432"),sQuery(id+"F4.wireOp",EDGE,"E439"),sQuery(id+"F4.wireOp",EDGE,"E440"),sQuery(id+"F4.wireOp",EDGE,"E447"),sQuery(id+"F4.wireOp",EDGE,"E448"),sQuery(id+"F4.wireOp",EDGE,"E455"),sQuery(id+"F4.wireOp",EDGE,"E456"),sQuery(id+"F4.wireOp",EDGE,"E463"),sQuery(id+"F4.wireOp",EDGE,"E464"),sQuery(id+"F4.wireOp",EDGE,"E471"),sQuery(id+"F4.wireOp",EDGE,"E472"),sQuery(id+"F4.wireOp",EDGE,"E479"),sQuery(id+"F4.wireOp",EDGE,"E480"),sQuery(id+"F4.wireOp",EDGE,"E487"),sQuery(id+"F4.wireOp",EDGE,"E488"),sQuery(id+"F4.wireOp",EDGE,"E495"),sQuery(id+"F4.wireOp",EDGE,"E496"),sQuery(id+"F4.wireOp",EDGE,"E503"),sQuery(id+"F4.wireOp",EDGE,"E504"),sQuery(id+"F4.wireOp",EDGE,"E511"),sQuery(id+"F4.wireOp",EDGE,"E512"),sQuery(id+"F4.wireOp",EDGE,"E519"),sQuery(id+"F4.wireOp",EDGE,"E520"),sQuery(id+"F4.wireOp",EDGE,"E527"),sQuery(id+"F4.wireOp",EDGE,"E528"),sQuery(id+"F4.wireOp",EDGE,"E535"),sQuery(id+"F4.wireOp",EDGE,"E536"),sQuery(id+"F4.wireOp",EDGE,"E543"),sQuery(id+"F4.wireOp",EDGE,"E544"),sQuery(id+"F4.wireOp",EDGE,"E551"),sQuery(id+"F4.wireOp",EDGE,"E552"),sQuery(id+"F4.wireOp",EDGE,"E559"),sQuery(id+"F4.wireOp",EDGE,"E560"),sQuery(id+"F4.wireOp",EDGE,"E567"),sQuery(id+"F4.wireOp",EDGE,"E568"),sQuery(id+"F4.wireOp",EDGE,"E575"),sQuery(id+"F4.wireOp",EDGE,"E576"),sQuery(id+"F4.wireOp",EDGE,"E584"),sQuery(id+"F4.wireOp",EDGE,"E585"),sQuery(id+"F4.wireOp",EDGE,"E592"),sQuery(id+"F4.wireOp",EDGE,"E593"),sQuery(id+"F4.wireOp",EDGE,"E600"),sQuery(id+"F4.wireOp",EDGE,"E601"),sQuery(id+"F4.wireOp",EDGE,"E608"),sQuery(id+"F4.wireOp",EDGE,"E609"),sQuery(id+"F4.wireOp",EDGE,"E616"),sQuery(id+"F4.wireOp",EDGE,"E617"),sQuery(id+"F4.wireOp",EDGE,"E624"),sQuery(id+"F4.wireOp",EDGE,"E625"),sQuery(id+"F4.wireOp",EDGE,"E632"),sQuery(id+"F4.wireOp",EDGE,"E633"),sQuery(id+"F4.wireOp",EDGE,"E640"),sQuery(id+"F4.wireOp",EDGE,"E641"),sQuery(id+"F4.wireOp",EDGE,"E648"),sQuery(id+"F4.wireOp",EDGE,"E649"),sQuery(id+"F4.wireOp",EDGE,"E656"),sQuery(id+"F4.wireOp",EDGE,"E657"),sQuery(id+"F4.wireOp",EDGE,"E664"),sQuery(id+"F4.wireOp",EDGE,"E665"),sQuery(id+"F4.wireOp",EDGE,"E672"),sQuery(id+"F4.wireOp",EDGE,"E673"),sQuery(id+"F4.wireOp",EDGE,"E680"),sQuery(id+"F4.wireOp",EDGE,"E681"),sQuery(id+"F4.wireOp",EDGE,"E688"),sQuery(id+"F4.wireOp",EDGE,"E689"),sQuery(id+"F4.wireOp",EDGE,"E696"),sQuery(id+"F4.wireOp",EDGE,"E697"),sQuery(id+"F4.wireOp",EDGE,"E704"),sQuery(id+"F4.wireOp",EDGE,"E705"),sQuery(id+"F4.wireOp",EDGE,"E712"),sQuery(id+"F4.wireOp",EDGE,"E713"),sQuery(id+"F4.wireOp",EDGE,"E720"),sQuery(id+"F4.wireOp",EDGE,"E721")])]});var subQ19=makeQuery(id+"F25.boolean.opBoolean","INTERSECT",EDGE,{"derivedFrom":[makeQuery(id+"F19.boolean.opBoolean","SPLIT",FACE,{"disambiguationData":[TD([subQ2])],"derivedFrom":subQ4}),subQ11]});Q0=makeQuery(id+"F26.imprint","IMPRINT",FACE,{"disambiguationData":[TD([[makeQuery(id+"F26.imprint","IMPRINT",EDGE,{"derivedFrom":subQ19}),-1.0]])]});}
            extrude(context, id + "F27", {"entities" : qUnion([Q0]), "operationType" : NewBodyOperationType.REMOVE, "oppositeDirection" : true, "depth" : 50 * mm});
        }
        {
            var Q0;
            {var subQ0=sQuery(id+"F6.wireOp",EDGE,"E742");var subQ1=makeQuery(id+"F1.opExtrude","CAP_EDGE",EDGE,{"disambiguationData":[OSD([sQuery(id+"F0.wireOp",EDGE,"E0.bottom")])],"isStart":false});var subQ2=makeQuery(id+"F6.imprint","INTERSECT",VERTEX,{"disambiguationData":[OD(0.0)],"derivedFrom":[subQ1,subQ0]});Q0=makeQuery(id+"F6.imprint","IMPRINT",FACE,{"disambiguationData":[TD([[makeQuery(id+"F6.imprint","IMPRINT",EDGE,{"disambiguationData":[TD([[subQ2,1.0]])],"derivedFrom":subQ0}),1.0]])]});}
            var Q1;
            {var subQ0=sQuery(id+"F6.wireOp",EDGE,"E742");var subQ1=makeQuery(id+"F1.opExtrude","CAP_EDGE",EDGE,{"disambiguationData":[OSD([sQuery(id+"F0.wireOp",EDGE,"E0.top")])],"isStart":false});var subQ2=makeQuery(id+"F6.imprint","INTERSECT",VERTEX,{"disambiguationData":[OD(0.0)],"derivedFrom":[subQ1,subQ0]});Q1=makeQuery(id+"F6.imprint","IMPRINT",FACE,{"disambiguationData":[TD([[makeQuery(id+"F6.imprint","IMPRINT",EDGE,{"disambiguationData":[TD([[subQ2,-1.0]])],"derivedFrom":subQ0}),1.0]])]});}
            var Q2;
            {var subQ0=sQuery(id+"F6.wireOp",EDGE,"E742");var subQ6=makeQuery(id+"F6.imprint","INTERSECT",VERTEX,{"derivedFrom":[makeQuery(id+"F1.opExtrude","CAP_EDGE",EDGE,{"disambiguationData":[OSD([sQuery(id+"F0.wireOp",EDGE,"E0.left")])],"isStart":false}),subQ0]});Q2=makeQuery(id+"F6.imprint","IMPRINT",FACE,{"disambiguationData":[TD([[makeQuery(id+"F6.imprint","IMPRINT",EDGE,{"disambiguationData":[TD([[subQ6,1.0]])],"derivedFrom":subQ0}),1.0]])]});}
            extrude(context, id + "F28", {"entities" : qUnion([Q0, Q1, Q2]), "operationType" : NewBodyOperationType.ADD, "depth" : 25 * mm});
        }
    });
